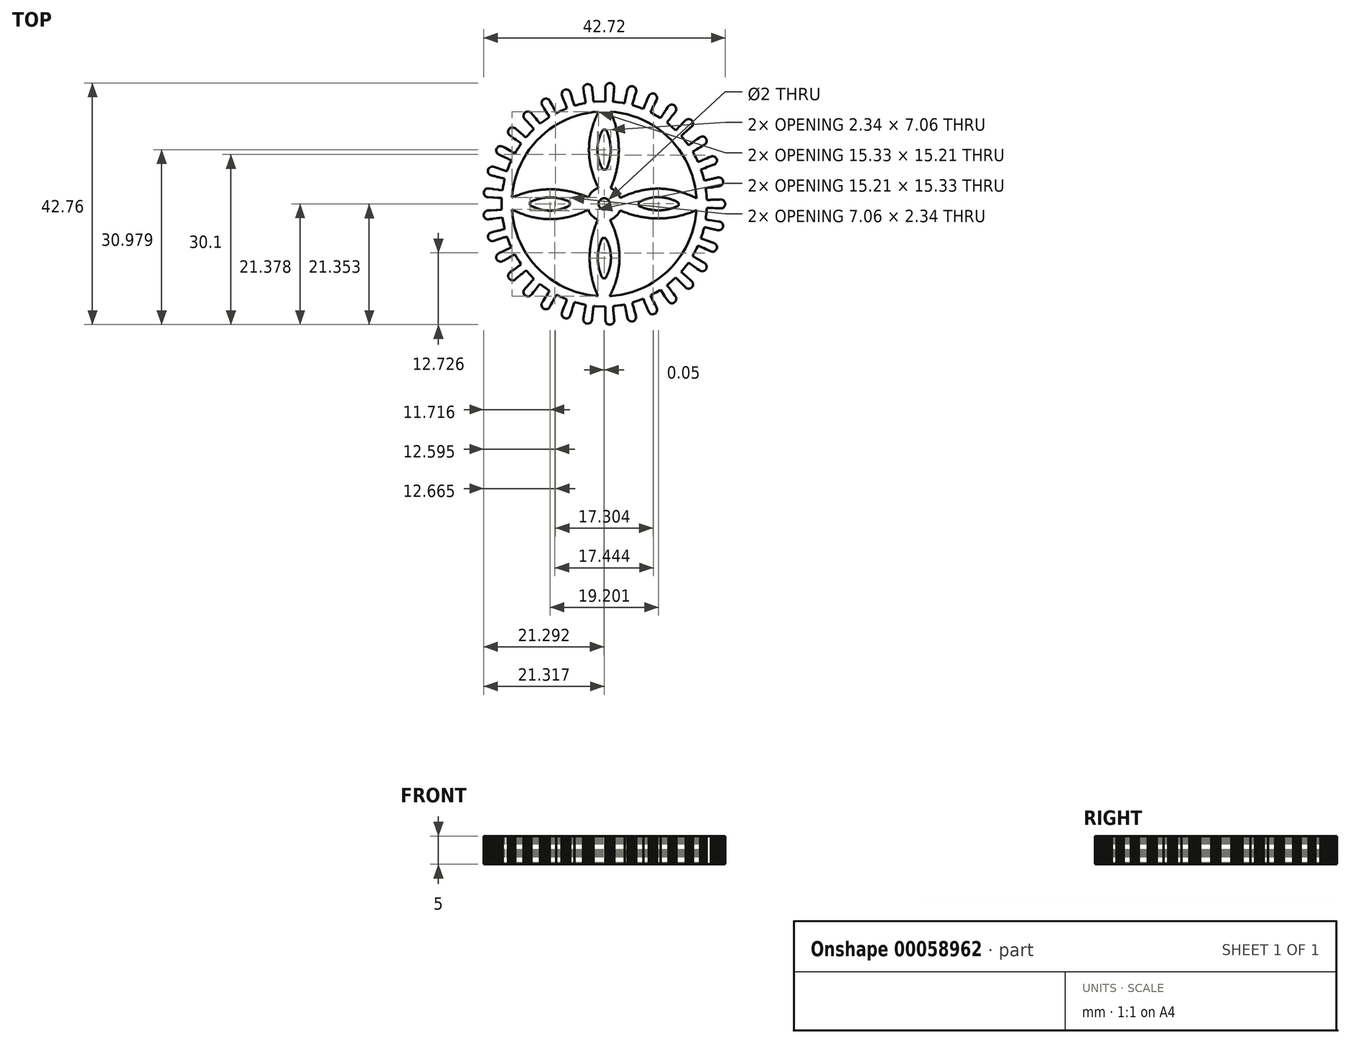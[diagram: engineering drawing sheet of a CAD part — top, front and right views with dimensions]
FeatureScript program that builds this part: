
annotation { "Feature Type Name" : "Feature", "Feature Type Description" : "" }
export const myFeature = defineFeature(function(context is Context, id is Id, definition is map)
    precondition{}
    {
        {
            var Q0;
            Q0=qCreatedBy(makeId("Top.planeOp"),FACE);
            var sketch = newSketch(context, id + "F0", { "sketchPlane" : qUnion([Q0])});
            skLineSegment(sketch, "E0", {"start": v(17.14, -0.7) * mm, "end": v(17.3, -0.7) * mm});
            skLineSegment(sketch, "E1", {"start": v(17.3, -0.7) * mm, "end": v(17.5, -0.7) * mm});
            skLineSegment(sketch, "E2", {"start": v(17.5, -0.7) * mm, "end": v(17.68, -0.71) * mm});
            skLineSegment(sketch, "E3", {"start": v(17.68, -0.71) * mm, "end": v(17.87, -0.72) * mm});
            skLineSegment(sketch, "E4", {"start": v(17.87, -0.72) * mm, "end": v(18.06, -0.73) * mm});
            skLineSegment(sketch, "E5", {"start": v(18.06, -0.73) * mm, "end": v(18.25, -0.73) * mm});
            skLineSegment(sketch, "E6", {"start": v(18.25, -0.73) * mm, "end": v(18.45, -0.74) * mm});
            skLineSegment(sketch, "E7", {"start": v(18.45, -0.74) * mm, "end": v(18.63, -0.75) * mm});
            skLineSegment(sketch, "E8", {"start": v(18.63, -0.75) * mm, "end": v(18.82, -0.75) * mm});
            skLineSegment(sketch, "E9", {"start": v(18.82, -0.75) * mm, "end": v(19.02, -0.76) * mm});
            skLineSegment(sketch, "E10", {"start": v(19.02, -0.76) * mm, "end": v(19.2, -0.77) * mm});
            skLineSegment(sketch, "E11", {"start": v(19.2, -0.77) * mm, "end": v(19.4, -0.78) * mm});
            skLineSegment(sketch, "E12", {"start": v(19.4, -0.78) * mm, "end": v(19.59, -0.78) * mm});
            skLineSegment(sketch, "E13", {"start": v(19.59, -0.78) * mm, "end": v(19.8, -0.76) * mm});
            skLineSegment(sketch, "E14", {"start": v(19.8, -0.76) * mm, "end": v(19.98, -0.68) * mm});
            skLineSegment(sketch, "E15", {"start": v(19.98, -0.68) * mm, "end": v(20.15, -0.56) * mm});
            skLineSegment(sketch, "E16", {"start": v(20.15, -0.56) * mm, "end": v(20.28, -0.4) * mm});
            skLineSegment(sketch, "E17", {"start": v(20.28, -0.4) * mm, "end": v(20.36, -0.2) * mm});
            skLineSegment(sketch, "E18", {"start": v(20.36, -0.2) * mm, "end": v(20.38, 0) * mm});
            skLineSegment(sketch, "E19", {"start": v(20.38, 0) * mm, "end": v(20.36, 0.2) * mm});
            skLineSegment(sketch, "E20", {"start": v(20.36, 0.2) * mm, "end": v(20.28, 0.4) * mm});
            skLineSegment(sketch, "E21", {"start": v(20.28, 0.4) * mm, "end": v(20.15, 0.56) * mm});
            skLineSegment(sketch, "E22", {"start": v(20.15, 0.56) * mm, "end": v(19.98, 0.68) * mm});
            skLineSegment(sketch, "E23", {"start": v(19.98, 0.68) * mm, "end": v(19.8, 0.76) * mm});
            skLineSegment(sketch, "E24", {"start": v(19.8, 0.76) * mm, "end": v(19.59, 0.78) * mm});
            skLineSegment(sketch, "E25", {"start": v(19.59, 0.78) * mm, "end": v(19.4, 0.77) * mm});
            skLineSegment(sketch, "E26", {"start": v(19.4, 0.77) * mm, "end": v(19.2, 0.77) * mm});
            skLineSegment(sketch, "E27", {"start": v(19.2, 0.77) * mm, "end": v(19.02, 0.76) * mm});
            skLineSegment(sketch, "E28", {"start": v(19.02, 0.76) * mm, "end": v(18.83, 0.75) * mm});
            skLineSegment(sketch, "E29", {"start": v(18.83, 0.75) * mm, "end": v(18.64, 0.74) * mm});
            skLineSegment(sketch, "E30", {"start": v(18.64, 0.74) * mm, "end": v(18.45, 0.74) * mm});
            skLineSegment(sketch, "E31", {"start": v(18.45, 0.74) * mm, "end": v(18.26, 0.73) * mm});
            skLineSegment(sketch, "E32", {"start": v(18.26, 0.73) * mm, "end": v(18.07, 0.72) * mm});
            skLineSegment(sketch, "E33", {"start": v(18.07, 0.72) * mm, "end": v(17.87, 0.71) * mm});
            skLineSegment(sketch, "E34", {"start": v(17.87, 0.71) * mm, "end": v(17.69, 0.7) * mm});
            skLineSegment(sketch, "E35", {"start": v(17.69, 0.7) * mm, "end": v(17.5, 0.7) * mm});
            skLineSegment(sketch, "E36", {"start": v(17.5, 0.7) * mm, "end": v(17.3, 0.7) * mm});
            skLineSegment(sketch, "E37", {"start": v(17.3, 0.7) * mm, "end": v(17.14, 0.69) * mm});
            skLineSegment(sketch, "E38", {"start": v(17.14, 0.69) * mm, "end": v(17.12, 0.88) * mm});
            skLineSegment(sketch, "E39", {"start": v(17.12, 0.88) * mm, "end": v(17.1, 1.06) * mm});
            skLineSegment(sketch, "E40", {"start": v(17.1, 1.06) * mm, "end": v(17.09, 1.25) * mm});
            skLineSegment(sketch, "E41", {"start": v(17.09, 1.25) * mm, "end": v(17.07, 1.44) * mm});
            skLineSegment(sketch, "E42", {"start": v(17.07, 1.44) * mm, "end": v(17.05, 1.63) * mm});
            skLineSegment(sketch, "E43", {"start": v(17.05, 1.63) * mm, "end": v(17.03, 1.82) * mm});
            skLineSegment(sketch, "E44", {"start": v(17.03, 1.82) * mm, "end": v(17.01, 2) * mm});
            skLineSegment(sketch, "E45", {"start": v(17.01, 2) * mm, "end": v(17, 2.2) * mm});
            skLineSegment(sketch, "E46", {"start": v(17, 2.2) * mm, "end": v(16.98, 2.38) * mm});
            skLineSegment(sketch, "E47", {"start": v(16.98, 2.38) * mm, "end": v(16.96, 2.57) * mm});
            skLineSegment(sketch, "E48", {"start": v(16.96, 2.57) * mm, "end": v(16.94, 2.76) * mm});
            skLineSegment(sketch, "E49", {"start": v(16.94, 2.76) * mm, "end": v(17.13, 2.79) * mm});
            skLineSegment(sketch, "E50", {"start": v(17.13, 2.79) * mm, "end": v(17.32, 2.82) * mm});
            skLineSegment(sketch, "E51", {"start": v(17.32, 2.82) * mm, "end": v(17.5, 2.85) * mm});
            skLineSegment(sketch, "E52", {"start": v(17.5, 2.85) * mm, "end": v(17.7, 2.87) * mm});
            skLineSegment(sketch, "E53", {"start": v(17.7, 2.87) * mm, "end": v(17.88, 2.9) * mm});
            skLineSegment(sketch, "E54", {"start": v(17.88, 2.9) * mm, "end": v(18.07, 2.93) * mm});
            skLineSegment(sketch, "E55", {"start": v(18.07, 2.93) * mm, "end": v(18.26, 2.96) * mm});
            skLineSegment(sketch, "E56", {"start": v(18.26, 2.96) * mm, "end": v(18.45, 3) * mm});
            skLineSegment(sketch, "E57", {"start": v(18.45, 3) * mm, "end": v(18.64, 3.02) * mm});
            skLineSegment(sketch, "E58", {"start": v(18.64, 3.02) * mm, "end": v(18.82, 3.05) * mm});
            skLineSegment(sketch, "E59", {"start": v(18.82, 3.05) * mm, "end": v(19.01, 3.08) * mm});
            skLineSegment(sketch, "E60", {"start": v(19.01, 3.08) * mm, "end": v(19.2, 3.1) * mm});
            skLineSegment(sketch, "E61", {"start": v(19.2, 3.1) * mm, "end": v(19.4, 3.14) * mm});
            skLineSegment(sketch, "E62", {"start": v(19.4, 3.14) * mm, "end": v(19.6, 3.21) * mm});
            skLineSegment(sketch, "E63", {"start": v(19.6, 3.21) * mm, "end": v(19.76, 3.33) * mm});
            skLineSegment(sketch, "E64", {"start": v(19.76, 3.33) * mm, "end": v(19.9, 3.5) * mm});
            skLineSegment(sketch, "E65", {"start": v(19.9, 3.5) * mm, "end": v(19.98, 3.68) * mm});
            skLineSegment(sketch, "E66", {"start": v(19.98, 3.68) * mm, "end": v(20.01, 3.88) * mm});
            skLineSegment(sketch, "E67", {"start": v(20.01, 3.88) * mm, "end": v(20, 4.05) * mm});
            skLineSegment(sketch, "E68", {"start": v(20, 4.05) * mm, "end": v(19.93, 4.25) * mm});
            skLineSegment(sketch, "E69", {"start": v(19.93, 4.25) * mm, "end": v(19.82, 4.42) * mm});
            skLineSegment(sketch, "E70", {"start": v(19.82, 4.42) * mm, "end": v(19.66, 4.55) * mm});
            skLineSegment(sketch, "E71", {"start": v(19.66, 4.55) * mm, "end": v(19.48, 4.64) * mm});
            skLineSegment(sketch, "E72", {"start": v(19.48, 4.64) * mm, "end": v(19.27, 4.68) * mm});
            skLineSegment(sketch, "E73", {"start": v(19.27, 4.68) * mm, "end": v(19.23, 4.68) * mm});
            skLineSegment(sketch, "E74", {"start": v(19.23, 4.68) * mm, "end": v(19.07, 4.67) * mm});
            skLineSegment(sketch, "E75", {"start": v(19.07, 4.67) * mm, "end": v(18.88, 4.62) * mm});
            skLineSegment(sketch, "E76", {"start": v(18.88, 4.62) * mm, "end": v(18.7, 4.58) * mm});
            skLineSegment(sketch, "E77", {"start": v(18.7, 4.58) * mm, "end": v(18.51, 4.54) * mm});
            skLineSegment(sketch, "E78", {"start": v(18.51, 4.54) * mm, "end": v(18.33, 4.5) * mm});
            skLineSegment(sketch, "E79", {"start": v(18.33, 4.5) * mm, "end": v(18.14, 4.45) * mm});
            skLineSegment(sketch, "E80", {"start": v(18.14, 4.45) * mm, "end": v(17.95, 4.4) * mm});
            skLineSegment(sketch, "E81", {"start": v(17.95, 4.4) * mm, "end": v(17.77, 4.36) * mm});
            skLineSegment(sketch, "E82", {"start": v(17.77, 4.36) * mm, "end": v(17.59, 4.32) * mm});
            skLineSegment(sketch, "E83", {"start": v(17.59, 4.32) * mm, "end": v(17.4, 4.28) * mm});
            skLineSegment(sketch, "E84", {"start": v(17.4, 4.28) * mm, "end": v(17.21, 4.24) * mm});
            skLineSegment(sketch, "E85", {"start": v(17.21, 4.24) * mm, "end": v(17.03, 4.2) * mm});
            skLineSegment(sketch, "E86", {"start": v(17.03, 4.2) * mm, "end": v(16.84, 4.15) * mm});
            skLineSegment(sketch, "E87", {"start": v(16.84, 4.15) * mm, "end": v(16.68, 4.11) * mm});
            skLineSegment(sketch, "E88", {"start": v(16.68, 4.11) * mm, "end": v(16.63, 4.3) * mm});
            skLineSegment(sketch, "E89", {"start": v(16.63, 4.3) * mm, "end": v(16.58, 4.47) * mm});
            skLineSegment(sketch, "E90", {"start": v(16.58, 4.47) * mm, "end": v(16.52, 4.66) * mm});
            skLineSegment(sketch, "E91", {"start": v(16.52, 4.66) * mm, "end": v(16.47, 4.84) * mm});
            skLineSegment(sketch, "E92", {"start": v(16.47, 4.84) * mm, "end": v(16.42, 5.02) * mm});
            skLineSegment(sketch, "E93", {"start": v(16.42, 5.02) * mm, "end": v(16.36, 5.2) * mm});
            skLineSegment(sketch, "E94", {"start": v(16.36, 5.2) * mm, "end": v(16.3, 5.38) * mm});
            skLineSegment(sketch, "E95", {"start": v(16.3, 5.38) * mm, "end": v(16.26, 5.56) * mm});
            skLineSegment(sketch, "E96", {"start": v(16.26, 5.56) * mm, "end": v(16.2, 5.75) * mm});
            skLineSegment(sketch, "E97", {"start": v(16.2, 5.75) * mm, "end": v(16.15, 5.93) * mm});
            skLineSegment(sketch, "E98", {"start": v(16.15, 5.93) * mm, "end": v(16.1, 6.1) * mm});
            skLineSegment(sketch, "E99", {"start": v(16.1, 6.1) * mm, "end": v(16.27, 6.17) * mm});
            skLineSegment(sketch, "E100", {"start": v(16.27, 6.17) * mm, "end": v(16.45, 6.24) * mm});
            skLineSegment(sketch, "E101", {"start": v(16.45, 6.24) * mm, "end": v(16.63, 6.3) * mm});
            skLineSegment(sketch, "E102", {"start": v(16.63, 6.3) * mm, "end": v(16.81, 6.37) * mm});
            skLineSegment(sketch, "E103", {"start": v(16.81, 6.37) * mm, "end": v(16.99, 6.43) * mm});
            skLineSegment(sketch, "E104", {"start": v(16.99, 6.43) * mm, "end": v(17.17, 6.5) * mm});
            skLineSegment(sketch, "E105", {"start": v(17.17, 6.5) * mm, "end": v(17.35, 6.56) * mm});
            skLineSegment(sketch, "E106", {"start": v(17.35, 6.56) * mm, "end": v(17.53, 6.62) * mm});
            skLineSegment(sketch, "E107", {"start": v(17.53, 6.62) * mm, "end": v(17.7, 6.69) * mm});
            skLineSegment(sketch, "E108", {"start": v(17.7, 6.69) * mm, "end": v(17.89, 6.75) * mm});
            skLineSegment(sketch, "E109", {"start": v(17.89, 6.75) * mm, "end": v(18.07, 6.81) * mm});
            skLineSegment(sketch, "E110", {"start": v(18.07, 6.81) * mm, "end": v(18.25, 6.88) * mm});
            skLineSegment(sketch, "E111", {"start": v(18.25, 6.88) * mm, "end": v(18.44, 6.95) * mm});
            skLineSegment(sketch, "E112", {"start": v(18.44, 6.95) * mm, "end": v(18.62, 7.06) * mm});
            skLineSegment(sketch, "E113", {"start": v(18.62, 7.06) * mm, "end": v(18.76, 7.2) * mm});
            skLineSegment(sketch, "E114", {"start": v(18.76, 7.2) * mm, "end": v(18.86, 7.39) * mm});
            skLineSegment(sketch, "E115", {"start": v(18.86, 7.39) * mm, "end": v(18.9, 7.59) * mm});
            skLineSegment(sketch, "E116", {"start": v(18.9, 7.59) * mm, "end": v(18.9, 7.8) * mm});
            skLineSegment(sketch, "E117", {"start": v(18.9, 7.8) * mm, "end": v(18.85, 7.95) * mm});
            skLineSegment(sketch, "E118", {"start": v(18.85, 7.95) * mm, "end": v(18.75, 8.13) * mm});
            skLineSegment(sketch, "E119", {"start": v(18.75, 8.13) * mm, "end": v(18.6, 8.28) * mm});
            skLineSegment(sketch, "E120", {"start": v(18.6, 8.28) * mm, "end": v(18.43, 8.38) * mm});
            skLineSegment(sketch, "E121", {"start": v(18.43, 8.38) * mm, "end": v(18.23, 8.44) * mm});
            skLineSegment(sketch, "E122", {"start": v(18.23, 8.44) * mm, "end": v(18.14, 8.44) * mm});
            skLineSegment(sketch, "E123", {"start": v(18.14, 8.44) * mm, "end": v(17.94, 8.42) * mm});
            skLineSegment(sketch, "E124", {"start": v(17.94, 8.42) * mm, "end": v(17.82, 8.38) * mm});
            skLineSegment(sketch, "E125", {"start": v(17.82, 8.38) * mm, "end": v(17.65, 8.3) * mm});
            skLineSegment(sketch, "E126", {"start": v(17.65, 8.3) * mm, "end": v(17.47, 8.23) * mm});
            skLineSegment(sketch, "E127", {"start": v(17.47, 8.23) * mm, "end": v(17.3, 8.15) * mm});
            skLineSegment(sketch, "E128", {"start": v(17.3, 8.15) * mm, "end": v(17.13, 8.07) * mm});
            skLineSegment(sketch, "E129", {"start": v(17.13, 8.07) * mm, "end": v(16.95, 8) * mm});
            skLineSegment(sketch, "E130", {"start": v(16.95, 8) * mm, "end": v(16.78, 7.92) * mm});
            skLineSegment(sketch, "E131", {"start": v(16.78, 7.92) * mm, "end": v(16.6, 7.84) * mm});
            skLineSegment(sketch, "E132", {"start": v(16.6, 7.84) * mm, "end": v(16.43, 7.77) * mm});
            skLineSegment(sketch, "E133", {"start": v(16.43, 7.77) * mm, "end": v(16.25, 7.69) * mm});
            skLineSegment(sketch, "E134", {"start": v(16.25, 7.69) * mm, "end": v(16.08, 7.6) * mm});
            skLineSegment(sketch, "E135", {"start": v(16.08, 7.6) * mm, "end": v(15.9, 7.53) * mm});
            skLineSegment(sketch, "E136", {"start": v(15.9, 7.53) * mm, "end": v(15.73, 7.45) * mm});
            skLineSegment(sketch, "E137", {"start": v(15.73, 7.45) * mm, "end": v(15.58, 7.39) * mm});
            skLineSegment(sketch, "E138", {"start": v(15.58, 7.39) * mm, "end": v(15.5, 7.56) * mm});
            skLineSegment(sketch, "E139", {"start": v(15.5, 7.56) * mm, "end": v(15.4, 7.72) * mm});
            skLineSegment(sketch, "E140", {"start": v(15.4, 7.72) * mm, "end": v(15.32, 7.9) * mm});
            skLineSegment(sketch, "E141", {"start": v(15.32, 7.9) * mm, "end": v(15.24, 8.06) * mm});
            skLineSegment(sketch, "E142", {"start": v(15.24, 8.06) * mm, "end": v(15.15, 8.23) * mm});
            skLineSegment(sketch, "E143", {"start": v(15.15, 8.23) * mm, "end": v(15.06, 8.4) * mm});
            skLineSegment(sketch, "E144", {"start": v(15.06, 8.4) * mm, "end": v(14.98, 8.57) * mm});
            skLineSegment(sketch, "E145", {"start": v(14.98, 8.57) * mm, "end": v(14.89, 8.73) * mm});
            skLineSegment(sketch, "E146", {"start": v(14.89, 8.73) * mm, "end": v(14.8, 8.9) * mm});
            skLineSegment(sketch, "E147", {"start": v(14.8, 8.9) * mm, "end": v(14.72, 9.07) * mm});
            skLineSegment(sketch, "E148", {"start": v(14.72, 9.07) * mm, "end": v(14.63, 9.24) * mm});
            skLineSegment(sketch, "E149", {"start": v(14.63, 9.24) * mm, "end": v(14.8, 9.33) * mm});
            skLineSegment(sketch, "E150", {"start": v(14.8, 9.33) * mm, "end": v(14.96, 9.43) * mm});
            skLineSegment(sketch, "E151", {"start": v(14.96, 9.43) * mm, "end": v(15.12, 9.53) * mm});
            skLineSegment(sketch, "E152", {"start": v(15.12, 9.53) * mm, "end": v(15.28, 9.63) * mm});
            skLineSegment(sketch, "E153", {"start": v(15.28, 9.63) * mm, "end": v(15.45, 9.72) * mm});
            skLineSegment(sketch, "E154", {"start": v(15.45, 9.72) * mm, "end": v(15.61, 9.82) * mm});
            skLineSegment(sketch, "E155", {"start": v(15.61, 9.82) * mm, "end": v(15.78, 9.92) * mm});
            skLineSegment(sketch, "E156", {"start": v(15.78, 9.92) * mm, "end": v(15.94, 10.01) * mm});
            skLineSegment(sketch, "E157", {"start": v(15.94, 10.01) * mm, "end": v(16.1, 10.1) * mm});
            skLineSegment(sketch, "E158", {"start": v(16.1, 10.1) * mm, "end": v(16.27, 10.2) * mm});
            skLineSegment(sketch, "E159", {"start": v(16.27, 10.2) * mm, "end": v(16.43, 10.3) * mm});
            skLineSegment(sketch, "E160", {"start": v(16.43, 10.3) * mm, "end": v(16.6, 10.4) * mm});
            skLineSegment(sketch, "E161", {"start": v(16.6, 10.4) * mm, "end": v(16.77, 10.5) * mm});
            skLineSegment(sketch, "E162", {"start": v(16.77, 10.5) * mm, "end": v(16.93, 10.64) * mm});
            skLineSegment(sketch, "E163", {"start": v(16.93, 10.64) * mm, "end": v(17.04, 10.82) * mm});
            skLineSegment(sketch, "E164", {"start": v(17.04, 10.82) * mm, "end": v(17.1, 11.02) * mm});
            skLineSegment(sketch, "E165", {"start": v(17.1, 11.02) * mm, "end": v(17.1, 11.22) * mm});
            skLineSegment(sketch, "E166", {"start": v(17.1, 11.22) * mm, "end": v(17.06, 11.42) * mm});
            skLineSegment(sketch, "E167", {"start": v(17.06, 11.42) * mm, "end": v(16.99, 11.57) * mm});
            skLineSegment(sketch, "E168", {"start": v(16.99, 11.57) * mm, "end": v(16.85, 11.73) * mm});
            skLineSegment(sketch, "E169", {"start": v(16.85, 11.73) * mm, "end": v(16.68, 11.85) * mm});
            skLineSegment(sketch, "E170", {"start": v(16.68, 11.85) * mm, "end": v(16.49, 11.91) * mm});
            skLineSegment(sketch, "E171", {"start": v(16.49, 11.91) * mm, "end": v(16.32, 11.93) * mm});
            skLineSegment(sketch, "E172", {"start": v(16.32, 11.93) * mm, "end": v(16.12, 11.9) * mm});
            skLineSegment(sketch, "E173", {"start": v(16.12, 11.9) * mm, "end": v(15.93, 11.82) * mm});
            skLineSegment(sketch, "E174", {"start": v(15.93, 11.82) * mm, "end": v(15.9, 11.8) * mm});
            skLineSegment(sketch, "E175", {"start": v(15.9, 11.8) * mm, "end": v(15.74, 11.69) * mm});
            skLineSegment(sketch, "E176", {"start": v(15.74, 11.69) * mm, "end": v(15.58, 11.58) * mm});
            skLineSegment(sketch, "E177", {"start": v(15.58, 11.58) * mm, "end": v(15.42, 11.47) * mm});
            skLineSegment(sketch, "E178", {"start": v(15.42, 11.47) * mm, "end": v(15.27, 11.36) * mm});
            skLineSegment(sketch, "E179", {"start": v(15.27, 11.36) * mm, "end": v(15.11, 11.25) * mm});
            skLineSegment(sketch, "E180", {"start": v(15.11, 11.25) * mm, "end": v(14.96, 11.14) * mm});
            skLineSegment(sketch, "E181", {"start": v(14.96, 11.14) * mm, "end": v(14.8, 11.04) * mm});
            skLineSegment(sketch, "E182", {"start": v(14.8, 11.04) * mm, "end": v(14.65, 10.93) * mm});
            skLineSegment(sketch, "E183", {"start": v(14.65, 10.93) * mm, "end": v(14.49, 10.82) * mm});
            skLineSegment(sketch, "E184", {"start": v(14.49, 10.82) * mm, "end": v(14.33, 10.7) * mm});
            skLineSegment(sketch, "E185", {"start": v(14.33, 10.7) * mm, "end": v(14.18, 10.6) * mm});
            skLineSegment(sketch, "E186", {"start": v(14.18, 10.6) * mm, "end": v(14.02, 10.5) * mm});
            skLineSegment(sketch, "E187", {"start": v(14.02, 10.5) * mm, "end": v(13.88, 10.4) * mm});
            skLineSegment(sketch, "E188", {"start": v(13.88, 10.4) * mm, "end": v(13.77, 10.55) * mm});
            skLineSegment(sketch, "E189", {"start": v(13.77, 10.55) * mm, "end": v(13.65, 10.7) * mm});
            skLineSegment(sketch, "E190", {"start": v(13.65, 10.7) * mm, "end": v(13.53, 10.84) * mm});
            skLineSegment(sketch, "E191", {"start": v(13.53, 10.84) * mm, "end": v(13.42, 11) * mm});
            skLineSegment(sketch, "E192", {"start": v(13.42, 11) * mm, "end": v(13.3, 11.14) * mm});
            skLineSegment(sketch, "E193", {"start": v(13.3, 11.14) * mm, "end": v(13.18, 11.29) * mm});
            skLineSegment(sketch, "E194", {"start": v(13.18, 11.29) * mm, "end": v(13.07, 11.44) * mm});
            skLineSegment(sketch, "E195", {"start": v(13.07, 11.44) * mm, "end": v(12.95, 11.59) * mm});
            skLineSegment(sketch, "E196", {"start": v(12.95, 11.59) * mm, "end": v(12.83, 11.74) * mm});
            skLineSegment(sketch, "E197", {"start": v(12.83, 11.74) * mm, "end": v(12.71, 11.88) * mm});
            skLineSegment(sketch, "E198", {"start": v(12.71, 11.88) * mm, "end": v(12.6, 12.03) * mm});
            skLineSegment(sketch, "E199", {"start": v(12.6, 12.03) * mm, "end": v(12.74, 12.16) * mm});
            skLineSegment(sketch, "E200", {"start": v(12.74, 12.16) * mm, "end": v(12.88, 12.28) * mm});
            skLineSegment(sketch, "E201", {"start": v(12.88, 12.28) * mm, "end": v(13.03, 12.41) * mm});
            skLineSegment(sketch, "E202", {"start": v(13.03, 12.41) * mm, "end": v(13.17, 12.54) * mm});
            skLineSegment(sketch, "E203", {"start": v(13.17, 12.54) * mm, "end": v(13.3, 12.66) * mm});
            skLineSegment(sketch, "E204", {"start": v(13.3, 12.66) * mm, "end": v(13.45, 12.8) * mm});
            skLineSegment(sketch, "E205", {"start": v(13.45, 12.8) * mm, "end": v(13.6, 12.92) * mm});
            skLineSegment(sketch, "E206", {"start": v(13.6, 12.92) * mm, "end": v(13.74, 13.04) * mm});
            skLineSegment(sketch, "E207", {"start": v(13.74, 13.04) * mm, "end": v(13.88, 13.17) * mm});
            skLineSegment(sketch, "E208", {"start": v(13.88, 13.17) * mm, "end": v(14.02, 13.3) * mm});
            skLineSegment(sketch, "E209", {"start": v(14.02, 13.3) * mm, "end": v(14.17, 13.42) * mm});
            skLineSegment(sketch, "E210", {"start": v(14.17, 13.42) * mm, "end": v(14.31, 13.55) * mm});
            skLineSegment(sketch, "E211", {"start": v(14.31, 13.55) * mm, "end": v(14.46, 13.68) * mm});
            skLineSegment(sketch, "E212", {"start": v(14.46, 13.68) * mm, "end": v(14.59, 13.85) * mm});
            skLineSegment(sketch, "E213", {"start": v(14.59, 13.85) * mm, "end": v(14.66, 14.04) * mm});
            skLineSegment(sketch, "E214", {"start": v(14.66, 14.04) * mm, "end": v(14.69, 14.25) * mm});
            skLineSegment(sketch, "E215", {"start": v(14.69, 14.25) * mm, "end": v(14.65, 14.45) * mm});
            skLineSegment(sketch, "E216", {"start": v(14.65, 14.45) * mm, "end": v(14.57, 14.64) * mm});
            skLineSegment(sketch, "E217", {"start": v(14.57, 14.64) * mm, "end": v(14.47, 14.77) * mm});
            skLineSegment(sketch, "E218", {"start": v(14.47, 14.77) * mm, "end": v(14.3, 14.9) * mm});
            skLineSegment(sketch, "E219", {"start": v(14.3, 14.9) * mm, "end": v(14.12, 14.98) * mm});
            skLineSegment(sketch, "E220", {"start": v(14.12, 14.98) * mm, "end": v(13.92, 15.01) * mm});
            skLineSegment(sketch, "E221", {"start": v(13.92, 15.01) * mm, "end": v(13.71, 14.99) * mm});
            skLineSegment(sketch, "E222", {"start": v(13.71, 14.99) * mm, "end": v(13.52, 14.91) * mm});
            skLineSegment(sketch, "E223", {"start": v(13.52, 14.91) * mm, "end": v(13.35, 14.79) * mm});
            skLineSegment(sketch, "E224", {"start": v(13.35, 14.79) * mm, "end": v(13.22, 14.65) * mm});
            skLineSegment(sketch, "E225", {"start": v(13.22, 14.65) * mm, "end": v(13.1, 14.51) * mm});
            skLineSegment(sketch, "E226", {"start": v(13.1, 14.51) * mm, "end": v(12.96, 14.38) * mm});
            skLineSegment(sketch, "E227", {"start": v(12.96, 14.38) * mm, "end": v(12.82, 14.24) * mm});
            skLineSegment(sketch, "E228", {"start": v(12.82, 14.24) * mm, "end": v(12.7, 14.1) * mm});
            skLineSegment(sketch, "E229", {"start": v(12.7, 14.1) * mm, "end": v(12.56, 13.97) * mm});
            skLineSegment(sketch, "E230", {"start": v(12.56, 13.97) * mm, "end": v(12.43, 13.83) * mm});
            skLineSegment(sketch, "E231", {"start": v(12.43, 13.83) * mm, "end": v(12.3, 13.7) * mm});
            skLineSegment(sketch, "E232", {"start": v(12.3, 13.7) * mm, "end": v(12.16, 13.56) * mm});
            skLineSegment(sketch, "E233", {"start": v(12.16, 13.56) * mm, "end": v(12.03, 13.42) * mm});
            skLineSegment(sketch, "E234", {"start": v(12.03, 13.42) * mm, "end": v(11.9, 13.29) * mm});
            skLineSegment(sketch, "E235", {"start": v(11.9, 13.29) * mm, "end": v(11.76, 13.15) * mm});
            skLineSegment(sketch, "E236", {"start": v(11.76, 13.15) * mm, "end": v(11.65, 13.03) * mm});
            skLineSegment(sketch, "E237", {"start": v(11.65, 13.03) * mm, "end": v(11.5, 13.15) * mm});
            skLineSegment(sketch, "E238", {"start": v(11.5, 13.15) * mm, "end": v(11.36, 13.28) * mm});
            skLineSegment(sketch, "E239", {"start": v(11.36, 13.28) * mm, "end": v(11.22, 13.4) * mm});
            skLineSegment(sketch, "E240", {"start": v(11.22, 13.4) * mm, "end": v(11.08, 13.53) * mm});
            skLineSegment(sketch, "E241", {"start": v(11.08, 13.53) * mm, "end": v(10.93, 13.65) * mm});
            skLineSegment(sketch, "E242", {"start": v(10.93, 13.65) * mm, "end": v(10.79, 13.77) * mm});
            skLineSegment(sketch, "E243", {"start": v(10.79, 13.77) * mm, "end": v(10.65, 13.9) * mm});
            skLineSegment(sketch, "E244", {"start": v(10.65, 13.9) * mm, "end": v(10.5, 14.02) * mm});
            skLineSegment(sketch, "E245", {"start": v(10.5, 14.02) * mm, "end": v(10.36, 14.15) * mm});
            skLineSegment(sketch, "E246", {"start": v(10.36, 14.15) * mm, "end": v(10.22, 14.27) * mm});
            skLineSegment(sketch, "E247", {"start": v(10.22, 14.27) * mm, "end": v(10.07, 14.4) * mm});
            skLineSegment(sketch, "E248", {"start": v(10.07, 14.4) * mm, "end": v(10.19, 14.54) * mm});
            skLineSegment(sketch, "E249", {"start": v(10.19, 14.54) * mm, "end": v(10.3, 14.7) * mm});
            skLineSegment(sketch, "E250", {"start": v(10.3, 14.7) * mm, "end": v(10.42, 14.85) * mm});
            skLineSegment(sketch, "E251", {"start": v(10.42, 14.85) * mm, "end": v(10.54, 15) * mm});
            skLineSegment(sketch, "E252", {"start": v(10.54, 15) * mm, "end": v(10.65, 15.15) * mm});
            skLineSegment(sketch, "E253", {"start": v(10.65, 15.15) * mm, "end": v(10.77, 15.3) * mm});
            skLineSegment(sketch, "E254", {"start": v(10.77, 15.3) * mm, "end": v(10.89, 15.45) * mm});
            skLineSegment(sketch, "E255", {"start": v(10.89, 15.45) * mm, "end": v(11, 15.6) * mm});
            skLineSegment(sketch, "E256", {"start": v(11, 15.6) * mm, "end": v(11.12, 15.75) * mm});
            skLineSegment(sketch, "E257", {"start": v(11.12, 15.75) * mm, "end": v(11.24, 15.9) * mm});
            skLineSegment(sketch, "E258", {"start": v(11.24, 15.9) * mm, "end": v(11.35, 16.05) * mm});
            skLineSegment(sketch, "E259", {"start": v(11.35, 16.05) * mm, "end": v(11.47, 16.2) * mm});
            skLineSegment(sketch, "E260", {"start": v(11.47, 16.2) * mm, "end": v(11.6, 16.37) * mm});
            skLineSegment(sketch, "E261", {"start": v(11.6, 16.37) * mm, "end": v(11.68, 16.55) * mm});
            skLineSegment(sketch, "E262", {"start": v(11.68, 16.55) * mm, "end": v(11.72, 16.76) * mm});
            skLineSegment(sketch, "E263", {"start": v(11.72, 16.76) * mm, "end": v(11.7, 16.96) * mm});
            skLineSegment(sketch, "E264", {"start": v(11.7, 16.96) * mm, "end": v(11.64, 17.16) * mm});
            skLineSegment(sketch, "E265", {"start": v(11.64, 17.16) * mm, "end": v(11.52, 17.33) * mm});
            skLineSegment(sketch, "E266", {"start": v(11.52, 17.33) * mm, "end": v(11.4, 17.44) * mm});
            skLineSegment(sketch, "E267", {"start": v(11.4, 17.44) * mm, "end": v(11.21, 17.53) * mm});
            skLineSegment(sketch, "E268", {"start": v(11.21, 17.53) * mm, "end": v(11.01, 17.58) * mm});
            skLineSegment(sketch, "E269", {"start": v(11.01, 17.58) * mm, "end": v(10.93, 17.58) * mm});
            skLineSegment(sketch, "E270", {"start": v(10.93, 17.58) * mm, "end": v(10.72, 17.55) * mm});
            skLineSegment(sketch, "E271", {"start": v(10.72, 17.55) * mm, "end": v(10.53, 17.47) * mm});
            skLineSegment(sketch, "E272", {"start": v(10.53, 17.47) * mm, "end": v(10.37, 17.34) * mm});
            skLineSegment(sketch, "E273", {"start": v(10.37, 17.34) * mm, "end": v(10.3, 17.24) * mm});
            skLineSegment(sketch, "E274", {"start": v(10.3, 17.24) * mm, "end": v(10.2, 17.08) * mm});
            skLineSegment(sketch, "E275", {"start": v(10.2, 17.08) * mm, "end": v(10.09, 16.92) * mm});
            skLineSegment(sketch, "E276", {"start": v(10.09, 16.92) * mm, "end": v(9.98, 16.76) * mm});
            skLineSegment(sketch, "E277", {"start": v(9.98, 16.76) * mm, "end": v(9.88, 16.6) * mm});
            skLineSegment(sketch, "E278", {"start": v(9.88, 16.6) * mm, "end": v(9.77, 16.45) * mm});
            skLineSegment(sketch, "E279", {"start": v(9.77, 16.45) * mm, "end": v(9.67, 16.28) * mm});
            skLineSegment(sketch, "E280", {"start": v(9.67, 16.28) * mm, "end": v(9.56, 16.13) * mm});
            skLineSegment(sketch, "E281", {"start": v(9.56, 16.13) * mm, "end": v(9.46, 15.97) * mm});
            skLineSegment(sketch, "E282", {"start": v(9.46, 15.97) * mm, "end": v(9.36, 15.8) * mm});
            skLineSegment(sketch, "E283", {"start": v(9.36, 15.8) * mm, "end": v(9.25, 15.65) * mm});
            skLineSegment(sketch, "E284", {"start": v(9.25, 15.65) * mm, "end": v(9.15, 15.5) * mm});
            skLineSegment(sketch, "E285", {"start": v(9.15, 15.5) * mm, "end": v(9.04, 15.33) * mm});
            skLineSegment(sketch, "E286", {"start": v(9.04, 15.33) * mm, "end": v(8.95, 15.2) * mm});
            skLineSegment(sketch, "E287", {"start": v(8.95, 15.2) * mm, "end": v(8.79, 15.29) * mm});
            skLineSegment(sketch, "E288", {"start": v(8.79, 15.29) * mm, "end": v(8.62, 15.38) * mm});
            skLineSegment(sketch, "E289", {"start": v(8.62, 15.38) * mm, "end": v(8.46, 15.48) * mm});
            skLineSegment(sketch, "E290", {"start": v(8.46, 15.48) * mm, "end": v(8.3, 15.57) * mm});
            skLineSegment(sketch, "E291", {"start": v(8.3, 15.57) * mm, "end": v(8.13, 15.67) * mm});
            skLineSegment(sketch, "E292", {"start": v(8.13, 15.67) * mm, "end": v(7.97, 15.76) * mm});
            skLineSegment(sketch, "E293", {"start": v(7.97, 15.76) * mm, "end": v(7.8, 15.86) * mm});
            skLineSegment(sketch, "E294", {"start": v(7.8, 15.86) * mm, "end": v(7.64, 15.95) * mm});
            skLineSegment(sketch, "E295", {"start": v(7.64, 15.95) * mm, "end": v(7.48, 16.04) * mm});
            skLineSegment(sketch, "E296", {"start": v(7.48, 16.04) * mm, "end": v(7.31, 16.14) * mm});
            skLineSegment(sketch, "E297", {"start": v(7.31, 16.14) * mm, "end": v(7.15, 16.23) * mm});
            skLineSegment(sketch, "E298", {"start": v(7.15, 16.23) * mm, "end": v(7.23, 16.4) * mm});
            skLineSegment(sketch, "E299", {"start": v(7.23, 16.4) * mm, "end": v(7.32, 16.57) * mm});
            skLineSegment(sketch, "E300", {"start": v(7.32, 16.57) * mm, "end": v(7.4, 16.74) * mm});
            skLineSegment(sketch, "E301", {"start": v(7.4, 16.74) * mm, "end": v(7.5, 16.91) * mm});
            skLineSegment(sketch, "E302", {"start": v(7.5, 16.91) * mm, "end": v(7.58, 17.08) * mm});
            skLineSegment(sketch, "E303", {"start": v(7.58, 17.08) * mm, "end": v(7.66, 17.25) * mm});
            skLineSegment(sketch, "E304", {"start": v(7.66, 17.25) * mm, "end": v(7.75, 17.42) * mm});
            skLineSegment(sketch, "E305", {"start": v(7.75, 17.42) * mm, "end": v(7.83, 17.6) * mm});
            skLineSegment(sketch, "E306", {"start": v(7.83, 17.6) * mm, "end": v(7.92, 17.76) * mm});
            skLineSegment(sketch, "E307", {"start": v(7.92, 17.76) * mm, "end": v(8, 17.93) * mm});
            skLineSegment(sketch, "E308", {"start": v(8, 17.93) * mm, "end": v(8.09, 18.1) * mm});
            skLineSegment(sketch, "E309", {"start": v(8.09, 18.1) * mm, "end": v(8.18, 18.28) * mm});
            skLineSegment(sketch, "E310", {"start": v(8.18, 18.28) * mm, "end": v(8.27, 18.46) * mm});
            skLineSegment(sketch, "E311", {"start": v(8.27, 18.46) * mm, "end": v(8.32, 18.66) * mm});
            skLineSegment(sketch, "E312", {"start": v(8.32, 18.66) * mm, "end": v(8.32, 18.86) * mm});
            skLineSegment(sketch, "E313", {"start": v(8.32, 18.86) * mm, "end": v(8.26, 19.06) * mm});
            skLineSegment(sketch, "E314", {"start": v(8.26, 19.06) * mm, "end": v(8.16, 19.24) * mm});
            skLineSegment(sketch, "E315", {"start": v(8.16, 19.24) * mm, "end": v(8.01, 19.39) * mm});
            skLineSegment(sketch, "E316", {"start": v(8.01, 19.39) * mm, "end": v(7.87, 19.47) * mm});
            skLineSegment(sketch, "E317", {"start": v(7.87, 19.47) * mm, "end": v(7.67, 19.53) * mm});
            skLineSegment(sketch, "E318", {"start": v(7.67, 19.53) * mm, "end": v(7.55, 19.54) * mm});
            skLineSegment(sketch, "E319", {"start": v(7.55, 19.54) * mm, "end": v(7.34, 19.51) * mm});
            skLineSegment(sketch, "E320", {"start": v(7.34, 19.51) * mm, "end": v(7.15, 19.44) * mm});
            skLineSegment(sketch, "E321", {"start": v(7.15, 19.44) * mm, "end": v(6.99, 19.3) * mm});
            skLineSegment(sketch, "E322", {"start": v(6.99, 19.3) * mm, "end": v(6.87, 19.14) * mm});
            skLineSegment(sketch, "E323", {"start": v(6.87, 19.14) * mm, "end": v(6.83, 19.07) * mm});
            skLineSegment(sketch, "E324", {"start": v(6.83, 19.07) * mm, "end": v(6.76, 18.9) * mm});
            skLineSegment(sketch, "E325", {"start": v(6.76, 18.9) * mm, "end": v(6.68, 18.72) * mm});
            skLineSegment(sketch, "E326", {"start": v(6.68, 18.72) * mm, "end": v(6.61, 18.54) * mm});
            skLineSegment(sketch, "E327", {"start": v(6.61, 18.54) * mm, "end": v(6.54, 18.37) * mm});
            skLineSegment(sketch, "E328", {"start": v(6.54, 18.37) * mm, "end": v(6.47, 18.2) * mm});
            skLineSegment(sketch, "E329", {"start": v(6.47, 18.2) * mm, "end": v(6.4, 18.01) * mm});
            skLineSegment(sketch, "E330", {"start": v(6.4, 18.01) * mm, "end": v(6.32, 17.84) * mm});
            skLineSegment(sketch, "E331", {"start": v(6.32, 17.84) * mm, "end": v(6.25, 17.66) * mm});
            skLineSegment(sketch, "E332", {"start": v(6.25, 17.66) * mm, "end": v(6.18, 17.49) * mm});
            skLineSegment(sketch, "E333", {"start": v(6.18, 17.49) * mm, "end": v(6.1, 17.31) * mm});
            skLineSegment(sketch, "E334", {"start": v(6.1, 17.31) * mm, "end": v(6.03, 17.14) * mm});
            skLineSegment(sketch, "E335", {"start": v(6.03, 17.14) * mm, "end": v(5.96, 16.96) * mm});
            skLineSegment(sketch, "E336", {"start": v(5.96, 16.96) * mm, "end": v(5.9, 16.8) * mm});
            skLineSegment(sketch, "E337", {"start": v(5.9, 16.8) * mm, "end": v(5.72, 16.87) * mm});
            skLineSegment(sketch, "E338", {"start": v(5.72, 16.87) * mm, "end": v(5.54, 16.93) * mm});
            skLineSegment(sketch, "E339", {"start": v(5.54, 16.93) * mm, "end": v(5.36, 17) * mm});
            skLineSegment(sketch, "E340", {"start": v(5.36, 17) * mm, "end": v(5.18, 17.05) * mm});
            skLineSegment(sketch, "E341", {"start": v(5.18, 17.05) * mm, "end": v(5, 17.12) * mm});
            skLineSegment(sketch, "E342", {"start": v(5, 17.12) * mm, "end": v(4.82, 17.18) * mm});
            skLineSegment(sketch, "E343", {"start": v(4.82, 17.18) * mm, "end": v(4.64, 17.24) * mm});
            skLineSegment(sketch, "E344", {"start": v(4.64, 17.24) * mm, "end": v(4.47, 17.3) * mm});
            skLineSegment(sketch, "E345", {"start": v(4.47, 17.3) * mm, "end": v(4.29, 17.36) * mm});
            skLineSegment(sketch, "E346", {"start": v(4.29, 17.36) * mm, "end": v(4.1, 17.43) * mm});
            skLineSegment(sketch, "E347", {"start": v(4.1, 17.43) * mm, "end": v(3.93, 17.49) * mm});
            skLineSegment(sketch, "E348", {"start": v(3.93, 17.49) * mm, "end": v(3.98, 17.67) * mm});
            skLineSegment(sketch, "E349", {"start": v(3.98, 17.67) * mm, "end": v(4.03, 17.85) * mm});
            skLineSegment(sketch, "E350", {"start": v(4.03, 17.85) * mm, "end": v(4.08, 18.04) * mm});
            skLineSegment(sketch, "E351", {"start": v(4.08, 18.04) * mm, "end": v(4.14, 18.22) * mm});
            skLineSegment(sketch, "E352", {"start": v(4.14, 18.22) * mm, "end": v(4.19, 18.4) * mm});
            skLineSegment(sketch, "E353", {"start": v(4.19, 18.4) * mm, "end": v(4.24, 18.59) * mm});
            skLineSegment(sketch, "E354", {"start": v(4.24, 18.59) * mm, "end": v(4.3, 18.77) * mm});
            skLineSegment(sketch, "E355", {"start": v(4.3, 18.77) * mm, "end": v(4.34, 18.95) * mm});
            skLineSegment(sketch, "E356", {"start": v(4.34, 18.95) * mm, "end": v(4.4, 19.14) * mm});
            skLineSegment(sketch, "E357", {"start": v(4.4, 19.14) * mm, "end": v(4.45, 19.32) * mm});
            skLineSegment(sketch, "E358", {"start": v(4.45, 19.32) * mm, "end": v(4.5, 19.5) * mm});
            skLineSegment(sketch, "E359", {"start": v(4.5, 19.5) * mm, "end": v(4.55, 19.69) * mm});
            skLineSegment(sketch, "E360", {"start": v(4.55, 19.69) * mm, "end": v(4.6, 19.88) * mm});
            skLineSegment(sketch, "E361", {"start": v(4.6, 19.88) * mm, "end": v(4.62, 20.09) * mm});
            skLineSegment(sketch, "E362", {"start": v(4.62, 20.09) * mm, "end": v(4.58, 20.3) * mm});
            skLineSegment(sketch, "E363", {"start": v(4.58, 20.3) * mm, "end": v(4.49, 20.48) * mm});
            skLineSegment(sketch, "E364", {"start": v(4.49, 20.48) * mm, "end": v(4.35, 20.63) * mm});
            skLineSegment(sketch, "E365", {"start": v(4.35, 20.63) * mm, "end": v(4.18, 20.75) * mm});
            skLineSegment(sketch, "E366", {"start": v(4.18, 20.75) * mm, "end": v(4.02, 20.8) * mm});
            skLineSegment(sketch, "E367", {"start": v(4.02, 20.8) * mm, "end": v(3.86, 20.82) * mm});
            skLineSegment(sketch, "E368", {"start": v(3.86, 20.82) * mm, "end": v(3.65, 20.8) * mm});
            skLineSegment(sketch, "E369", {"start": v(3.65, 20.8) * mm, "end": v(3.46, 20.73) * mm});
            skLineSegment(sketch, "E370", {"start": v(3.46, 20.73) * mm, "end": v(3.3, 20.6) * mm});
            skLineSegment(sketch, "E371", {"start": v(3.3, 20.6) * mm, "end": v(3.17, 20.44) * mm});
            skLineSegment(sketch, "E372", {"start": v(3.17, 20.44) * mm, "end": v(3.09, 20.25) * mm});
            skLineSegment(sketch, "E373", {"start": v(3.09, 20.25) * mm, "end": v(3.08, 20.21) * mm});
            skLineSegment(sketch, "E374", {"start": v(3.08, 20.21) * mm, "end": v(3.04, 20.03) * mm});
            skLineSegment(sketch, "E375", {"start": v(3.04, 20.03) * mm, "end": v(3, 19.84) * mm});
            skLineSegment(sketch, "E376", {"start": v(3, 19.84) * mm, "end": v(2.96, 19.65) * mm});
            skLineSegment(sketch, "E377", {"start": v(2.96, 19.65) * mm, "end": v(2.93, 19.47) * mm});
            skLineSegment(sketch, "E378", {"start": v(2.93, 19.47) * mm, "end": v(2.89, 19.28) * mm});
            skLineSegment(sketch, "E379", {"start": v(2.89, 19.28) * mm, "end": v(2.85, 19.1) * mm});
            skLineSegment(sketch, "E380", {"start": v(2.85, 19.1) * mm, "end": v(2.81, 18.9) * mm});
            skLineSegment(sketch, "E381", {"start": v(2.81, 18.9) * mm, "end": v(2.77, 18.72) * mm});
            skLineSegment(sketch, "E382", {"start": v(2.77, 18.72) * mm, "end": v(2.74, 18.53) * mm});
            skLineSegment(sketch, "E383", {"start": v(2.74, 18.53) * mm, "end": v(2.7, 18.35) * mm});
            skLineSegment(sketch, "E384", {"start": v(2.7, 18.35) * mm, "end": v(2.66, 18.16) * mm});
            skLineSegment(sketch, "E385", {"start": v(2.66, 18.16) * mm, "end": v(2.62, 17.97) * mm});
            skLineSegment(sketch, "E386", {"start": v(2.62, 17.97) * mm, "end": v(2.6, 17.81) * mm});
            skLineSegment(sketch, "E387", {"start": v(2.6, 17.81) * mm, "end": v(2.4, 17.84) * mm});
            skLineSegment(sketch, "E388", {"start": v(2.4, 17.84) * mm, "end": v(2.22, 17.87) * mm});
            skLineSegment(sketch, "E389", {"start": v(2.22, 17.87) * mm, "end": v(2.03, 17.9) * mm});
            skLineSegment(sketch, "E390", {"start": v(2.03, 17.9) * mm, "end": v(1.84, 17.92) * mm});
            skLineSegment(sketch, "E391", {"start": v(1.84, 17.92) * mm, "end": v(1.65, 17.95) * mm});
            skLineSegment(sketch, "E392", {"start": v(1.65, 17.95) * mm, "end": v(1.47, 17.97) * mm});
            skLineSegment(sketch, "E393", {"start": v(1.47, 17.97) * mm, "end": v(1.28, 18) * mm});
            skLineSegment(sketch, "E394", {"start": v(1.28, 18) * mm, "end": v(1.1, 18.03) * mm});
            skLineSegment(sketch, "E395", {"start": v(1.1, 18.03) * mm, "end": v(0.9, 18.05) * mm});
            skLineSegment(sketch, "E396", {"start": v(0.9, 18.05) * mm, "end": v(0.72, 18.08) * mm});
            skLineSegment(sketch, "E397", {"start": v(0.72, 18.08) * mm, "end": v(0.53, 18.1) * mm});
            skLineSegment(sketch, "E398", {"start": v(0.53, 18.1) * mm, "end": v(0.55, 18.3) * mm});
            skLineSegment(sketch, "E399", {"start": v(0.55, 18.3) * mm, "end": v(0.56, 18.49) * mm});
            skLineSegment(sketch, "E400", {"start": v(0.56, 18.49) * mm, "end": v(0.58, 18.68) * mm});
            skLineSegment(sketch, "E401", {"start": v(0.58, 18.68) * mm, "end": v(0.6, 18.87) * mm});
            skLineSegment(sketch, "E402", {"start": v(0.6, 18.87) * mm, "end": v(0.61, 19.05) * mm});
            skLineSegment(sketch, "E403", {"start": v(0.61, 19.05) * mm, "end": v(0.63, 19.25) * mm});
            skLineSegment(sketch, "E404", {"start": v(0.63, 19.25) * mm, "end": v(0.64, 19.44) * mm});
            skLineSegment(sketch, "E405", {"start": v(0.64, 19.44) * mm, "end": v(0.66, 19.62) * mm});
            skLineSegment(sketch, "E406", {"start": v(0.66, 19.62) * mm, "end": v(0.68, 19.82) * mm});
            skLineSegment(sketch, "E407", {"start": v(0.68, 19.82) * mm, "end": v(0.7, 20) * mm});
            skLineSegment(sketch, "E408", {"start": v(0.7, 20) * mm, "end": v(0.7, 20.2) * mm});
            skLineSegment(sketch, "E409", {"start": v(0.7, 20.2) * mm, "end": v(0.72, 20.39) * mm});
            skLineSegment(sketch, "E410", {"start": v(0.72, 20.39) * mm, "end": v(0.74, 20.59) * mm});
            skLineSegment(sketch, "E411", {"start": v(0.74, 20.59) * mm, "end": v(0.72, 20.8) * mm});
            skLineSegment(sketch, "E412", {"start": v(0.72, 20.8) * mm, "end": v(0.64, 20.99) * mm});
            skLineSegment(sketch, "E413", {"start": v(0.64, 20.99) * mm, "end": v(0.51, 21.15) * mm});
            skLineSegment(sketch, "E414", {"start": v(0.51, 21.15) * mm, "end": v(0.35, 21.28) * mm});
            skLineSegment(sketch, "E415", {"start": v(0.35, 21.28) * mm, "end": v(0.16, 21.35) * mm});
            skLineSegment(sketch, "E416", {"start": v(0.16, 21.35) * mm, "end": v(-0.05, 21.38) * mm});
            skLineSegment(sketch, "E417", {"start": v(-0.05, 21.38) * mm, "end": v(-0.25, 21.35) * mm});
            skLineSegment(sketch, "E418", {"start": v(-0.25, 21.35) * mm, "end": v(-0.44, 21.27) * mm});
            skLineSegment(sketch, "E419", {"start": v(-0.44, 21.27) * mm, "end": v(-0.6, 21.14) * mm});
            skLineSegment(sketch, "E420", {"start": v(-0.6, 21.14) * mm, "end": v(-0.73, 20.98) * mm});
            skLineSegment(sketch, "E421", {"start": v(-0.73, 20.98) * mm, "end": v(-0.8, 20.79) * mm});
            skLineSegment(sketch, "E422", {"start": v(-0.8, 20.79) * mm, "end": v(-0.82, 20.62) * mm});
            skLineSegment(sketch, "E423", {"start": v(-0.82, 20.62) * mm, "end": v(-0.82, 20.43) * mm});
            skLineSegment(sketch, "E424", {"start": v(-0.82, 20.43) * mm, "end": v(-0.83, 20.24) * mm});
            skLineSegment(sketch, "E425", {"start": v(-0.83, 20.24) * mm, "end": v(-0.83, 20.05) * mm});
            skLineSegment(sketch, "E426", {"start": v(-0.83, 20.05) * mm, "end": v(-0.83, 19.86) * mm});
            skLineSegment(sketch, "E427", {"start": v(-0.83, 19.86) * mm, "end": v(-0.83, 19.67) * mm});
            skLineSegment(sketch, "E428", {"start": v(-0.83, 19.67) * mm, "end": v(-0.83, 19.48) * mm});
            skLineSegment(sketch, "E429", {"start": v(-0.83, 19.48) * mm, "end": v(-0.84, 19.3) * mm});
            skLineSegment(sketch, "E430", {"start": v(-0.84, 19.3) * mm, "end": v(-0.84, 19.1) * mm});
            skLineSegment(sketch, "E431", {"start": v(-0.84, 19.1) * mm, "end": v(-0.84, 18.9) * mm});
            skLineSegment(sketch, "E432", {"start": v(-0.84, 18.9) * mm, "end": v(-0.84, 18.72) * mm});
            skLineSegment(sketch, "E433", {"start": v(-0.84, 18.72) * mm, "end": v(-0.84, 18.53) * mm});
            skLineSegment(sketch, "E434", {"start": v(-0.84, 18.53) * mm, "end": v(-0.84, 18.34) * mm});
            skLineSegment(sketch, "E435", {"start": v(-0.84, 18.34) * mm, "end": v(-0.85, 18.17) * mm});
            skLineSegment(sketch, "E436", {"start": v(-0.85, 18.17) * mm, "end": v(-1.04, 18.16) * mm});
            skLineSegment(sketch, "E437", {"start": v(-1.04, 18.16) * mm, "end": v(-1.22, 18.16) * mm});
            skLineSegment(sketch, "E438", {"start": v(-1.22, 18.16) * mm, "end": v(-1.41, 18.15) * mm});
            skLineSegment(sketch, "E439", {"start": v(-1.41, 18.15) * mm, "end": v(-1.6, 18.14) * mm});
            skLineSegment(sketch, "E440", {"start": v(-1.6, 18.14) * mm, "end": v(-1.8, 18.13) * mm});
            skLineSegment(sketch, "E441", {"start": v(-1.8, 18.13) * mm, "end": v(-1.98, 18.12) * mm});
            skLineSegment(sketch, "E442", {"start": v(-1.98, 18.12) * mm, "end": v(-2.17, 18.11) * mm});
            skLineSegment(sketch, "E443", {"start": v(-2.17, 18.11) * mm, "end": v(-2.36, 18.1) * mm});
            skLineSegment(sketch, "E444", {"start": v(-2.36, 18.1) * mm, "end": v(-2.55, 18.1) * mm});
            skLineSegment(sketch, "E445", {"start": v(-2.55, 18.1) * mm, "end": v(-2.74, 18.08) * mm});
            skLineSegment(sketch, "E446", {"start": v(-2.74, 18.08) * mm, "end": v(-2.93, 18.07) * mm});
            skLineSegment(sketch, "E447", {"start": v(-2.93, 18.07) * mm, "end": v(-2.95, 18.26) * mm});
            skLineSegment(sketch, "E448", {"start": v(-2.95, 18.26) * mm, "end": v(-2.97, 18.45) * mm});
            skLineSegment(sketch, "E449", {"start": v(-2.97, 18.45) * mm, "end": v(-2.99, 18.64) * mm});
            skLineSegment(sketch, "E450", {"start": v(-2.99, 18.64) * mm, "end": v(-3, 18.83) * mm});
            skLineSegment(sketch, "E451", {"start": v(-3, 18.83) * mm, "end": v(-3.03, 19.02) * mm});
            skLineSegment(sketch, "E452", {"start": v(-3.03, 19.02) * mm, "end": v(-3.05, 19.21) * mm});
            skLineSegment(sketch, "E453", {"start": v(-3.05, 19.21) * mm, "end": v(-3.07, 19.4) * mm});
            skLineSegment(sketch, "E454", {"start": v(-3.07, 19.4) * mm, "end": v(-3.09, 19.59) * mm});
            skLineSegment(sketch, "E455", {"start": v(-3.09, 19.59) * mm, "end": v(-3.1, 19.78) * mm});
            skLineSegment(sketch, "E456", {"start": v(-3.1, 19.78) * mm, "end": v(-3.13, 19.97) * mm});
            skLineSegment(sketch, "E457", {"start": v(-3.13, 19.97) * mm, "end": v(-3.15, 20.16) * mm});
            skLineSegment(sketch, "E458", {"start": v(-3.15, 20.16) * mm, "end": v(-3.17, 20.35) * mm});
            skLineSegment(sketch, "E459", {"start": v(-3.17, 20.35) * mm, "end": v(-3.19, 20.55) * mm});
            skLineSegment(sketch, "E460", {"start": v(-3.19, 20.55) * mm, "end": v(-3.25, 20.75) * mm});
            skLineSegment(sketch, "E461", {"start": v(-3.25, 20.75) * mm, "end": v(-3.36, 20.92) * mm});
            skLineSegment(sketch, "E462", {"start": v(-3.36, 20.92) * mm, "end": v(-3.52, 21.06) * mm});
            skLineSegment(sketch, "E463", {"start": v(-3.52, 21.06) * mm, "end": v(-3.7, 21.15) * mm});
            skLineSegment(sketch, "E464", {"start": v(-3.7, 21.15) * mm, "end": v(-3.9, 21.2) * mm});
            skLineSegment(sketch, "E465", {"start": v(-3.9, 21.2) * mm, "end": v(-3.95, 21.2) * mm});
            skLineSegment(sketch, "E466", {"start": v(-3.95, 21.2) * mm, "end": v(-4.07, 21.19) * mm});
            skLineSegment(sketch, "E467", {"start": v(-4.07, 21.19) * mm, "end": v(-4.27, 21.13) * mm});
            skLineSegment(sketch, "E468", {"start": v(-4.27, 21.13) * mm, "end": v(-4.44, 21.02) * mm});
            skLineSegment(sketch, "E469", {"start": v(-4.44, 21.02) * mm, "end": v(-4.59, 20.88) * mm});
            skLineSegment(sketch, "E470", {"start": v(-4.59, 20.88) * mm, "end": v(-4.69, 20.7) * mm});
            skLineSegment(sketch, "E471", {"start": v(-4.69, 20.7) * mm, "end": v(-4.74, 20.5) * mm});
            skLineSegment(sketch, "E472", {"start": v(-4.74, 20.5) * mm, "end": v(-4.73, 20.29) * mm});
            skLineSegment(sketch, "E473", {"start": v(-4.73, 20.29) * mm, "end": v(-4.7, 20.1) * mm});
            skLineSegment(sketch, "E474", {"start": v(-4.7, 20.1) * mm, "end": v(-4.66, 19.91) * mm});
            skLineSegment(sketch, "E475", {"start": v(-4.66, 19.91) * mm, "end": v(-4.63, 19.73) * mm});
            skLineSegment(sketch, "E476", {"start": v(-4.63, 19.73) * mm, "end": v(-4.6, 19.54) * mm});
            skLineSegment(sketch, "E477", {"start": v(-4.6, 19.54) * mm, "end": v(-4.56, 19.35) * mm});
            skLineSegment(sketch, "E478", {"start": v(-4.56, 19.35) * mm, "end": v(-4.52, 19.16) * mm});
            skLineSegment(sketch, "E479", {"start": v(-4.52, 19.16) * mm, "end": v(-4.49, 18.98) * mm});
            skLineSegment(sketch, "E480", {"start": v(-4.49, 18.98) * mm, "end": v(-4.46, 18.8) * mm});
            skLineSegment(sketch, "E481", {"start": v(-4.46, 18.8) * mm, "end": v(-4.42, 18.6) * mm});
            skLineSegment(sketch, "E482", {"start": v(-4.42, 18.6) * mm, "end": v(-4.39, 18.41) * mm});
            skLineSegment(sketch, "E483", {"start": v(-4.39, 18.41) * mm, "end": v(-4.35, 18.23) * mm});
            skLineSegment(sketch, "E484", {"start": v(-4.35, 18.23) * mm, "end": v(-4.32, 18.04) * mm});
            skLineSegment(sketch, "E485", {"start": v(-4.32, 18.04) * mm, "end": v(-4.29, 17.88) * mm});
            skLineSegment(sketch, "E486", {"start": v(-4.29, 17.88) * mm, "end": v(-4.47, 17.83) * mm});
            skLineSegment(sketch, "E487", {"start": v(-4.47, 17.83) * mm, "end": v(-4.66, 17.79) * mm});
            skLineSegment(sketch, "E488", {"start": v(-4.66, 17.79) * mm, "end": v(-4.84, 17.74) * mm});
            skLineSegment(sketch, "E489", {"start": v(-4.84, 17.74) * mm, "end": v(-5.03, 17.7) * mm});
            skLineSegment(sketch, "E490", {"start": v(-5.03, 17.7) * mm, "end": v(-5.2, 17.66) * mm});
            skLineSegment(sketch, "E491", {"start": v(-5.2, 17.66) * mm, "end": v(-5.4, 17.61) * mm});
            skLineSegment(sketch, "E492", {"start": v(-5.4, 17.61) * mm, "end": v(-5.58, 17.57) * mm});
            skLineSegment(sketch, "E493", {"start": v(-5.58, 17.57) * mm, "end": v(-5.76, 17.52) * mm});
            skLineSegment(sketch, "E494", {"start": v(-5.76, 17.52) * mm, "end": v(-5.94, 17.48) * mm});
            skLineSegment(sketch, "E495", {"start": v(-5.94, 17.48) * mm, "end": v(-6.13, 17.43) * mm});
            skLineSegment(sketch, "E496", {"start": v(-6.13, 17.43) * mm, "end": v(-6.31, 17.39) * mm});
            skLineSegment(sketch, "E497", {"start": v(-6.31, 17.39) * mm, "end": v(-6.37, 17.57) * mm});
            skLineSegment(sketch, "E498", {"start": v(-6.37, 17.57) * mm, "end": v(-6.42, 17.75) * mm});
            skLineSegment(sketch, "E499", {"start": v(-6.42, 17.75) * mm, "end": v(-6.48, 17.93) * mm});
            skLineSegment(sketch, "E500", {"start": v(-6.48, 17.93) * mm, "end": v(-6.53, 18.12) * mm});
            skLineSegment(sketch, "E501", {"start": v(-6.53, 18.12) * mm, "end": v(-6.59, 18.3) * mm});
            skLineSegment(sketch, "E502", {"start": v(-6.59, 18.3) * mm, "end": v(-6.65, 18.48) * mm});
            skLineSegment(sketch, "E503", {"start": v(-6.65, 18.48) * mm, "end": v(-6.7, 18.66) * mm});
            skLineSegment(sketch, "E504", {"start": v(-6.7, 18.66) * mm, "end": v(-6.76, 18.84) * mm});
            skLineSegment(sketch, "E505", {"start": v(-6.76, 18.84) * mm, "end": v(-6.81, 19.03) * mm});
            skLineSegment(sketch, "E506", {"start": v(-6.81, 19.03) * mm, "end": v(-6.87, 19.2) * mm});
            skLineSegment(sketch, "E507", {"start": v(-6.87, 19.2) * mm, "end": v(-6.92, 19.39) * mm});
            skLineSegment(sketch, "E508", {"start": v(-6.92, 19.39) * mm, "end": v(-6.98, 19.57) * mm});
            skLineSegment(sketch, "E509", {"start": v(-6.98, 19.57) * mm, "end": v(-7.04, 19.77) * mm});
            skLineSegment(sketch, "E510", {"start": v(-7.04, 19.77) * mm, "end": v(-7.14, 19.95) * mm});
            skLineSegment(sketch, "E511", {"start": v(-7.14, 19.95) * mm, "end": v(-7.28, 20.1) * mm});
            skLineSegment(sketch, "E512", {"start": v(-7.28, 20.1) * mm, "end": v(-7.46, 20.2) * mm});
            skLineSegment(sketch, "E513", {"start": v(-7.46, 20.2) * mm, "end": v(-7.66, 20.26) * mm});
            skLineSegment(sketch, "E514", {"start": v(-7.66, 20.26) * mm, "end": v(-7.78, 20.27) * mm});
            skLineSegment(sketch, "E515", {"start": v(-7.78, 20.27) * mm, "end": v(-7.98, 20.24) * mm});
            skLineSegment(sketch, "E516", {"start": v(-7.98, 20.24) * mm, "end": v(-8.02, 20.23) * mm});
            skLineSegment(sketch, "E517", {"start": v(-8.02, 20.23) * mm, "end": v(-8.2, 20.13) * mm});
            skLineSegment(sketch, "E518", {"start": v(-8.2, 20.13) * mm, "end": v(-8.36, 20) * mm});
            skLineSegment(sketch, "E519", {"start": v(-8.36, 20) * mm, "end": v(-8.47, 19.82) * mm});
            skLineSegment(sketch, "E520", {"start": v(-8.47, 19.82) * mm, "end": v(-8.54, 19.63) * mm});
            skLineSegment(sketch, "E521", {"start": v(-8.54, 19.63) * mm, "end": v(-8.55, 19.42) * mm});
            skLineSegment(sketch, "E522", {"start": v(-8.55, 19.42) * mm, "end": v(-8.5, 19.22) * mm});
            skLineSegment(sketch, "E523", {"start": v(-8.5, 19.22) * mm, "end": v(-8.43, 19.04) * mm});
            skLineSegment(sketch, "E524", {"start": v(-8.43, 19.04) * mm, "end": v(-8.36, 18.87) * mm});
            skLineSegment(sketch, "E525", {"start": v(-8.36, 18.87) * mm, "end": v(-8.3, 18.69) * mm});
            skLineSegment(sketch, "E526", {"start": v(-8.3, 18.69) * mm, "end": v(-8.23, 18.51) * mm});
            skLineSegment(sketch, "E527", {"start": v(-8.23, 18.51) * mm, "end": v(-8.16, 18.33) * mm});
            skLineSegment(sketch, "E528", {"start": v(-8.16, 18.33) * mm, "end": v(-8.09, 18.15) * mm});
            skLineSegment(sketch, "E529", {"start": v(-8.09, 18.15) * mm, "end": v(-8.02, 17.98) * mm});
            skLineSegment(sketch, "E530", {"start": v(-8.02, 17.98) * mm, "end": v(-7.95, 17.8) * mm});
            skLineSegment(sketch, "E531", {"start": v(-7.95, 17.8) * mm, "end": v(-7.88, 17.62) * mm});
            skLineSegment(sketch, "E532", {"start": v(-7.88, 17.62) * mm, "end": v(-7.81, 17.45) * mm});
            skLineSegment(sketch, "E533", {"start": v(-7.81, 17.45) * mm, "end": v(-7.74, 17.27) * mm});
            skLineSegment(sketch, "E534", {"start": v(-7.74, 17.27) * mm, "end": v(-7.67, 17.09) * mm});
            skLineSegment(sketch, "E535", {"start": v(-7.67, 17.09) * mm, "end": v(-7.61, 16.94) * mm});
            skLineSegment(sketch, "E536", {"start": v(-7.61, 16.94) * mm, "end": v(-7.79, 16.86) * mm});
            skLineSegment(sketch, "E537", {"start": v(-7.79, 16.86) * mm, "end": v(-7.96, 16.78) * mm});
            skLineSegment(sketch, "E538", {"start": v(-7.96, 16.78) * mm, "end": v(-8.13, 16.7) * mm});
            skLineSegment(sketch, "E539", {"start": v(-8.13, 16.7) * mm, "end": v(-8.3, 16.62) * mm});
            skLineSegment(sketch, "E540", {"start": v(-8.3, 16.62) * mm, "end": v(-8.48, 16.54) * mm});
            skLineSegment(sketch, "E541", {"start": v(-8.48, 16.54) * mm, "end": v(-8.65, 16.47) * mm});
            skLineSegment(sketch, "E542", {"start": v(-8.65, 16.47) * mm, "end": v(-8.82, 16.39) * mm});
            skLineSegment(sketch, "E543", {"start": v(-8.82, 16.39) * mm, "end": v(-9, 16.3) * mm});
            skLineSegment(sketch, "E544", {"start": v(-9, 16.3) * mm, "end": v(-9.16, 16.23) * mm});
            skLineSegment(sketch, "E545", {"start": v(-9.16, 16.23) * mm, "end": v(-9.34, 16.15) * mm});
            skLineSegment(sketch, "E546", {"start": v(-9.34, 16.15) * mm, "end": v(-9.5, 16.07) * mm});
            skLineSegment(sketch, "E547", {"start": v(-9.5, 16.07) * mm, "end": v(-9.6, 16.24) * mm});
            skLineSegment(sketch, "E548", {"start": v(-9.6, 16.24) * mm, "end": v(-9.68, 16.4) * mm});
            skLineSegment(sketch, "E549", {"start": v(-9.68, 16.4) * mm, "end": v(-9.77, 16.58) * mm});
            skLineSegment(sketch, "E550", {"start": v(-9.77, 16.58) * mm, "end": v(-9.86, 16.74) * mm});
            skLineSegment(sketch, "E551", {"start": v(-9.86, 16.74) * mm, "end": v(-9.95, 16.91) * mm});
            skLineSegment(sketch, "E552", {"start": v(-9.95, 16.91) * mm, "end": v(-10.04, 17.08) * mm});
            skLineSegment(sketch, "E553", {"start": v(-10.04, 17.08) * mm, "end": v(-10.13, 17.25) * mm});
            skLineSegment(sketch, "E554", {"start": v(-10.13, 17.25) * mm, "end": v(-10.22, 17.42) * mm});
            skLineSegment(sketch, "E555", {"start": v(-10.22, 17.42) * mm, "end": v(-10.3, 17.59) * mm});
            skLineSegment(sketch, "E556", {"start": v(-10.3, 17.59) * mm, "end": v(-10.4, 17.76) * mm});
            skLineSegment(sketch, "E557", {"start": v(-10.4, 17.76) * mm, "end": v(-10.48, 17.92) * mm});
            skLineSegment(sketch, "E558", {"start": v(-10.48, 17.92) * mm, "end": v(-10.57, 18.1) * mm});
            skLineSegment(sketch, "E559", {"start": v(-10.57, 18.1) * mm, "end": v(-10.67, 18.27) * mm});
            skLineSegment(sketch, "E560", {"start": v(-10.67, 18.27) * mm, "end": v(-10.8, 18.43) * mm});
            skLineSegment(sketch, "E561", {"start": v(-10.8, 18.43) * mm, "end": v(-10.97, 18.55) * mm});
            skLineSegment(sketch, "E562", {"start": v(-10.97, 18.55) * mm, "end": v(-11.17, 18.62) * mm});
            skLineSegment(sketch, "E563", {"start": v(-11.17, 18.62) * mm, "end": v(-11.33, 18.64) * mm});
            skLineSegment(sketch, "E564", {"start": v(-11.33, 18.64) * mm, "end": v(-11.54, 18.62) * mm});
            skLineSegment(sketch, "E565", {"start": v(-11.54, 18.62) * mm, "end": v(-11.73, 18.54) * mm});
            skLineSegment(sketch, "E566", {"start": v(-11.73, 18.54) * mm, "end": v(-11.89, 18.41) * mm});
            skLineSegment(sketch, "E567", {"start": v(-11.89, 18.41) * mm, "end": v(-12.01, 18.25) * mm});
            skLineSegment(sketch, "E568", {"start": v(-12.01, 18.25) * mm, "end": v(-12.1, 18.05) * mm});
            skLineSegment(sketch, "E569", {"start": v(-12.1, 18.05) * mm, "end": v(-12.12, 17.85) * mm});
            skLineSegment(sketch, "E570", {"start": v(-12.12, 17.85) * mm, "end": v(-12.09, 17.65) * mm});
            skLineSegment(sketch, "E571", {"start": v(-12.09, 17.65) * mm, "end": v(-12, 17.46) * mm});
            skLineSegment(sketch, "E572", {"start": v(-12, 17.46) * mm, "end": v(-11.9, 17.3) * mm});
            skLineSegment(sketch, "E573", {"start": v(-11.9, 17.3) * mm, "end": v(-11.8, 17.14) * mm});
            skLineSegment(sketch, "E574", {"start": v(-11.8, 17.14) * mm, "end": v(-11.7, 16.97) * mm});
            skLineSegment(sketch, "E575", {"start": v(-11.7, 16.97) * mm, "end": v(-11.6, 16.81) * mm});
            skLineSegment(sketch, "E576", {"start": v(-11.6, 16.81) * mm, "end": v(-11.5, 16.65) * mm});
            skLineSegment(sketch, "E577", {"start": v(-11.5, 16.65) * mm, "end": v(-11.4, 16.49) * mm});
            skLineSegment(sketch, "E578", {"start": v(-11.4, 16.49) * mm, "end": v(-11.3, 16.33) * mm});
            skLineSegment(sketch, "E579", {"start": v(-11.3, 16.33) * mm, "end": v(-11.2, 16.17) * mm});
            skLineSegment(sketch, "E580", {"start": v(-11.2, 16.17) * mm, "end": v(-11.1, 16) * mm});
            skLineSegment(sketch, "E581", {"start": v(-11.1, 16) * mm, "end": v(-11, 15.85) * mm});
            skLineSegment(sketch, "E582", {"start": v(-11, 15.85) * mm, "end": v(-10.9, 15.68) * mm});
            skLineSegment(sketch, "E583", {"start": v(-10.9, 15.68) * mm, "end": v(-10.79, 15.52) * mm});
            skLineSegment(sketch, "E584", {"start": v(-10.79, 15.52) * mm, "end": v(-10.7, 15.38) * mm});
            skLineSegment(sketch, "E585", {"start": v(-10.7, 15.38) * mm, "end": v(-10.85, 15.27) * mm});
            skLineSegment(sketch, "E586", {"start": v(-10.85, 15.27) * mm, "end": v(-11, 15.16) * mm});
            skLineSegment(sketch, "E587", {"start": v(-11, 15.16) * mm, "end": v(-11.16, 15.05) * mm});
            skLineSegment(sketch, "E588", {"start": v(-11.16, 15.05) * mm, "end": v(-11.32, 14.94) * mm});
            skLineSegment(sketch, "E589", {"start": v(-11.32, 14.94) * mm, "end": v(-11.47, 14.83) * mm});
            skLineSegment(sketch, "E590", {"start": v(-11.47, 14.83) * mm, "end": v(-11.63, 14.72) * mm});
            skLineSegment(sketch, "E591", {"start": v(-11.63, 14.72) * mm, "end": v(-11.78, 14.61) * mm});
            skLineSegment(sketch, "E592", {"start": v(-11.78, 14.61) * mm, "end": v(-11.93, 14.5) * mm});
            skLineSegment(sketch, "E593", {"start": v(-11.93, 14.5) * mm, "end": v(-12.09, 14.4) * mm});
            skLineSegment(sketch, "E594", {"start": v(-12.09, 14.4) * mm, "end": v(-12.24, 14.29) * mm});
            skLineSegment(sketch, "E595", {"start": v(-12.24, 14.29) * mm, "end": v(-12.4, 14.18) * mm});
            skLineSegment(sketch, "E596", {"start": v(-12.4, 14.18) * mm, "end": v(-12.52, 14.32) * mm});
            skLineSegment(sketch, "E597", {"start": v(-12.52, 14.32) * mm, "end": v(-12.63, 14.47) * mm});
            skLineSegment(sketch, "E598", {"start": v(-12.63, 14.47) * mm, "end": v(-12.75, 14.62) * mm});
            skLineSegment(sketch, "E599", {"start": v(-12.75, 14.62) * mm, "end": v(-12.87, 14.77) * mm});
            skLineSegment(sketch, "E600", {"start": v(-12.87, 14.77) * mm, "end": v(-13, 14.92) * mm});
            skLineSegment(sketch, "E601", {"start": v(-13, 14.92) * mm, "end": v(-13.11, 15.07) * mm});
            skLineSegment(sketch, "E602", {"start": v(-13.11, 15.07) * mm, "end": v(-13.23, 15.21) * mm});
            skLineSegment(sketch, "E603", {"start": v(-13.23, 15.21) * mm, "end": v(-13.35, 15.36) * mm});
            skLineSegment(sketch, "E604", {"start": v(-13.35, 15.36) * mm, "end": v(-13.47, 15.51) * mm});
            skLineSegment(sketch, "E605", {"start": v(-13.47, 15.51) * mm, "end": v(-13.59, 15.66) * mm});
            skLineSegment(sketch, "E606", {"start": v(-13.59, 15.66) * mm, "end": v(-13.7, 15.8) * mm});
            skLineSegment(sketch, "E607", {"start": v(-13.7, 15.8) * mm, "end": v(-13.83, 15.96) * mm});
            skLineSegment(sketch, "E608", {"start": v(-13.83, 15.96) * mm, "end": v(-13.96, 16.12) * mm});
            skLineSegment(sketch, "E609", {"start": v(-13.96, 16.12) * mm, "end": v(-14.12, 16.25) * mm});
            skLineSegment(sketch, "E610", {"start": v(-14.12, 16.25) * mm, "end": v(-14.3, 16.33) * mm});
            skLineSegment(sketch, "E611", {"start": v(-14.3, 16.33) * mm, "end": v(-14.5, 16.37) * mm});
            skLineSegment(sketch, "E612", {"start": v(-14.5, 16.37) * mm, "end": v(-14.55, 16.37) * mm});
            skLineSegment(sketch, "E613", {"start": v(-14.55, 16.37) * mm, "end": v(-14.75, 16.33) * mm});
            skLineSegment(sketch, "E614", {"start": v(-14.75, 16.33) * mm, "end": v(-14.94, 16.25) * mm});
            skLineSegment(sketch, "E615", {"start": v(-14.94, 16.25) * mm, "end": v(-15.04, 16.18) * mm});
            skLineSegment(sketch, "E616", {"start": v(-15.04, 16.18) * mm, "end": v(-15.18, 16.02) * mm});
            skLineSegment(sketch, "E617", {"start": v(-15.18, 16.02) * mm, "end": v(-15.27, 15.84) * mm});
            skLineSegment(sketch, "E618", {"start": v(-15.27, 15.84) * mm, "end": v(-15.3, 15.63) * mm});
            skLineSegment(sketch, "E619", {"start": v(-15.3, 15.63) * mm, "end": v(-15.3, 15.43) * mm});
            skLineSegment(sketch, "E620", {"start": v(-15.3, 15.43) * mm, "end": v(-15.23, 15.23) * mm});
            skLineSegment(sketch, "E621", {"start": v(-15.23, 15.23) * mm, "end": v(-15.11, 15.06) * mm});
            skLineSegment(sketch, "E622", {"start": v(-15.11, 15.06) * mm, "end": v(-14.98, 14.92) * mm});
            skLineSegment(sketch, "E623", {"start": v(-14.98, 14.92) * mm, "end": v(-14.85, 14.79) * mm});
            skLineSegment(sketch, "E624", {"start": v(-14.85, 14.79) * mm, "end": v(-14.72, 14.65) * mm});
            skLineSegment(sketch, "E625", {"start": v(-14.72, 14.65) * mm, "end": v(-14.6, 14.5) * mm});
            skLineSegment(sketch, "E626", {"start": v(-14.6, 14.5) * mm, "end": v(-14.46, 14.37) * mm});
            skLineSegment(sketch, "E627", {"start": v(-14.46, 14.37) * mm, "end": v(-14.33, 14.23) * mm});
            skLineSegment(sketch, "E628", {"start": v(-14.33, 14.23) * mm, "end": v(-14.2, 14.09) * mm});
            skLineSegment(sketch, "E629", {"start": v(-14.2, 14.09) * mm, "end": v(-14.07, 13.95) * mm});
            skLineSegment(sketch, "E630", {"start": v(-14.07, 13.95) * mm, "end": v(-13.94, 13.81) * mm});
            skLineSegment(sketch, "E631", {"start": v(-13.94, 13.81) * mm, "end": v(-13.81, 13.67) * mm});
            skLineSegment(sketch, "E632", {"start": v(-13.81, 13.67) * mm, "end": v(-13.68, 13.53) * mm});
            skLineSegment(sketch, "E633", {"start": v(-13.68, 13.53) * mm, "end": v(-13.55, 13.4) * mm});
            skLineSegment(sketch, "E634", {"start": v(-13.55, 13.4) * mm, "end": v(-13.44, 13.27) * mm});
            skLineSegment(sketch, "E635", {"start": v(-13.44, 13.27) * mm, "end": v(-13.57, 13.14) * mm});
            skLineSegment(sketch, "E636", {"start": v(-13.57, 13.14) * mm, "end": v(-13.7, 13) * mm});
            skLineSegment(sketch, "E637", {"start": v(-13.7, 13) * mm, "end": v(-13.83, 12.86) * mm});
            skLineSegment(sketch, "E638", {"start": v(-13.83, 12.86) * mm, "end": v(-13.96, 12.73) * mm});
            skLineSegment(sketch, "E639", {"start": v(-13.96, 12.73) * mm, "end": v(-14.1, 12.59) * mm});
            skLineSegment(sketch, "E640", {"start": v(-14.1, 12.59) * mm, "end": v(-14.22, 12.45) * mm});
            skLineSegment(sketch, "E641", {"start": v(-14.22, 12.45) * mm, "end": v(-14.35, 12.31) * mm});
            skLineSegment(sketch, "E642", {"start": v(-14.35, 12.31) * mm, "end": v(-14.48, 12.18) * mm});
            skLineSegment(sketch, "E643", {"start": v(-14.48, 12.18) * mm, "end": v(-14.61, 12.04) * mm});
            skLineSegment(sketch, "E644", {"start": v(-14.61, 12.04) * mm, "end": v(-14.74, 11.9) * mm});
            skLineSegment(sketch, "E645", {"start": v(-14.74, 11.9) * mm, "end": v(-14.87, 11.77) * mm});
            skLineSegment(sketch, "E646", {"start": v(-14.87, 11.77) * mm, "end": v(-15.02, 11.89) * mm});
            skLineSegment(sketch, "E647", {"start": v(-15.02, 11.89) * mm, "end": v(-15.16, 12.01) * mm});
            skLineSegment(sketch, "E648", {"start": v(-15.16, 12.01) * mm, "end": v(-15.3, 12.14) * mm});
            skLineSegment(sketch, "E649", {"start": v(-15.3, 12.14) * mm, "end": v(-15.45, 12.26) * mm});
            skLineSegment(sketch, "E650", {"start": v(-15.45, 12.26) * mm, "end": v(-15.6, 12.38) * mm});
            skLineSegment(sketch, "E651", {"start": v(-15.6, 12.38) * mm, "end": v(-15.75, 12.5) * mm});
            skLineSegment(sketch, "E652", {"start": v(-15.75, 12.5) * mm, "end": v(-15.89, 12.63) * mm});
            skLineSegment(sketch, "E653", {"start": v(-15.89, 12.63) * mm, "end": v(-16.03, 12.75) * mm});
            skLineSegment(sketch, "E654", {"start": v(-16.03, 12.75) * mm, "end": v(-16.18, 12.88) * mm});
            skLineSegment(sketch, "E655", {"start": v(-16.18, 12.88) * mm, "end": v(-16.32, 13) * mm});
            skLineSegment(sketch, "E656", {"start": v(-16.32, 13) * mm, "end": v(-16.47, 13.12) * mm});
            skLineSegment(sketch, "E657", {"start": v(-16.47, 13.12) * mm, "end": v(-16.62, 13.25) * mm});
            skLineSegment(sketch, "E658", {"start": v(-16.62, 13.25) * mm, "end": v(-16.77, 13.38) * mm});
            skLineSegment(sketch, "E659", {"start": v(-16.77, 13.38) * mm, "end": v(-16.95, 13.48) * mm});
            skLineSegment(sketch, "E660", {"start": v(-16.95, 13.48) * mm, "end": v(-17.16, 13.53) * mm});
            skLineSegment(sketch, "E661", {"start": v(-17.16, 13.53) * mm, "end": v(-17.24, 13.53) * mm});
            skLineSegment(sketch, "E662", {"start": v(-17.24, 13.53) * mm, "end": v(-17.44, 13.5) * mm});
            skLineSegment(sketch, "E663", {"start": v(-17.44, 13.5) * mm, "end": v(-17.63, 13.42) * mm});
            skLineSegment(sketch, "E664", {"start": v(-17.63, 13.42) * mm, "end": v(-17.8, 13.3) * mm});
            skLineSegment(sketch, "E665", {"start": v(-17.8, 13.3) * mm, "end": v(-17.85, 13.23) * mm});
            skLineSegment(sketch, "E666", {"start": v(-17.85, 13.23) * mm, "end": v(-17.95, 13.05) * mm});
            skLineSegment(sketch, "E667", {"start": v(-17.95, 13.05) * mm, "end": v(-18, 12.85) * mm});
            skLineSegment(sketch, "E668", {"start": v(-18, 12.85) * mm, "end": v(-18.01, 12.65) * mm});
            skLineSegment(sketch, "E669", {"start": v(-18.01, 12.65) * mm, "end": v(-17.96, 12.45) * mm});
            skLineSegment(sketch, "E670", {"start": v(-17.96, 12.45) * mm, "end": v(-17.85, 12.27) * mm});
            skLineSegment(sketch, "E671", {"start": v(-17.85, 12.27) * mm, "end": v(-17.7, 12.12) * mm});
            skLineSegment(sketch, "E672", {"start": v(-17.7, 12.12) * mm, "end": v(-17.55, 12.01) * mm});
            skLineSegment(sketch, "E673", {"start": v(-17.55, 12.01) * mm, "end": v(-17.4, 11.9) * mm});
            skLineSegment(sketch, "E674", {"start": v(-17.4, 11.9) * mm, "end": v(-17.24, 11.79) * mm});
            skLineSegment(sketch, "E675", {"start": v(-17.24, 11.79) * mm, "end": v(-17.1, 11.68) * mm});
            skLineSegment(sketch, "E676", {"start": v(-17.1, 11.68) * mm, "end": v(-16.94, 11.57) * mm});
            skLineSegment(sketch, "E677", {"start": v(-16.94, 11.57) * mm, "end": v(-16.78, 11.45) * mm});
            skLineSegment(sketch, "E678", {"start": v(-16.78, 11.45) * mm, "end": v(-16.63, 11.34) * mm});
            skLineSegment(sketch, "E679", {"start": v(-16.63, 11.34) * mm, "end": v(-16.48, 11.23) * mm});
            skLineSegment(sketch, "E680", {"start": v(-16.48, 11.23) * mm, "end": v(-16.32, 11.12) * mm});
            skLineSegment(sketch, "E681", {"start": v(-16.32, 11.12) * mm, "end": v(-16.17, 11) * mm});
            skLineSegment(sketch, "E682", {"start": v(-16.17, 11) * mm, "end": v(-16.01, 10.9) * mm});
            skLineSegment(sketch, "E683", {"start": v(-16.01, 10.9) * mm, "end": v(-15.86, 10.78) * mm});
            skLineSegment(sketch, "E684", {"start": v(-15.86, 10.78) * mm, "end": v(-15.73, 10.68) * mm});
            skLineSegment(sketch, "E685", {"start": v(-15.73, 10.68) * mm, "end": v(-15.83, 10.53) * mm});
            skLineSegment(sketch, "E686", {"start": v(-15.83, 10.53) * mm, "end": v(-15.93, 10.37) * mm});
            skLineSegment(sketch, "E687", {"start": v(-15.93, 10.37) * mm, "end": v(-16.03, 10.2) * mm});
            skLineSegment(sketch, "E688", {"start": v(-16.03, 10.2) * mm, "end": v(-16.14, 10.05) * mm});
            skLineSegment(sketch, "E689", {"start": v(-16.14, 10.05) * mm, "end": v(-16.24, 9.89) * mm});
            skLineSegment(sketch, "E690", {"start": v(-16.24, 9.89) * mm, "end": v(-16.34, 9.73) * mm});
            skLineSegment(sketch, "E691", {"start": v(-16.34, 9.73) * mm, "end": v(-16.44, 9.57) * mm});
            skLineSegment(sketch, "E692", {"start": v(-16.44, 9.57) * mm, "end": v(-16.54, 9.41) * mm});
            skLineSegment(sketch, "E693", {"start": v(-16.54, 9.41) * mm, "end": v(-16.65, 9.25) * mm});
            skLineSegment(sketch, "E694", {"start": v(-16.65, 9.25) * mm, "end": v(-16.75, 9.1) * mm});
            skLineSegment(sketch, "E695", {"start": v(-16.75, 9.1) * mm, "end": v(-16.85, 8.93) * mm});
            skLineSegment(sketch, "E696", {"start": v(-16.85, 8.93) * mm, "end": v(-17.02, 9.03) * mm});
            skLineSegment(sketch, "E697", {"start": v(-17.02, 9.03) * mm, "end": v(-17.18, 9.12) * mm});
            skLineSegment(sketch, "E698", {"start": v(-17.18, 9.12) * mm, "end": v(-17.35, 9.21) * mm});
            skLineSegment(sketch, "E699", {"start": v(-17.35, 9.21) * mm, "end": v(-17.51, 9.3) * mm});
            skLineSegment(sketch, "E700", {"start": v(-17.51, 9.3) * mm, "end": v(-17.68, 9.4) * mm});
            skLineSegment(sketch, "E701", {"start": v(-17.68, 9.4) * mm, "end": v(-17.85, 9.5) * mm});
            skLineSegment(sketch, "E702", {"start": v(-17.85, 9.5) * mm, "end": v(-18.01, 9.59) * mm});
            skLineSegment(sketch, "E703", {"start": v(-18.01, 9.59) * mm, "end": v(-18.18, 9.68) * mm});
            skLineSegment(sketch, "E704", {"start": v(-18.18, 9.68) * mm, "end": v(-18.34, 9.78) * mm});
            skLineSegment(sketch, "E705", {"start": v(-18.34, 9.78) * mm, "end": v(-18.5, 9.87) * mm});
            skLineSegment(sketch, "E706", {"start": v(-18.5, 9.87) * mm, "end": v(-18.67, 9.96) * mm});
            skLineSegment(sketch, "E707", {"start": v(-18.67, 9.96) * mm, "end": v(-18.84, 10.06) * mm});
            skLineSegment(sketch, "E708", {"start": v(-18.84, 10.06) * mm, "end": v(-19.02, 10.16) * mm});
            skLineSegment(sketch, "E709", {"start": v(-19.02, 10.16) * mm, "end": v(-19.22, 10.22) * mm});
            skLineSegment(sketch, "E710", {"start": v(-19.22, 10.22) * mm, "end": v(-19.34, 10.23) * mm});
            skLineSegment(sketch, "E711", {"start": v(-19.34, 10.23) * mm, "end": v(-19.55, 10.2) * mm});
            skLineSegment(sketch, "E712", {"start": v(-19.55, 10.2) * mm, "end": v(-19.74, 10.13) * mm});
            skLineSegment(sketch, "E713", {"start": v(-19.74, 10.13) * mm, "end": v(-19.9, 10) * mm});
            skLineSegment(sketch, "E714", {"start": v(-19.9, 10) * mm, "end": v(-20.03, 9.84) * mm});
            skLineSegment(sketch, "E715", {"start": v(-20.03, 9.84) * mm, "end": v(-20.05, 9.8) * mm});
            skLineSegment(sketch, "E716", {"start": v(-20.05, 9.8) * mm, "end": v(-20.12, 9.61) * mm});
            skLineSegment(sketch, "E717", {"start": v(-20.12, 9.61) * mm, "end": v(-20.14, 9.4) * mm});
            skLineSegment(sketch, "E718", {"start": v(-20.14, 9.4) * mm, "end": v(-20.1, 9.2) * mm});
            skLineSegment(sketch, "E719", {"start": v(-20.1, 9.2) * mm, "end": v(-20, 9.02) * mm});
            skLineSegment(sketch, "E720", {"start": v(-20, 9.02) * mm, "end": v(-19.87, 8.86) * mm});
            skLineSegment(sketch, "E721", {"start": v(-19.87, 8.86) * mm, "end": v(-19.7, 8.75) * mm});
            skLineSegment(sketch, "E722", {"start": v(-19.7, 8.75) * mm, "end": v(-19.53, 8.67) * mm});
            skLineSegment(sketch, "E723", {"start": v(-19.53, 8.67) * mm, "end": v(-19.36, 8.59) * mm});
            skLineSegment(sketch, "E724", {"start": v(-19.36, 8.59) * mm, "end": v(-19.18, 8.5) * mm});
            skLineSegment(sketch, "E725", {"start": v(-19.18, 8.5) * mm, "end": v(-19.01, 8.42) * mm});
            skLineSegment(sketch, "E726", {"start": v(-19.01, 8.42) * mm, "end": v(-18.84, 8.34) * mm});
            skLineSegment(sketch, "E727", {"start": v(-18.84, 8.34) * mm, "end": v(-18.67, 8.26) * mm});
            skLineSegment(sketch, "E728", {"start": v(-18.67, 8.26) * mm, "end": v(-18.5, 8.18) * mm});
            skLineSegment(sketch, "E729", {"start": v(-18.5, 8.18) * mm, "end": v(-18.32, 8.1) * mm});
            skLineSegment(sketch, "E730", {"start": v(-18.32, 8.1) * mm, "end": v(-18.15, 8.02) * mm});
            skLineSegment(sketch, "E731", {"start": v(-18.15, 8.02) * mm, "end": v(-17.98, 7.94) * mm});
            skLineSegment(sketch, "E732", {"start": v(-17.98, 7.94) * mm, "end": v(-17.8, 7.86) * mm});
            skLineSegment(sketch, "E733", {"start": v(-17.8, 7.86) * mm, "end": v(-17.63, 7.78) * mm});
            skLineSegment(sketch, "E734", {"start": v(-17.63, 7.78) * mm, "end": v(-17.48, 7.7) * mm});
            skLineSegment(sketch, "E735", {"start": v(-17.48, 7.7) * mm, "end": v(-17.55, 7.53) * mm});
            skLineSegment(sketch, "E736", {"start": v(-17.55, 7.53) * mm, "end": v(-17.62, 7.36) * mm});
            skLineSegment(sketch, "E737", {"start": v(-17.62, 7.36) * mm, "end": v(-17.7, 7.18) * mm});
            skLineSegment(sketch, "E738", {"start": v(-17.7, 7.18) * mm, "end": v(-17.76, 7) * mm});
            skLineSegment(sketch, "E739", {"start": v(-17.76, 7) * mm, "end": v(-17.83, 6.83) * mm});
            skLineSegment(sketch, "E740", {"start": v(-17.83, 6.83) * mm, "end": v(-17.9, 6.65) * mm});
            skLineSegment(sketch, "E741", {"start": v(-17.9, 6.65) * mm, "end": v(-17.97, 6.48) * mm});
            skLineSegment(sketch, "E742", {"start": v(-17.97, 6.48) * mm, "end": v(-18.05, 6.3) * mm});
            skLineSegment(sketch, "E743", {"start": v(-18.05, 6.3) * mm, "end": v(-18.12, 6.13) * mm});
            skLineSegment(sketch, "E744", {"start": v(-18.12, 6.13) * mm, "end": v(-18.19, 5.95) * mm});
            skLineSegment(sketch, "E745", {"start": v(-18.19, 5.95) * mm, "end": v(-18.26, 5.78) * mm});
            skLineSegment(sketch, "E746", {"start": v(-18.26, 5.78) * mm, "end": v(-18.44, 5.84) * mm});
            skLineSegment(sketch, "E747", {"start": v(-18.44, 5.84) * mm, "end": v(-18.62, 5.9) * mm});
            skLineSegment(sketch, "E748", {"start": v(-18.62, 5.9) * mm, "end": v(-18.8, 5.96) * mm});
            skLineSegment(sketch, "E749", {"start": v(-18.8, 5.96) * mm, "end": v(-18.98, 6.02) * mm});
            skLineSegment(sketch, "E750", {"start": v(-18.98, 6.02) * mm, "end": v(-19.16, 6.08) * mm});
            skLineSegment(sketch, "E751", {"start": v(-19.16, 6.08) * mm, "end": v(-19.34, 6.14) * mm});
            skLineSegment(sketch, "E752", {"start": v(-19.34, 6.14) * mm, "end": v(-19.52, 6.2) * mm});
            skLineSegment(sketch, "E753", {"start": v(-19.52, 6.2) * mm, "end": v(-19.7, 6.26) * mm});
            skLineSegment(sketch, "E754", {"start": v(-19.7, 6.26) * mm, "end": v(-19.88, 6.32) * mm});
            skLineSegment(sketch, "E755", {"start": v(-19.88, 6.32) * mm, "end": v(-20.06, 6.38) * mm});
            skLineSegment(sketch, "E756", {"start": v(-20.06, 6.38) * mm, "end": v(-20.24, 6.44) * mm});
            skLineSegment(sketch, "E757", {"start": v(-20.24, 6.44) * mm, "end": v(-20.42, 6.5) * mm});
            skLineSegment(sketch, "E758", {"start": v(-20.42, 6.5) * mm, "end": v(-20.62, 6.57) * mm});
            skLineSegment(sketch, "E759", {"start": v(-20.62, 6.57) * mm, "end": v(-20.82, 6.6) * mm});
            skLineSegment(sketch, "E760", {"start": v(-20.82, 6.6) * mm, "end": v(-21.03, 6.56) * mm});
            skLineSegment(sketch, "E761", {"start": v(-21.03, 6.56) * mm, "end": v(-21.22, 6.48) * mm});
            skLineSegment(sketch, "E762", {"start": v(-21.22, 6.48) * mm, "end": v(-21.38, 6.35) * mm});
            skLineSegment(sketch, "E763", {"start": v(-21.38, 6.35) * mm, "end": v(-21.5, 6.18) * mm});
            skLineSegment(sketch, "E764", {"start": v(-21.5, 6.18) * mm, "end": v(-21.56, 6.03) * mm});
            skLineSegment(sketch, "E765", {"start": v(-21.56, 6.03) * mm, "end": v(-21.6, 5.82) * mm});
            skLineSegment(sketch, "E766", {"start": v(-21.6, 5.82) * mm, "end": v(-21.57, 5.62) * mm});
            skLineSegment(sketch, "E767", {"start": v(-21.57, 5.62) * mm, "end": v(-21.5, 5.43) * mm});
            skLineSegment(sketch, "E768", {"start": v(-21.5, 5.43) * mm, "end": v(-21.37, 5.26) * mm});
            skLineSegment(sketch, "E769", {"start": v(-21.37, 5.26) * mm, "end": v(-21.2, 5.14) * mm});
            skLineSegment(sketch, "E770", {"start": v(-21.2, 5.14) * mm, "end": v(-21.02, 5.05) * mm});
            skLineSegment(sketch, "E771", {"start": v(-21.02, 5.05) * mm, "end": v(-20.83, 5) * mm});
            skLineSegment(sketch, "E772", {"start": v(-20.83, 5) * mm, "end": v(-20.65, 4.96) * mm});
            skLineSegment(sketch, "E773", {"start": v(-20.65, 4.96) * mm, "end": v(-20.46, 4.91) * mm});
            skLineSegment(sketch, "E774", {"start": v(-20.46, 4.91) * mm, "end": v(-20.28, 4.87) * mm});
            skLineSegment(sketch, "E775", {"start": v(-20.28, 4.87) * mm, "end": v(-20.1, 4.82) * mm});
            skLineSegment(sketch, "E776", {"start": v(-20.1, 4.82) * mm, "end": v(-19.91, 4.77) * mm});
            skLineSegment(sketch, "E777", {"start": v(-19.91, 4.77) * mm, "end": v(-19.73, 4.73) * mm});
            skLineSegment(sketch, "E778", {"start": v(-19.73, 4.73) * mm, "end": v(-19.54, 4.68) * mm});
            skLineSegment(sketch, "E779", {"start": v(-19.54, 4.68) * mm, "end": v(-19.36, 4.63) * mm});
            skLineSegment(sketch, "E780", {"start": v(-19.36, 4.63) * mm, "end": v(-19.17, 4.59) * mm});
            skLineSegment(sketch, "E781", {"start": v(-19.17, 4.59) * mm, "end": v(-18.99, 4.54) * mm});
            skLineSegment(sketch, "E782", {"start": v(-18.99, 4.54) * mm, "end": v(-18.8, 4.5) * mm});
            skLineSegment(sketch, "E783", {"start": v(-18.8, 4.5) * mm, "end": v(-18.64, 4.45) * mm});
            skLineSegment(sketch, "E784", {"start": v(-18.64, 4.45) * mm, "end": v(-18.68, 4.27) * mm});
            skLineSegment(sketch, "E785", {"start": v(-18.68, 4.27) * mm, "end": v(-18.72, 4.08) * mm});
            skLineSegment(sketch, "E786", {"start": v(-18.72, 4.08) * mm, "end": v(-18.75, 3.9) * mm});
            skLineSegment(sketch, "E787", {"start": v(-18.75, 3.9) * mm, "end": v(-18.79, 3.71) * mm});
            skLineSegment(sketch, "E788", {"start": v(-18.79, 3.71) * mm, "end": v(-18.82, 3.53) * mm});
            skLineSegment(sketch, "E789", {"start": v(-18.82, 3.53) * mm, "end": v(-18.86, 3.34) * mm});
            skLineSegment(sketch, "E790", {"start": v(-18.86, 3.34) * mm, "end": v(-18.9, 3.15) * mm});
            skLineSegment(sketch, "E791", {"start": v(-18.9, 3.15) * mm, "end": v(-18.93, 2.97) * mm});
            skLineSegment(sketch, "E792", {"start": v(-18.93, 2.97) * mm, "end": v(-18.97, 2.78) * mm});
            skLineSegment(sketch, "E793", {"start": v(-18.97, 2.78) * mm, "end": v(-19, 2.6) * mm});
            skLineSegment(sketch, "E794", {"start": v(-19, 2.6) * mm, "end": v(-19.04, 2.41) * mm});
            skLineSegment(sketch, "E795", {"start": v(-19.04, 2.41) * mm, "end": v(-19.23, 2.44) * mm});
            skLineSegment(sketch, "E796", {"start": v(-19.23, 2.44) * mm, "end": v(-19.41, 2.46) * mm});
            skLineSegment(sketch, "E797", {"start": v(-19.41, 2.46) * mm, "end": v(-19.6, 2.49) * mm});
            skLineSegment(sketch, "E798", {"start": v(-19.6, 2.49) * mm, "end": v(-19.8, 2.51) * mm});
            skLineSegment(sketch, "E799", {"start": v(-19.8, 2.51) * mm, "end": v(-19.98, 2.54) * mm});
            skLineSegment(sketch, "E800", {"start": v(-19.98, 2.54) * mm, "end": v(-20.17, 2.56) * mm});
            skLineSegment(sketch, "E801", {"start": v(-20.17, 2.56) * mm, "end": v(-20.36, 2.59) * mm});
            skLineSegment(sketch, "E802", {"start": v(-20.36, 2.59) * mm, "end": v(-20.55, 2.61) * mm});
            skLineSegment(sketch, "E803", {"start": v(-20.55, 2.61) * mm, "end": v(-20.74, 2.64) * mm});
            skLineSegment(sketch, "E804", {"start": v(-20.74, 2.64) * mm, "end": v(-20.92, 2.66) * mm});
            skLineSegment(sketch, "E805", {"start": v(-20.92, 2.66) * mm, "end": v(-21.11, 2.69) * mm});
            skLineSegment(sketch, "E806", {"start": v(-21.11, 2.69) * mm, "end": v(-21.3, 2.71) * mm});
            skLineSegment(sketch, "E807", {"start": v(-21.3, 2.71) * mm, "end": v(-21.5, 2.74) * mm});
            skLineSegment(sketch, "E808", {"start": v(-21.5, 2.74) * mm, "end": v(-21.55, 2.74) * mm});
            skLineSegment(sketch, "E809", {"start": v(-21.55, 2.74) * mm, "end": v(-21.75, 2.71) * mm});
            skLineSegment(sketch, "E810", {"start": v(-21.75, 2.71) * mm, "end": v(-21.94, 2.64) * mm});
            skLineSegment(sketch, "E811", {"start": v(-21.94, 2.64) * mm, "end": v(-22.1, 2.51) * mm});
            skLineSegment(sketch, "E812", {"start": v(-22.1, 2.51) * mm, "end": v(-22.23, 2.35) * mm});
            skLineSegment(sketch, "E813", {"start": v(-22.23, 2.35) * mm, "end": v(-22.31, 2.16) * mm});
            skLineSegment(sketch, "E814", {"start": v(-22.31, 2.16) * mm, "end": v(-22.34, 1.95) * mm});
            skLineSegment(sketch, "E815", {"start": v(-22.34, 1.95) * mm, "end": v(-22.3, 1.75) * mm});
            skLineSegment(sketch, "E816", {"start": v(-22.3, 1.75) * mm, "end": v(-22.22, 1.56) * mm});
            skLineSegment(sketch, "E817", {"start": v(-22.22, 1.56) * mm, "end": v(-22.1, 1.4) * mm});
            skLineSegment(sketch, "E818", {"start": v(-22.1, 1.4) * mm, "end": v(-21.93, 1.27) * mm});
            skLineSegment(sketch, "E819", {"start": v(-21.93, 1.27) * mm, "end": v(-21.74, 1.2) * mm});
            skLineSegment(sketch, "E820", {"start": v(-21.74, 1.2) * mm, "end": v(-21.53, 1.17) * mm});
            skLineSegment(sketch, "E821", {"start": v(-21.53, 1.17) * mm, "end": v(-21.34, 1.16) * mm});
            skLineSegment(sketch, "E822", {"start": v(-21.34, 1.16) * mm, "end": v(-21.15, 1.15) * mm});
            skLineSegment(sketch, "E823", {"start": v(-21.15, 1.15) * mm, "end": v(-20.96, 1.14) * mm});
            skLineSegment(sketch, "E824", {"start": v(-20.96, 1.14) * mm, "end": v(-20.77, 1.13) * mm});
            skLineSegment(sketch, "E825", {"start": v(-20.77, 1.13) * mm, "end": v(-20.58, 1.12) * mm});
            skLineSegment(sketch, "E826", {"start": v(-20.58, 1.12) * mm, "end": v(-20.4, 1.1) * mm});
            skLineSegment(sketch, "E827", {"start": v(-20.4, 1.1) * mm, "end": v(-20.2, 1.1) * mm});
            skLineSegment(sketch, "E828", {"start": v(-20.2, 1.1) * mm, "end": v(-20.01, 1.09) * mm});
            skLineSegment(sketch, "E829", {"start": v(-20.01, 1.09) * mm, "end": v(-19.82, 1.08) * mm});
            skLineSegment(sketch, "E830", {"start": v(-19.82, 1.08) * mm, "end": v(-19.63, 1.07) * mm});
            skLineSegment(sketch, "E831", {"start": v(-19.63, 1.07) * mm, "end": v(-19.44, 1.05) * mm});
            skLineSegment(sketch, "E832", {"start": v(-19.44, 1.05) * mm, "end": v(-19.25, 1.04) * mm});
            skLineSegment(sketch, "E833", {"start": v(-19.25, 1.04) * mm, "end": v(-19.17, 1.04) * mm});
            skLineSegment(sketch, "E834", {"start": v(-19.17, 1.04) * mm, "end": v(-19.17, 0.85) * mm});
            skLineSegment(sketch, "E835", {"start": v(-19.17, 0.85) * mm, "end": v(-19.17, 0.66) * mm});
            skLineSegment(sketch, "E836", {"start": v(-19.17, 0.66) * mm, "end": v(-19.17, 0.47) * mm});
            skLineSegment(sketch, "E837", {"start": v(-19.17, 0.47) * mm, "end": v(-19.17, 0.28) * mm});
            skLineSegment(sketch, "E838", {"start": v(-19.17, 0.28) * mm, "end": v(-19.17, 0.1) * mm});
            skLineSegment(sketch, "E839", {"start": v(-19.17, 0.1) * mm, "end": v(-19.17, -0.1) * mm});
            skLineSegment(sketch, "E840", {"start": v(-19.17, -0.1) * mm, "end": v(-19.17, -0.29) * mm});
            skLineSegment(sketch, "E841", {"start": v(-19.17, -0.29) * mm, "end": v(-19.17, -0.48) * mm});
            skLineSegment(sketch, "E842", {"start": v(-19.17, -0.48) * mm, "end": v(-19.17, -0.66) * mm});
            skLineSegment(sketch, "E843", {"start": v(-19.17, -0.66) * mm, "end": v(-19.17, -0.85) * mm});
            skLineSegment(sketch, "E844", {"start": v(-19.17, -0.85) * mm, "end": v(-19.17, -1.04) * mm});
            skLineSegment(sketch, "E845", {"start": v(-19.17, -1.04) * mm, "end": v(-19.36, -1.05) * mm});
            skLineSegment(sketch, "E846", {"start": v(-19.36, -1.05) * mm, "end": v(-19.55, -1.06) * mm});
            skLineSegment(sketch, "E847", {"start": v(-19.55, -1.06) * mm, "end": v(-19.74, -1.08) * mm});
            skLineSegment(sketch, "E848", {"start": v(-19.74, -1.08) * mm, "end": v(-19.93, -1.09) * mm});
            skLineSegment(sketch, "E849", {"start": v(-19.93, -1.09) * mm, "end": v(-20.12, -1.1) * mm});
            skLineSegment(sketch, "E850", {"start": v(-20.12, -1.1) * mm, "end": v(-20.31, -1.1) * mm});
            skLineSegment(sketch, "E851", {"start": v(-20.31, -1.1) * mm, "end": v(-20.5, -1.12) * mm});
            skLineSegment(sketch, "E852", {"start": v(-20.5, -1.12) * mm, "end": v(-20.69, -1.13) * mm});
            skLineSegment(sketch, "E853", {"start": v(-20.69, -1.13) * mm, "end": v(-20.88, -1.14) * mm});
            skLineSegment(sketch, "E854", {"start": v(-20.88, -1.14) * mm, "end": v(-21.07, -1.15) * mm});
            skLineSegment(sketch, "E855", {"start": v(-21.07, -1.15) * mm, "end": v(-21.26, -1.16) * mm});
            skLineSegment(sketch, "E856", {"start": v(-21.26, -1.16) * mm, "end": v(-21.45, -1.17) * mm});
            skLineSegment(sketch, "E857", {"start": v(-21.45, -1.17) * mm, "end": v(-21.66, -1.19) * mm});
            skLineSegment(sketch, "E858", {"start": v(-21.66, -1.19) * mm, "end": v(-21.85, -1.24) * mm});
            skLineSegment(sketch, "E859", {"start": v(-21.85, -1.24) * mm, "end": v(-22.03, -1.34) * mm});
            skLineSegment(sketch, "E860", {"start": v(-22.03, -1.34) * mm, "end": v(-22.18, -1.5) * mm});
            skLineSegment(sketch, "E861", {"start": v(-22.18, -1.5) * mm, "end": v(-22.28, -1.67) * mm});
            skLineSegment(sketch, "E862", {"start": v(-22.28, -1.67) * mm, "end": v(-22.33, -1.87) * mm});
            skLineSegment(sketch, "E863", {"start": v(-22.33, -1.87) * mm, "end": v(-22.33, -2.08) * mm});
            skLineSegment(sketch, "E864", {"start": v(-22.33, -2.08) * mm, "end": v(-22.27, -2.28) * mm});
            skLineSegment(sketch, "E865", {"start": v(-22.27, -2.28) * mm, "end": v(-22.16, -2.45) * mm});
            skLineSegment(sketch, "E866", {"start": v(-22.16, -2.45) * mm, "end": v(-22.01, -2.6) * mm});
            skLineSegment(sketch, "E867", {"start": v(-22.01, -2.6) * mm, "end": v(-21.83, -2.7) * mm});
            skLineSegment(sketch, "E868", {"start": v(-21.83, -2.7) * mm, "end": v(-21.63, -2.74) * mm});
            skLineSegment(sketch, "E869", {"start": v(-21.63, -2.74) * mm, "end": v(-21.44, -2.73) * mm});
            skLineSegment(sketch, "E870", {"start": v(-21.44, -2.73) * mm, "end": v(-21.25, -2.7) * mm});
            skLineSegment(sketch, "E871", {"start": v(-21.25, -2.7) * mm, "end": v(-21.06, -2.68) * mm});
            skLineSegment(sketch, "E872", {"start": v(-21.06, -2.68) * mm, "end": v(-20.87, -2.66) * mm});
            skLineSegment(sketch, "E873", {"start": v(-20.87, -2.66) * mm, "end": v(-20.69, -2.63) * mm});
            skLineSegment(sketch, "E874", {"start": v(-20.69, -2.63) * mm, "end": v(-20.5, -2.6) * mm});
            skLineSegment(sketch, "E875", {"start": v(-20.5, -2.6) * mm, "end": v(-20.3, -2.58) * mm});
            skLineSegment(sketch, "E876", {"start": v(-20.3, -2.58) * mm, "end": v(-20.12, -2.56) * mm});
            skLineSegment(sketch, "E877", {"start": v(-20.12, -2.56) * mm, "end": v(-19.93, -2.53) * mm});
            skLineSegment(sketch, "E878", {"start": v(-19.93, -2.53) * mm, "end": v(-19.74, -2.5) * mm});
            skLineSegment(sketch, "E879", {"start": v(-19.74, -2.5) * mm, "end": v(-19.55, -2.48) * mm});
            skLineSegment(sketch, "E880", {"start": v(-19.55, -2.48) * mm, "end": v(-19.36, -2.46) * mm});
            skLineSegment(sketch, "E881", {"start": v(-19.36, -2.46) * mm, "end": v(-19.17, -2.43) * mm});
            skLineSegment(sketch, "E882", {"start": v(-19.17, -2.43) * mm, "end": v(-19.04, -2.41) * mm});
            skLineSegment(sketch, "E883", {"start": v(-19.04, -2.41) * mm, "end": v(-19, -2.6) * mm});
            skLineSegment(sketch, "E884", {"start": v(-19, -2.6) * mm, "end": v(-18.97, -2.79) * mm});
            skLineSegment(sketch, "E885", {"start": v(-18.97, -2.79) * mm, "end": v(-18.93, -2.97) * mm});
            skLineSegment(sketch, "E886", {"start": v(-18.93, -2.97) * mm, "end": v(-18.9, -3.16) * mm});
            skLineSegment(sketch, "E887", {"start": v(-18.9, -3.16) * mm, "end": v(-18.86, -3.34) * mm});
            skLineSegment(sketch, "E888", {"start": v(-18.86, -3.34) * mm, "end": v(-18.82, -3.53) * mm});
            skLineSegment(sketch, "E889", {"start": v(-18.82, -3.53) * mm, "end": v(-18.79, -3.72) * mm});
            skLineSegment(sketch, "E890", {"start": v(-18.79, -3.72) * mm, "end": v(-18.75, -3.9) * mm});
            skLineSegment(sketch, "E891", {"start": v(-18.75, -3.9) * mm, "end": v(-18.72, -4.09) * mm});
            skLineSegment(sketch, "E892", {"start": v(-18.72, -4.09) * mm, "end": v(-18.68, -4.27) * mm});
            skLineSegment(sketch, "E893", {"start": v(-18.68, -4.27) * mm, "end": v(-18.64, -4.46) * mm});
            skLineSegment(sketch, "E894", {"start": v(-18.64, -4.46) * mm, "end": v(-18.83, -4.5) * mm});
            skLineSegment(sketch, "E895", {"start": v(-18.83, -4.5) * mm, "end": v(-19.01, -4.55) * mm});
            skLineSegment(sketch, "E896", {"start": v(-19.01, -4.55) * mm, "end": v(-19.2, -4.6) * mm});
            skLineSegment(sketch, "E897", {"start": v(-19.2, -4.6) * mm, "end": v(-19.38, -4.64) * mm});
            skLineSegment(sketch, "E898", {"start": v(-19.38, -4.64) * mm, "end": v(-19.57, -4.7) * mm});
            skLineSegment(sketch, "E899", {"start": v(-19.57, -4.7) * mm, "end": v(-19.75, -4.74) * mm});
            skLineSegment(sketch, "E900", {"start": v(-19.75, -4.74) * mm, "end": v(-19.94, -4.78) * mm});
            skLineSegment(sketch, "E901", {"start": v(-19.94, -4.78) * mm, "end": v(-20.12, -4.83) * mm});
            skLineSegment(sketch, "E902", {"start": v(-20.12, -4.83) * mm, "end": v(-20.3, -4.88) * mm});
            skLineSegment(sketch, "E903", {"start": v(-20.3, -4.88) * mm, "end": v(-20.49, -4.93) * mm});
            skLineSegment(sketch, "E904", {"start": v(-20.49, -4.93) * mm, "end": v(-20.67, -4.97) * mm});
            skLineSegment(sketch, "E905", {"start": v(-20.67, -4.97) * mm, "end": v(-20.86, -5.02) * mm});
            skLineSegment(sketch, "E906", {"start": v(-20.86, -5.02) * mm, "end": v(-21.06, -5.07) * mm});
            skLineSegment(sketch, "E907", {"start": v(-21.06, -5.07) * mm, "end": v(-21.24, -5.16) * mm});
            skLineSegment(sketch, "E908", {"start": v(-21.24, -5.16) * mm, "end": v(-21.4, -5.3) * mm});
            skLineSegment(sketch, "E909", {"start": v(-21.4, -5.3) * mm, "end": v(-21.51, -5.47) * mm});
            skLineSegment(sketch, "E910", {"start": v(-21.51, -5.47) * mm, "end": v(-21.58, -5.66) * mm});
            skLineSegment(sketch, "E911", {"start": v(-21.58, -5.66) * mm, "end": v(-21.6, -5.87) * mm});
            skLineSegment(sketch, "E912", {"start": v(-21.6, -5.87) * mm, "end": v(-21.56, -6.03) * mm});
            skLineSegment(sketch, "E913", {"start": v(-21.56, -6.03) * mm, "end": v(-21.48, -6.22) * mm});
            skLineSegment(sketch, "E914", {"start": v(-21.48, -6.22) * mm, "end": v(-21.35, -6.38) * mm});
            skLineSegment(sketch, "E915", {"start": v(-21.35, -6.38) * mm, "end": v(-21.18, -6.5) * mm});
            skLineSegment(sketch, "E916", {"start": v(-21.18, -6.5) * mm, "end": v(-20.99, -6.57) * mm});
            skLineSegment(sketch, "E917", {"start": v(-20.99, -6.57) * mm, "end": v(-20.78, -6.6) * mm});
            skLineSegment(sketch, "E918", {"start": v(-20.78, -6.6) * mm, "end": v(-20.58, -6.56) * mm});
            skLineSegment(sketch, "E919", {"start": v(-20.58, -6.56) * mm, "end": v(-20.4, -6.5) * mm});
            skLineSegment(sketch, "E920", {"start": v(-20.4, -6.5) * mm, "end": v(-20.22, -6.44) * mm});
            skLineSegment(sketch, "E921", {"start": v(-20.22, -6.44) * mm, "end": v(-20.04, -6.38) * mm});
            skLineSegment(sketch, "E922", {"start": v(-20.04, -6.38) * mm, "end": v(-19.86, -6.32) * mm});
            skLineSegment(sketch, "E923", {"start": v(-19.86, -6.32) * mm, "end": v(-19.68, -6.26) * mm});
            skLineSegment(sketch, "E924", {"start": v(-19.68, -6.26) * mm, "end": v(-19.5, -6.2) * mm});
            skLineSegment(sketch, "E925", {"start": v(-19.5, -6.2) * mm, "end": v(-19.31, -6.13) * mm});
            skLineSegment(sketch, "E926", {"start": v(-19.31, -6.13) * mm, "end": v(-19.14, -6.07) * mm});
            skLineSegment(sketch, "E927", {"start": v(-19.14, -6.07) * mm, "end": v(-18.95, -6.01) * mm});
            skLineSegment(sketch, "E928", {"start": v(-18.95, -6.01) * mm, "end": v(-18.77, -5.95) * mm});
            skLineSegment(sketch, "E929", {"start": v(-18.77, -5.95) * mm, "end": v(-18.6, -5.9) * mm});
            skLineSegment(sketch, "E930", {"start": v(-18.6, -5.9) * mm, "end": v(-18.41, -5.83) * mm});
            skLineSegment(sketch, "E931", {"start": v(-18.41, -5.83) * mm, "end": v(-18.26, -5.78) * mm});
            skLineSegment(sketch, "E932", {"start": v(-18.26, -5.78) * mm, "end": v(-18.19, -5.96) * mm});
            skLineSegment(sketch, "E933", {"start": v(-18.19, -5.96) * mm, "end": v(-18.12, -6.13) * mm});
            skLineSegment(sketch, "E934", {"start": v(-18.12, -6.13) * mm, "end": v(-18.05, -6.3) * mm});
            skLineSegment(sketch, "E935", {"start": v(-18.05, -6.3) * mm, "end": v(-17.97, -6.48) * mm});
            skLineSegment(sketch, "E936", {"start": v(-17.97, -6.48) * mm, "end": v(-17.9, -6.66) * mm});
            skLineSegment(sketch, "E937", {"start": v(-17.9, -6.66) * mm, "end": v(-17.83, -6.83) * mm});
            skLineSegment(sketch, "E938", {"start": v(-17.83, -6.83) * mm, "end": v(-17.76, -7) * mm});
            skLineSegment(sketch, "E939", {"start": v(-17.76, -7) * mm, "end": v(-17.7, -7.19) * mm});
            skLineSegment(sketch, "E940", {"start": v(-17.7, -7.19) * mm, "end": v(-17.62, -7.36) * mm});
            skLineSegment(sketch, "E941", {"start": v(-17.62, -7.36) * mm, "end": v(-17.55, -7.54) * mm});
            skLineSegment(sketch, "E942", {"start": v(-17.55, -7.54) * mm, "end": v(-17.48, -7.71) * mm});
            skLineSegment(sketch, "E943", {"start": v(-17.48, -7.71) * mm, "end": v(-17.65, -7.8) * mm});
            skLineSegment(sketch, "E944", {"start": v(-17.65, -7.8) * mm, "end": v(-17.83, -7.87) * mm});
            skLineSegment(sketch, "E945", {"start": v(-17.83, -7.87) * mm, "end": v(-18, -7.96) * mm});
            skLineSegment(sketch, "E946", {"start": v(-18, -7.96) * mm, "end": v(-18.17, -8.04) * mm});
            skLineSegment(sketch, "E947", {"start": v(-18.17, -8.04) * mm, "end": v(-18.34, -8.12) * mm});
            skLineSegment(sketch, "E948", {"start": v(-18.34, -8.12) * mm, "end": v(-18.52, -8.2) * mm});
            skLineSegment(sketch, "E949", {"start": v(-18.52, -8.2) * mm, "end": v(-18.69, -8.28) * mm});
            skLineSegment(sketch, "E950", {"start": v(-18.69, -8.28) * mm, "end": v(-18.86, -8.36) * mm});
            skLineSegment(sketch, "E951", {"start": v(-18.86, -8.36) * mm, "end": v(-19.03, -8.44) * mm});
            skLineSegment(sketch, "E952", {"start": v(-19.03, -8.44) * mm, "end": v(-19.2, -8.52) * mm});
            skLineSegment(sketch, "E953", {"start": v(-19.2, -8.52) * mm, "end": v(-19.38, -8.6) * mm});
            skLineSegment(sketch, "E954", {"start": v(-19.38, -8.6) * mm, "end": v(-19.55, -8.68) * mm});
            skLineSegment(sketch, "E955", {"start": v(-19.55, -8.68) * mm, "end": v(-19.74, -8.77) * mm});
            skLineSegment(sketch, "E956", {"start": v(-19.74, -8.77) * mm, "end": v(-19.9, -8.9) * mm});
            skLineSegment(sketch, "E957", {"start": v(-19.9, -8.9) * mm, "end": v(-20.03, -9.06) * mm});
            skLineSegment(sketch, "E958", {"start": v(-20.03, -9.06) * mm, "end": v(-20.1, -9.25) * mm});
            skLineSegment(sketch, "E959", {"start": v(-20.1, -9.25) * mm, "end": v(-20.14, -9.45) * mm});
            skLineSegment(sketch, "E960", {"start": v(-20.14, -9.45) * mm, "end": v(-20.1, -9.66) * mm});
            skLineSegment(sketch, "E961", {"start": v(-20.1, -9.66) * mm, "end": v(-20.05, -9.81) * mm});
            skLineSegment(sketch, "E962", {"start": v(-20.05, -9.81) * mm, "end": v(-19.93, -9.98) * mm});
            skLineSegment(sketch, "E963", {"start": v(-19.93, -9.98) * mm, "end": v(-19.77, -10.11) * mm});
            skLineSegment(sketch, "E964", {"start": v(-19.77, -10.11) * mm, "end": v(-19.59, -10.2) * mm});
            skLineSegment(sketch, "E965", {"start": v(-19.59, -10.2) * mm, "end": v(-19.38, -10.23) * mm});
            skLineSegment(sketch, "E966", {"start": v(-19.38, -10.23) * mm, "end": v(-19.18, -10.21) * mm});
            skLineSegment(sketch, "E967", {"start": v(-19.18, -10.21) * mm, "end": v(-18.98, -10.14) * mm});
            skLineSegment(sketch, "E968", {"start": v(-18.98, -10.14) * mm, "end": v(-18.82, -10.05) * mm});
            skLineSegment(sketch, "E969", {"start": v(-18.82, -10.05) * mm, "end": v(-18.65, -9.95) * mm});
            skLineSegment(sketch, "E970", {"start": v(-18.65, -9.95) * mm, "end": v(-18.49, -9.86) * mm});
            skLineSegment(sketch, "E971", {"start": v(-18.49, -9.86) * mm, "end": v(-18.32, -9.77) * mm});
            skLineSegment(sketch, "E972", {"start": v(-18.32, -9.77) * mm, "end": v(-18.16, -9.67) * mm});
            skLineSegment(sketch, "E973", {"start": v(-18.16, -9.67) * mm, "end": v(-17.99, -9.58) * mm});
            skLineSegment(sketch, "E974", {"start": v(-17.99, -9.58) * mm, "end": v(-17.82, -9.49) * mm});
            skLineSegment(sketch, "E975", {"start": v(-17.82, -9.49) * mm, "end": v(-17.66, -9.4) * mm});
            skLineSegment(sketch, "E976", {"start": v(-17.66, -9.4) * mm, "end": v(-17.5, -9.3) * mm});
            skLineSegment(sketch, "E977", {"start": v(-17.5, -9.3) * mm, "end": v(-17.33, -9.2) * mm});
            skLineSegment(sketch, "E978", {"start": v(-17.33, -9.2) * mm, "end": v(-17.16, -9.11) * mm});
            skLineSegment(sketch, "E979", {"start": v(-17.16, -9.11) * mm, "end": v(-17, -9.02) * mm});
            skLineSegment(sketch, "E980", {"start": v(-17, -9.02) * mm, "end": v(-16.85, -8.94) * mm});
            skLineSegment(sketch, "E981", {"start": v(-16.85, -8.94) * mm, "end": v(-16.75, -9.1) * mm});
            skLineSegment(sketch, "E982", {"start": v(-16.75, -9.1) * mm, "end": v(-16.65, -9.26) * mm});
            skLineSegment(sketch, "E983", {"start": v(-16.65, -9.26) * mm, "end": v(-16.54, -9.41) * mm});
            skLineSegment(sketch, "E984", {"start": v(-16.54, -9.41) * mm, "end": v(-16.44, -9.57) * mm});
            skLineSegment(sketch, "E985", {"start": v(-16.44, -9.57) * mm, "end": v(-16.34, -9.73) * mm});
            skLineSegment(sketch, "E986", {"start": v(-16.34, -9.73) * mm, "end": v(-16.24, -9.9) * mm});
            skLineSegment(sketch, "E987", {"start": v(-16.24, -9.9) * mm, "end": v(-16.13, -10.05) * mm});
            skLineSegment(sketch, "E988", {"start": v(-16.13, -10.05) * mm, "end": v(-16.03, -10.21) * mm});
            skLineSegment(sketch, "E989", {"start": v(-16.03, -10.21) * mm, "end": v(-15.93, -10.37) * mm});
            skLineSegment(sketch, "E990", {"start": v(-15.93, -10.37) * mm, "end": v(-15.83, -10.53) * mm});
            skLineSegment(sketch, "E991", {"start": v(-15.83, -10.53) * mm, "end": v(-15.73, -10.69) * mm});
            skLineSegment(sketch, "E992", {"start": v(-15.73, -10.69) * mm, "end": v(-15.88, -10.8) * mm});
            skLineSegment(sketch, "E993", {"start": v(-15.88, -10.8) * mm, "end": v(-16.03, -10.91) * mm});
            skLineSegment(sketch, "E994", {"start": v(-16.03, -10.91) * mm, "end": v(-16.19, -11.02) * mm});
            skLineSegment(sketch, "E995", {"start": v(-16.19, -11.02) * mm, "end": v(-16.34, -11.14) * mm});
            skLineSegment(sketch, "E996", {"start": v(-16.34, -11.14) * mm, "end": v(-16.5, -11.25) * mm});
            skLineSegment(sketch, "E997", {"start": v(-16.5, -11.25) * mm, "end": v(-16.65, -11.36) * mm});
            skLineSegment(sketch, "E998", {"start": v(-16.65, -11.36) * mm, "end": v(-16.8, -11.47) * mm});
            skLineSegment(sketch, "E999", {"start": v(-16.8, -11.47) * mm, "end": v(-16.96, -11.58) * mm});
            skLineSegment(sketch, "E1000", {"start": v(-16.96, -11.58) * mm, "end": v(-17.11, -11.7) * mm});
            skLineSegment(sketch, "E1001", {"start": v(-17.11, -11.7) * mm, "end": v(-17.27, -11.8) * mm});
            skLineSegment(sketch, "E1002", {"start": v(-17.27, -11.8) * mm, "end": v(-17.42, -11.92) * mm});
            skLineSegment(sketch, "E1003", {"start": v(-17.42, -11.92) * mm, "end": v(-17.57, -12.03) * mm});
            skLineSegment(sketch, "E1004", {"start": v(-17.57, -12.03) * mm, "end": v(-17.74, -12.15) * mm});
            skLineSegment(sketch, "E1005", {"start": v(-17.74, -12.15) * mm, "end": v(-17.88, -12.3) * mm});
            skLineSegment(sketch, "E1006", {"start": v(-17.88, -12.3) * mm, "end": v(-17.97, -12.5) * mm});
            skLineSegment(sketch, "E1007", {"start": v(-17.97, -12.5) * mm, "end": v(-18.01, -12.7) * mm});
            skLineSegment(sketch, "E1008", {"start": v(-18.01, -12.7) * mm, "end": v(-18, -12.9) * mm});
            skLineSegment(sketch, "E1009", {"start": v(-18, -12.9) * mm, "end": v(-17.94, -13.1) * mm});
            skLineSegment(sketch, "E1010", {"start": v(-17.94, -13.1) * mm, "end": v(-17.85, -13.23) * mm});
            skLineSegment(sketch, "E1011", {"start": v(-17.85, -13.23) * mm, "end": v(-17.7, -13.38) * mm});
            skLineSegment(sketch, "E1012", {"start": v(-17.7, -13.38) * mm, "end": v(-17.52, -13.48) * mm});
            skLineSegment(sketch, "E1013", {"start": v(-17.52, -13.48) * mm, "end": v(-17.32, -13.53) * mm});
            skLineSegment(sketch, "E1014", {"start": v(-17.32, -13.53) * mm, "end": v(-17.11, -13.52) * mm});
            skLineSegment(sketch, "E1015", {"start": v(-17.11, -13.52) * mm, "end": v(-16.92, -13.47) * mm});
            skLineSegment(sketch, "E1016", {"start": v(-16.92, -13.47) * mm, "end": v(-16.74, -13.36) * mm});
            skLineSegment(sketch, "E1017", {"start": v(-16.74, -13.36) * mm, "end": v(-16.6, -13.23) * mm});
            skLineSegment(sketch, "E1018", {"start": v(-16.6, -13.23) * mm, "end": v(-16.45, -13.11) * mm});
            skLineSegment(sketch, "E1019", {"start": v(-16.45, -13.11) * mm, "end": v(-16.3, -12.99) * mm});
            skLineSegment(sketch, "E1020", {"start": v(-16.3, -12.99) * mm, "end": v(-16.16, -12.86) * mm});
            skLineSegment(sketch, "E1021", {"start": v(-16.16, -12.86) * mm, "end": v(-16.02, -12.74) * mm});
            skLineSegment(sketch, "E1022", {"start": v(-16.02, -12.74) * mm, "end": v(-15.87, -12.62) * mm});
            skLineSegment(sketch, "E1023", {"start": v(-15.87, -12.62) * mm, "end": v(-15.73, -12.5) * mm});
            skLineSegment(sketch, "E1024", {"start": v(-15.73, -12.5) * mm, "end": v(-15.58, -12.37) * mm});
            skLineSegment(sketch, "E1025", {"start": v(-15.58, -12.37) * mm, "end": v(-15.43, -12.25) * mm});
            skLineSegment(sketch, "E1026", {"start": v(-15.43, -12.25) * mm, "end": v(-15.29, -12.12) * mm});
            skLineSegment(sketch, "E1027", {"start": v(-15.29, -12.12) * mm, "end": v(-15.15, -12) * mm});
            skLineSegment(sketch, "E1028", {"start": v(-15.15, -12) * mm, "end": v(-15, -11.88) * mm});
            skLineSegment(sketch, "E1029", {"start": v(-15, -11.88) * mm, "end": v(-14.87, -11.77) * mm});
            skLineSegment(sketch, "E1030", {"start": v(-14.87, -11.77) * mm, "end": v(-14.74, -11.9) * mm});
            skLineSegment(sketch, "E1031", {"start": v(-14.74, -11.9) * mm, "end": v(-14.61, -12.05) * mm});
            skLineSegment(sketch, "E1032", {"start": v(-14.61, -12.05) * mm, "end": v(-14.48, -12.18) * mm});
            skLineSegment(sketch, "E1033", {"start": v(-14.48, -12.18) * mm, "end": v(-14.35, -12.32) * mm});
            skLineSegment(sketch, "E1034", {"start": v(-14.35, -12.32) * mm, "end": v(-14.22, -12.46) * mm});
            skLineSegment(sketch, "E1035", {"start": v(-14.22, -12.46) * mm, "end": v(-14.1, -12.6) * mm});
            skLineSegment(sketch, "E1036", {"start": v(-14.1, -12.6) * mm, "end": v(-13.96, -12.73) * mm});
            skLineSegment(sketch, "E1037", {"start": v(-13.96, -12.73) * mm, "end": v(-13.83, -12.87) * mm});
            skLineSegment(sketch, "E1038", {"start": v(-13.83, -12.87) * mm, "end": v(-13.7, -13) * mm});
            skLineSegment(sketch, "E1039", {"start": v(-13.7, -13) * mm, "end": v(-13.57, -13.14) * mm});
            skLineSegment(sketch, "E1040", {"start": v(-13.57, -13.14) * mm, "end": v(-13.44, -13.28) * mm});
            skLineSegment(sketch, "E1041", {"start": v(-13.44, -13.28) * mm, "end": v(-13.57, -13.42) * mm});
            skLineSegment(sketch, "E1042", {"start": v(-13.57, -13.42) * mm, "end": v(-13.7, -13.55) * mm});
            skLineSegment(sketch, "E1043", {"start": v(-13.7, -13.55) * mm, "end": v(-13.83, -13.7) * mm});
            skLineSegment(sketch, "E1044", {"start": v(-13.83, -13.7) * mm, "end": v(-13.96, -13.83) * mm});
            skLineSegment(sketch, "E1045", {"start": v(-13.96, -13.83) * mm, "end": v(-14.09, -13.97) * mm});
            skLineSegment(sketch, "E1046", {"start": v(-14.09, -13.97) * mm, "end": v(-14.22, -14.11) * mm});
            skLineSegment(sketch, "E1047", {"start": v(-14.22, -14.11) * mm, "end": v(-14.35, -14.25) * mm});
            skLineSegment(sketch, "E1048", {"start": v(-14.35, -14.25) * mm, "end": v(-14.48, -14.39) * mm});
            skLineSegment(sketch, "E1049", {"start": v(-14.48, -14.39) * mm, "end": v(-14.6, -14.53) * mm});
            skLineSegment(sketch, "E1050", {"start": v(-14.6, -14.53) * mm, "end": v(-14.74, -14.67) * mm});
            skLineSegment(sketch, "E1051", {"start": v(-14.74, -14.67) * mm, "end": v(-14.87, -14.8) * mm});
            skLineSegment(sketch, "E1052", {"start": v(-14.87, -14.8) * mm, "end": v(-15, -14.95) * mm});
            skLineSegment(sketch, "E1053", {"start": v(-15, -14.95) * mm, "end": v(-15.14, -15.1) * mm});
            skLineSegment(sketch, "E1054", {"start": v(-15.14, -15.1) * mm, "end": v(-15.24, -15.27) * mm});
            skLineSegment(sketch, "E1055", {"start": v(-15.24, -15.27) * mm, "end": v(-15.3, -15.47) * mm});
            skLineSegment(sketch, "E1056", {"start": v(-15.3, -15.47) * mm, "end": v(-15.3, -15.68) * mm});
            skLineSegment(sketch, "E1057", {"start": v(-15.3, -15.68) * mm, "end": v(-15.25, -15.88) * mm});
            skLineSegment(sketch, "E1058", {"start": v(-15.25, -15.88) * mm, "end": v(-15.15, -16.06) * mm});
            skLineSegment(sketch, "E1059", {"start": v(-15.15, -16.06) * mm, "end": v(-15.04, -16.18) * mm});
            skLineSegment(sketch, "E1060", {"start": v(-15.04, -16.18) * mm, "end": v(-14.87, -16.3) * mm});
            skLineSegment(sketch, "E1061", {"start": v(-14.87, -16.3) * mm, "end": v(-14.67, -16.36) * mm});
            skLineSegment(sketch, "E1062", {"start": v(-14.67, -16.36) * mm, "end": v(-14.47, -16.37) * mm});
            skLineSegment(sketch, "E1063", {"start": v(-14.47, -16.37) * mm, "end": v(-14.26, -16.32) * mm});
            skLineSegment(sketch, "E1064", {"start": v(-14.26, -16.32) * mm, "end": v(-14.08, -16.23) * mm});
            skLineSegment(sketch, "E1065", {"start": v(-14.08, -16.23) * mm, "end": v(-13.93, -16.09) * mm});
            skLineSegment(sketch, "E1066", {"start": v(-13.93, -16.09) * mm, "end": v(-13.81, -15.94) * mm});
            skLineSegment(sketch, "E1067", {"start": v(-13.81, -15.94) * mm, "end": v(-13.7, -15.8) * mm});
            skLineSegment(sketch, "E1068", {"start": v(-13.7, -15.8) * mm, "end": v(-13.57, -15.64) * mm});
            skLineSegment(sketch, "E1069", {"start": v(-13.57, -15.64) * mm, "end": v(-13.45, -15.5) * mm});
            skLineSegment(sketch, "E1070", {"start": v(-13.45, -15.5) * mm, "end": v(-13.33, -15.35) * mm});
            skLineSegment(sketch, "E1071", {"start": v(-13.33, -15.35) * mm, "end": v(-13.21, -15.2) * mm});
            skLineSegment(sketch, "E1072", {"start": v(-13.21, -15.2) * mm, "end": v(-13.1, -15.05) * mm});
            skLineSegment(sketch, "E1073", {"start": v(-13.1, -15.05) * mm, "end": v(-12.98, -14.9) * mm});
            skLineSegment(sketch, "E1074", {"start": v(-12.98, -14.9) * mm, "end": v(-12.86, -14.75) * mm});
            skLineSegment(sketch, "E1075", {"start": v(-12.86, -14.75) * mm, "end": v(-12.74, -14.6) * mm});
            skLineSegment(sketch, "E1076", {"start": v(-12.74, -14.6) * mm, "end": v(-12.62, -14.46) * mm});
            skLineSegment(sketch, "E1077", {"start": v(-12.62, -14.46) * mm, "end": v(-12.5, -14.3) * mm});
            skLineSegment(sketch, "E1078", {"start": v(-12.5, -14.3) * mm, "end": v(-12.4, -14.18) * mm});
            skLineSegment(sketch, "E1079", {"start": v(-12.4, -14.18) * mm, "end": v(-12.24, -14.29) * mm});
            skLineSegment(sketch, "E1080", {"start": v(-12.24, -14.29) * mm, "end": v(-12.09, -14.4) * mm});
            skLineSegment(sketch, "E1081", {"start": v(-12.09, -14.4) * mm, "end": v(-11.93, -14.5) * mm});
            skLineSegment(sketch, "E1082", {"start": v(-11.93, -14.5) * mm, "end": v(-11.78, -14.62) * mm});
            skLineSegment(sketch, "E1083", {"start": v(-11.78, -14.62) * mm, "end": v(-11.63, -14.73) * mm});
            skLineSegment(sketch, "E1084", {"start": v(-11.63, -14.73) * mm, "end": v(-11.47, -14.84) * mm});
            skLineSegment(sketch, "E1085", {"start": v(-11.47, -14.84) * mm, "end": v(-11.32, -14.95) * mm});
            skLineSegment(sketch, "E1086", {"start": v(-11.32, -14.95) * mm, "end": v(-11.16, -15.06) * mm});
            skLineSegment(sketch, "E1087", {"start": v(-11.16, -15.06) * mm, "end": v(-11, -15.17) * mm});
            skLineSegment(sketch, "E1088", {"start": v(-11, -15.17) * mm, "end": v(-10.85, -15.28) * mm});
            skLineSegment(sketch, "E1089", {"start": v(-10.85, -15.28) * mm, "end": v(-10.7, -15.39) * mm});
            skLineSegment(sketch, "E1090", {"start": v(-10.7, -15.39) * mm, "end": v(-10.8, -15.55) * mm});
            skLineSegment(sketch, "E1091", {"start": v(-10.8, -15.55) * mm, "end": v(-10.9, -15.7) * mm});
            skLineSegment(sketch, "E1092", {"start": v(-10.9, -15.7) * mm, "end": v(-11, -15.87) * mm});
            skLineSegment(sketch, "E1093", {"start": v(-11, -15.87) * mm, "end": v(-11.1, -16.03) * mm});
            skLineSegment(sketch, "E1094", {"start": v(-11.1, -16.03) * mm, "end": v(-11.2, -16.2) * mm});
            skLineSegment(sketch, "E1095", {"start": v(-11.2, -16.2) * mm, "end": v(-11.3, -16.35) * mm});
            skLineSegment(sketch, "E1096", {"start": v(-11.3, -16.35) * mm, "end": v(-11.41, -16.51) * mm});
            skLineSegment(sketch, "E1097", {"start": v(-11.41, -16.51) * mm, "end": v(-11.51, -16.68) * mm});
            skLineSegment(sketch, "E1098", {"start": v(-11.51, -16.68) * mm, "end": v(-11.61, -16.84) * mm});
            skLineSegment(sketch, "E1099", {"start": v(-11.61, -16.84) * mm, "end": v(-11.71, -17) * mm});
            skLineSegment(sketch, "E1100", {"start": v(-11.71, -17) * mm, "end": v(-11.82, -17.16) * mm});
            skLineSegment(sketch, "E1101", {"start": v(-11.82, -17.16) * mm, "end": v(-11.92, -17.32) * mm});
            skLineSegment(sketch, "E1102", {"start": v(-11.92, -17.32) * mm, "end": v(-12.03, -17.5) * mm});
            skLineSegment(sketch, "E1103", {"start": v(-12.03, -17.5) * mm, "end": v(-12.1, -17.69) * mm});
            skLineSegment(sketch, "E1104", {"start": v(-12.1, -17.69) * mm, "end": v(-12.12, -17.9) * mm});
            skLineSegment(sketch, "E1105", {"start": v(-12.12, -17.9) * mm, "end": v(-12.08, -18.1) * mm});
            skLineSegment(sketch, "E1106", {"start": v(-12.08, -18.1) * mm, "end": v(-12, -18.29) * mm});
            skLineSegment(sketch, "E1107", {"start": v(-12, -18.29) * mm, "end": v(-11.86, -18.44) * mm});
            skLineSegment(sketch, "E1108", {"start": v(-11.86, -18.44) * mm, "end": v(-11.73, -18.54) * mm});
            skLineSegment(sketch, "E1109", {"start": v(-11.73, -18.54) * mm, "end": v(-11.54, -18.62) * mm});
            skLineSegment(sketch, "E1110", {"start": v(-11.54, -18.62) * mm, "end": v(-11.33, -18.65) * mm});
            skLineSegment(sketch, "E1111", {"start": v(-11.33, -18.65) * mm, "end": v(-11.13, -18.62) * mm});
            skLineSegment(sketch, "E1112", {"start": v(-11.13, -18.62) * mm, "end": v(-10.94, -18.54) * mm});
            skLineSegment(sketch, "E1113", {"start": v(-10.94, -18.54) * mm, "end": v(-10.77, -18.4) * mm});
            skLineSegment(sketch, "E1114", {"start": v(-10.77, -18.4) * mm, "end": v(-10.65, -18.24) * mm});
            skLineSegment(sketch, "E1115", {"start": v(-10.65, -18.24) * mm, "end": v(-10.56, -18.07) * mm});
            skLineSegment(sketch, "E1116", {"start": v(-10.56, -18.07) * mm, "end": v(-10.47, -17.9) * mm});
            skLineSegment(sketch, "E1117", {"start": v(-10.47, -17.9) * mm, "end": v(-10.38, -17.74) * mm});
            skLineSegment(sketch, "E1118", {"start": v(-10.38, -17.74) * mm, "end": v(-10.3, -17.57) * mm});
            skLineSegment(sketch, "E1119", {"start": v(-10.3, -17.57) * mm, "end": v(-10.2, -17.4) * mm});
            skLineSegment(sketch, "E1120", {"start": v(-10.2, -17.4) * mm, "end": v(-10.12, -17.23) * mm});
            skLineSegment(sketch, "E1121", {"start": v(-10.12, -17.23) * mm, "end": v(-10.03, -17.06) * mm});
            skLineSegment(sketch, "E1122", {"start": v(-10.03, -17.06) * mm, "end": v(-9.94, -16.9) * mm});
            skLineSegment(sketch, "E1123", {"start": v(-9.94, -16.9) * mm, "end": v(-9.85, -16.73) * mm});
            skLineSegment(sketch, "E1124", {"start": v(-9.85, -16.73) * mm, "end": v(-9.76, -16.56) * mm});
            skLineSegment(sketch, "E1125", {"start": v(-9.76, -16.56) * mm, "end": v(-9.67, -16.4) * mm});
            skLineSegment(sketch, "E1126", {"start": v(-9.67, -16.4) * mm, "end": v(-9.58, -16.22) * mm});
            skLineSegment(sketch, "E1127", {"start": v(-9.58, -16.22) * mm, "end": v(-9.5, -16.08) * mm});
            skLineSegment(sketch, "E1128", {"start": v(-9.5, -16.08) * mm, "end": v(-9.34, -16.15) * mm});
            skLineSegment(sketch, "E1129", {"start": v(-9.34, -16.15) * mm, "end": v(-9.16, -16.23) * mm});
            skLineSegment(sketch, "E1130", {"start": v(-9.16, -16.23) * mm, "end": v(-9, -16.31) * mm});
            skLineSegment(sketch, "E1131", {"start": v(-9, -16.31) * mm, "end": v(-8.82, -16.4) * mm});
            skLineSegment(sketch, "E1132", {"start": v(-8.82, -16.4) * mm, "end": v(-8.65, -16.47) * mm});
            skLineSegment(sketch, "E1133", {"start": v(-8.65, -16.47) * mm, "end": v(-8.47, -16.55) * mm});
            skLineSegment(sketch, "E1134", {"start": v(-8.47, -16.55) * mm, "end": v(-8.3, -16.63) * mm});
            skLineSegment(sketch, "E1135", {"start": v(-8.3, -16.63) * mm, "end": v(-8.13, -16.7) * mm});
            skLineSegment(sketch, "E1136", {"start": v(-8.13, -16.7) * mm, "end": v(-7.96, -16.78) * mm});
            skLineSegment(sketch, "E1137", {"start": v(-7.96, -16.78) * mm, "end": v(-7.79, -16.86) * mm});
            skLineSegment(sketch, "E1138", {"start": v(-7.79, -16.86) * mm, "end": v(-7.61, -16.94) * mm});
            skLineSegment(sketch, "E1139", {"start": v(-7.61, -16.94) * mm, "end": v(-7.68, -17.12) * mm});
            skLineSegment(sketch, "E1140", {"start": v(-7.68, -17.12) * mm, "end": v(-7.75, -17.3) * mm});
            skLineSegment(sketch, "E1141", {"start": v(-7.75, -17.3) * mm, "end": v(-7.82, -17.47) * mm});
            skLineSegment(sketch, "E1142", {"start": v(-7.82, -17.47) * mm, "end": v(-7.89, -17.65) * mm});
            skLineSegment(sketch, "E1143", {"start": v(-7.89, -17.65) * mm, "end": v(-7.96, -17.83) * mm});
            skLineSegment(sketch, "E1144", {"start": v(-7.96, -17.83) * mm, "end": v(-8.03, -18) * mm});
            skLineSegment(sketch, "E1145", {"start": v(-8.03, -18) * mm, "end": v(-8.1, -18.18) * mm});
            skLineSegment(sketch, "E1146", {"start": v(-8.1, -18.18) * mm, "end": v(-8.17, -18.36) * mm});
            skLineSegment(sketch, "E1147", {"start": v(-8.17, -18.36) * mm, "end": v(-8.24, -18.54) * mm});
            skLineSegment(sketch, "E1148", {"start": v(-8.24, -18.54) * mm, "end": v(-8.3, -18.71) * mm});
            skLineSegment(sketch, "E1149", {"start": v(-8.3, -18.71) * mm, "end": v(-8.37, -18.9) * mm});
            skLineSegment(sketch, "E1150", {"start": v(-8.37, -18.9) * mm, "end": v(-8.44, -19.07) * mm});
            skLineSegment(sketch, "E1151", {"start": v(-8.44, -19.07) * mm, "end": v(-8.52, -19.26) * mm});
            skLineSegment(sketch, "E1152", {"start": v(-8.52, -19.26) * mm, "end": v(-8.55, -19.47) * mm});
            skLineSegment(sketch, "E1153", {"start": v(-8.55, -19.47) * mm, "end": v(-8.53, -19.67) * mm});
            skLineSegment(sketch, "E1154", {"start": v(-8.53, -19.67) * mm, "end": v(-8.46, -19.86) * mm});
            skLineSegment(sketch, "E1155", {"start": v(-8.46, -19.86) * mm, "end": v(-8.33, -20.03) * mm});
            skLineSegment(sketch, "E1156", {"start": v(-8.33, -20.03) * mm, "end": v(-8.17, -20.16) * mm});
            skLineSegment(sketch, "E1157", {"start": v(-8.17, -20.16) * mm, "end": v(-8.02, -20.23) * mm});
            skLineSegment(sketch, "E1158", {"start": v(-8.02, -20.23) * mm, "end": v(-7.82, -20.27) * mm});
            skLineSegment(sketch, "E1159", {"start": v(-7.82, -20.27) * mm, "end": v(-7.62, -20.26) * mm});
            skLineSegment(sketch, "E1160", {"start": v(-7.62, -20.26) * mm, "end": v(-7.42, -20.2) * mm});
            skLineSegment(sketch, "E1161", {"start": v(-7.42, -20.2) * mm, "end": v(-7.25, -20.08) * mm});
            skLineSegment(sketch, "E1162", {"start": v(-7.25, -20.08) * mm, "end": v(-7.11, -19.92) * mm});
            skLineSegment(sketch, "E1163", {"start": v(-7.11, -19.92) * mm, "end": v(-7.03, -19.73) * mm});
            skLineSegment(sketch, "E1164", {"start": v(-7.03, -19.73) * mm, "end": v(-6.97, -19.55) * mm});
            skLineSegment(sketch, "E1165", {"start": v(-6.97, -19.55) * mm, "end": v(-6.92, -19.37) * mm});
            skLineSegment(sketch, "E1166", {"start": v(-6.92, -19.37) * mm, "end": v(-6.86, -19.19) * mm});
            skLineSegment(sketch, "E1167", {"start": v(-6.86, -19.19) * mm, "end": v(-6.8, -19) * mm});
            skLineSegment(sketch, "E1168", {"start": v(-6.8, -19) * mm, "end": v(-6.75, -18.83) * mm});
            skLineSegment(sketch, "E1169", {"start": v(-6.75, -18.83) * mm, "end": v(-6.7, -18.64) * mm});
            skLineSegment(sketch, "E1170", {"start": v(-6.7, -18.64) * mm, "end": v(-6.64, -18.46) * mm});
            skLineSegment(sketch, "E1171", {"start": v(-6.64, -18.46) * mm, "end": v(-6.58, -18.28) * mm});
            skLineSegment(sketch, "E1172", {"start": v(-6.58, -18.28) * mm, "end": v(-6.53, -18.1) * mm});
            skLineSegment(sketch, "E1173", {"start": v(-6.53, -18.1) * mm, "end": v(-6.47, -17.91) * mm});
            skLineSegment(sketch, "E1174", {"start": v(-6.47, -17.91) * mm, "end": v(-6.42, -17.73) * mm});
            skLineSegment(sketch, "E1175", {"start": v(-6.42, -17.73) * mm, "end": v(-6.36, -17.55) * mm});
            skLineSegment(sketch, "E1176", {"start": v(-6.36, -17.55) * mm, "end": v(-6.31, -17.4) * mm});
            skLineSegment(sketch, "E1177", {"start": v(-6.31, -17.4) * mm, "end": v(-6.13, -17.44) * mm});
            skLineSegment(sketch, "E1178", {"start": v(-6.13, -17.44) * mm, "end": v(-5.94, -17.48) * mm});
            skLineSegment(sketch, "E1179", {"start": v(-5.94, -17.48) * mm, "end": v(-5.76, -17.53) * mm});
            skLineSegment(sketch, "E1180", {"start": v(-5.76, -17.53) * mm, "end": v(-5.58, -17.57) * mm});
            skLineSegment(sketch, "E1181", {"start": v(-5.58, -17.57) * mm, "end": v(-5.4, -17.61) * mm});
            skLineSegment(sketch, "E1182", {"start": v(-5.4, -17.61) * mm, "end": v(-5.2, -17.66) * mm});
            skLineSegment(sketch, "E1183", {"start": v(-5.2, -17.66) * mm, "end": v(-5.02, -17.7) * mm});
            skLineSegment(sketch, "E1184", {"start": v(-5.02, -17.7) * mm, "end": v(-4.84, -17.75) * mm});
            skLineSegment(sketch, "E1185", {"start": v(-4.84, -17.75) * mm, "end": v(-4.66, -17.8) * mm});
            skLineSegment(sketch, "E1186", {"start": v(-4.66, -17.8) * mm, "end": v(-4.47, -17.84) * mm});
            skLineSegment(sketch, "E1187", {"start": v(-4.47, -17.84) * mm, "end": v(-4.29, -17.88) * mm});
            skLineSegment(sketch, "E1188", {"start": v(-4.29, -17.88) * mm, "end": v(-4.32, -18.07) * mm});
            skLineSegment(sketch, "E1189", {"start": v(-4.32, -18.07) * mm, "end": v(-4.36, -18.25) * mm});
            skLineSegment(sketch, "E1190", {"start": v(-4.36, -18.25) * mm, "end": v(-4.4, -18.44) * mm});
            skLineSegment(sketch, "E1191", {"start": v(-4.4, -18.44) * mm, "end": v(-4.43, -18.63) * mm});
            skLineSegment(sketch, "E1192", {"start": v(-4.43, -18.63) * mm, "end": v(-4.46, -18.82) * mm});
            skLineSegment(sketch, "E1193", {"start": v(-4.46, -18.82) * mm, "end": v(-4.5, -19) * mm});
            skLineSegment(sketch, "E1194", {"start": v(-4.5, -19) * mm, "end": v(-4.53, -19.2) * mm});
            skLineSegment(sketch, "E1195", {"start": v(-4.53, -19.2) * mm, "end": v(-4.56, -19.38) * mm});
            skLineSegment(sketch, "E1196", {"start": v(-4.56, -19.38) * mm, "end": v(-4.6, -19.57) * mm});
            skLineSegment(sketch, "E1197", {"start": v(-4.6, -19.57) * mm, "end": v(-4.63, -19.75) * mm});
            skLineSegment(sketch, "E1198", {"start": v(-4.63, -19.75) * mm, "end": v(-4.67, -19.94) * mm});
            skLineSegment(sketch, "E1199", {"start": v(-4.67, -19.94) * mm, "end": v(-4.7, -20.13) * mm});
            skLineSegment(sketch, "E1200", {"start": v(-4.7, -20.13) * mm, "end": v(-4.73, -20.33) * mm});
            skLineSegment(sketch, "E1201", {"start": v(-4.73, -20.33) * mm, "end": v(-4.73, -20.54) * mm});
            skLineSegment(sketch, "E1202", {"start": v(-4.73, -20.54) * mm, "end": v(-4.67, -20.74) * mm});
            skLineSegment(sketch, "E1203", {"start": v(-4.67, -20.74) * mm, "end": v(-4.56, -20.91) * mm});
            skLineSegment(sketch, "E1204", {"start": v(-4.56, -20.91) * mm, "end": v(-4.41, -21.05) * mm});
            skLineSegment(sketch, "E1205", {"start": v(-4.41, -21.05) * mm, "end": v(-4.23, -21.15) * mm});
            skLineSegment(sketch, "E1206", {"start": v(-4.23, -21.15) * mm, "end": v(-4.03, -21.2) * mm});
            skLineSegment(sketch, "E1207", {"start": v(-4.03, -21.2) * mm, "end": v(-3.82, -21.19) * mm});
            skLineSegment(sketch, "E1208", {"start": v(-3.82, -21.19) * mm, "end": v(-3.62, -21.12) * mm});
            skLineSegment(sketch, "E1209", {"start": v(-3.62, -21.12) * mm, "end": v(-3.45, -21.01) * mm});
            skLineSegment(sketch, "E1210", {"start": v(-3.45, -21.01) * mm, "end": v(-3.31, -20.86) * mm});
            skLineSegment(sketch, "E1211", {"start": v(-3.31, -20.86) * mm, "end": v(-3.22, -20.67) * mm});
            skLineSegment(sketch, "E1212", {"start": v(-3.22, -20.67) * mm, "end": v(-3.18, -20.51) * mm});
            skLineSegment(sketch, "E1213", {"start": v(-3.18, -20.51) * mm, "end": v(-3.16, -20.33) * mm});
            skLineSegment(sketch, "E1214", {"start": v(-3.16, -20.33) * mm, "end": v(-3.14, -20.14) * mm});
            skLineSegment(sketch, "E1215", {"start": v(-3.14, -20.14) * mm, "end": v(-3.12, -19.95) * mm});
            skLineSegment(sketch, "E1216", {"start": v(-3.12, -19.95) * mm, "end": v(-3.1, -19.76) * mm});
            skLineSegment(sketch, "E1217", {"start": v(-3.1, -19.76) * mm, "end": v(-3.08, -19.57) * mm});
            skLineSegment(sketch, "E1218", {"start": v(-3.08, -19.57) * mm, "end": v(-3.06, -19.38) * mm});
            skLineSegment(sketch, "E1219", {"start": v(-3.06, -19.38) * mm, "end": v(-3.04, -19.19) * mm});
            skLineSegment(sketch, "E1220", {"start": v(-3.04, -19.19) * mm, "end": v(-3.02, -19) * mm});
            skLineSegment(sketch, "E1221", {"start": v(-3.02, -19) * mm, "end": v(-3, -18.8) * mm});
            skLineSegment(sketch, "E1222", {"start": v(-3, -18.8) * mm, "end": v(-2.98, -18.62) * mm});
            skLineSegment(sketch, "E1223", {"start": v(-2.98, -18.62) * mm, "end": v(-2.96, -18.43) * mm});
            skLineSegment(sketch, "E1224", {"start": v(-2.96, -18.43) * mm, "end": v(-2.94, -18.24) * mm});
            skLineSegment(sketch, "E1225", {"start": v(-2.94, -18.24) * mm, "end": v(-2.93, -18.08) * mm});
            skLineSegment(sketch, "E1226", {"start": v(-2.93, -18.08) * mm, "end": v(-2.74, -18.09) * mm});
            skLineSegment(sketch, "E1227", {"start": v(-2.74, -18.09) * mm, "end": v(-2.55, -18.1) * mm});
            skLineSegment(sketch, "E1228", {"start": v(-2.55, -18.1) * mm, "end": v(-2.36, -18.1) * mm});
            skLineSegment(sketch, "E1229", {"start": v(-2.36, -18.1) * mm, "end": v(-2.17, -18.11) * mm});
            skLineSegment(sketch, "E1230", {"start": v(-2.17, -18.11) * mm, "end": v(-1.98, -18.12) * mm});
            skLineSegment(sketch, "E1231", {"start": v(-1.98, -18.12) * mm, "end": v(-1.8, -18.13) * mm});
            skLineSegment(sketch, "E1232", {"start": v(-1.8, -18.13) * mm, "end": v(-1.6, -18.14) * mm});
            skLineSegment(sketch, "E1233", {"start": v(-1.6, -18.14) * mm, "end": v(-1.41, -18.15) * mm});
            skLineSegment(sketch, "E1234", {"start": v(-1.41, -18.15) * mm, "end": v(-1.22, -18.16) * mm});
            skLineSegment(sketch, "E1235", {"start": v(-1.22, -18.16) * mm, "end": v(-1.04, -18.17) * mm});
            skLineSegment(sketch, "E1236", {"start": v(-1.04, -18.17) * mm, "end": v(-0.85, -18.18) * mm});
            skLineSegment(sketch, "E1237", {"start": v(-0.85, -18.18) * mm, "end": v(-0.84, -18.37) * mm});
            skLineSegment(sketch, "E1238", {"start": v(-0.84, -18.37) * mm, "end": v(-0.84, -18.56) * mm});
            skLineSegment(sketch, "E1239", {"start": v(-0.84, -18.56) * mm, "end": v(-0.84, -18.75) * mm});
            skLineSegment(sketch, "E1240", {"start": v(-0.84, -18.75) * mm, "end": v(-0.84, -18.94) * mm});
            skLineSegment(sketch, "E1241", {"start": v(-0.84, -18.94) * mm, "end": v(-0.84, -19.13) * mm});
            skLineSegment(sketch, "E1242", {"start": v(-0.84, -19.13) * mm, "end": v(-0.84, -19.32) * mm});
            skLineSegment(sketch, "E1243", {"start": v(-0.84, -19.32) * mm, "end": v(-0.83, -19.5) * mm});
            skLineSegment(sketch, "E1244", {"start": v(-0.83, -19.5) * mm, "end": v(-0.83, -19.7) * mm});
            skLineSegment(sketch, "E1245", {"start": v(-0.83, -19.7) * mm, "end": v(-0.83, -19.9) * mm});
            skLineSegment(sketch, "E1246", {"start": v(-0.83, -19.9) * mm, "end": v(-0.83, -20.08) * mm});
            skLineSegment(sketch, "E1247", {"start": v(-0.83, -20.08) * mm, "end": v(-0.83, -20.27) * mm});
            skLineSegment(sketch, "E1248", {"start": v(-0.83, -20.27) * mm, "end": v(-0.82, -20.46) * mm});
            skLineSegment(sketch, "E1249", {"start": v(-0.82, -20.46) * mm, "end": v(-0.82, -20.67) * mm});
            skLineSegment(sketch, "E1250", {"start": v(-0.82, -20.67) * mm, "end": v(-0.78, -20.87) * mm});
            skLineSegment(sketch, "E1251", {"start": v(-0.78, -20.87) * mm, "end": v(-0.68, -21.05) * mm});
            skLineSegment(sketch, "E1252", {"start": v(-0.68, -21.05) * mm, "end": v(-0.54, -21.2) * mm});
            skLineSegment(sketch, "E1253", {"start": v(-0.54, -21.2) * mm, "end": v(-0.37, -21.31) * mm});
            skLineSegment(sketch, "E1254", {"start": v(-0.37, -21.31) * mm, "end": v(-0.17, -21.37) * mm});
            skLineSegment(sketch, "E1255", {"start": v(-0.17, -21.37) * mm, "end": v(0.04, -21.38) * mm});
            skLineSegment(sketch, "E1256", {"start": v(0.04, -21.38) * mm, "end": v(0.24, -21.33) * mm});
            skLineSegment(sketch, "E1257", {"start": v(0.24, -21.33) * mm, "end": v(0.42, -21.23) * mm});
            skLineSegment(sketch, "E1258", {"start": v(0.42, -21.23) * mm, "end": v(0.57, -21.1) * mm});
            skLineSegment(sketch, "E1259", {"start": v(0.57, -21.1) * mm, "end": v(0.68, -20.92) * mm});
            skLineSegment(sketch, "E1260", {"start": v(0.68, -20.92) * mm, "end": v(0.73, -20.72) * mm});
            skLineSegment(sketch, "E1261", {"start": v(0.73, -20.72) * mm, "end": v(0.74, -20.55) * mm});
            skLineSegment(sketch, "E1262", {"start": v(0.74, -20.55) * mm, "end": v(0.72, -20.36) * mm});
            skLineSegment(sketch, "E1263", {"start": v(0.72, -20.36) * mm, "end": v(0.7, -20.17) * mm});
            skLineSegment(sketch, "E1264", {"start": v(0.7, -20.17) * mm, "end": v(0.69, -19.98) * mm});
            skLineSegment(sketch, "E1265", {"start": v(0.69, -19.98) * mm, "end": v(0.67, -19.8) * mm});
            skLineSegment(sketch, "E1266", {"start": v(0.67, -19.8) * mm, "end": v(0.66, -19.6) * mm});
            skLineSegment(sketch, "E1267", {"start": v(0.66, -19.6) * mm, "end": v(0.64, -19.41) * mm});
            skLineSegment(sketch, "E1268", {"start": v(0.64, -19.41) * mm, "end": v(0.62, -19.22) * mm});
            skLineSegment(sketch, "E1269", {"start": v(0.62, -19.22) * mm, "end": v(0.6, -19.04) * mm});
            skLineSegment(sketch, "E1270", {"start": v(0.6, -19.04) * mm, "end": v(0.6, -18.84) * mm});
            skLineSegment(sketch, "E1271", {"start": v(0.6, -18.84) * mm, "end": v(0.58, -18.66) * mm});
            skLineSegment(sketch, "E1272", {"start": v(0.58, -18.66) * mm, "end": v(0.56, -18.47) * mm});
            skLineSegment(sketch, "E1273", {"start": v(0.56, -18.47) * mm, "end": v(0.54, -18.27) * mm});
            skLineSegment(sketch, "E1274", {"start": v(0.54, -18.27) * mm, "end": v(0.53, -18.11) * mm});
            skLineSegment(sketch, "E1275", {"start": v(0.53, -18.11) * mm, "end": v(0.72, -18.08) * mm});
            skLineSegment(sketch, "E1276", {"start": v(0.72, -18.08) * mm, "end": v(0.9, -18.06) * mm});
            skLineSegment(sketch, "E1277", {"start": v(0.9, -18.06) * mm, "end": v(1.1, -18.03) * mm});
            skLineSegment(sketch, "E1278", {"start": v(1.1, -18.03) * mm, "end": v(1.28, -18) * mm});
            skLineSegment(sketch, "E1279", {"start": v(1.28, -18) * mm, "end": v(1.47, -17.98) * mm});
            skLineSegment(sketch, "E1280", {"start": v(1.47, -17.98) * mm, "end": v(1.65, -17.95) * mm});
            skLineSegment(sketch, "E1281", {"start": v(1.65, -17.95) * mm, "end": v(1.84, -17.92) * mm});
            skLineSegment(sketch, "E1282", {"start": v(1.84, -17.92) * mm, "end": v(2.03, -17.9) * mm});
            skLineSegment(sketch, "E1283", {"start": v(2.03, -17.9) * mm, "end": v(2.22, -17.87) * mm});
            skLineSegment(sketch, "E1284", {"start": v(2.22, -17.87) * mm, "end": v(2.4, -17.84) * mm});
            skLineSegment(sketch, "E1285", {"start": v(2.4, -17.84) * mm, "end": v(2.6, -17.82) * mm});
            skLineSegment(sketch, "E1286", {"start": v(2.6, -17.82) * mm, "end": v(2.63, -18) * mm});
            skLineSegment(sketch, "E1287", {"start": v(2.63, -18) * mm, "end": v(2.67, -18.19) * mm});
            skLineSegment(sketch, "E1288", {"start": v(2.67, -18.19) * mm, "end": v(2.7, -18.38) * mm});
            skLineSegment(sketch, "E1289", {"start": v(2.7, -18.38) * mm, "end": v(2.74, -18.56) * mm});
            skLineSegment(sketch, "E1290", {"start": v(2.74, -18.56) * mm, "end": v(2.78, -18.75) * mm});
            skLineSegment(sketch, "E1291", {"start": v(2.78, -18.75) * mm, "end": v(2.82, -18.94) * mm});
            skLineSegment(sketch, "E1292", {"start": v(2.82, -18.94) * mm, "end": v(2.85, -19.12) * mm});
            skLineSegment(sketch, "E1293", {"start": v(2.85, -19.12) * mm, "end": v(2.9, -19.3) * mm});
            skLineSegment(sketch, "E1294", {"start": v(2.9, -19.3) * mm, "end": v(2.93, -19.5) * mm});
            skLineSegment(sketch, "E1295", {"start": v(2.93, -19.5) * mm, "end": v(2.97, -19.68) * mm});
            skLineSegment(sketch, "E1296", {"start": v(2.97, -19.68) * mm, "end": v(3, -19.87) * mm});
            skLineSegment(sketch, "E1297", {"start": v(3, -19.87) * mm, "end": v(3.04, -20.06) * mm});
            skLineSegment(sketch, "E1298", {"start": v(3.04, -20.06) * mm, "end": v(3.09, -20.26) * mm});
            skLineSegment(sketch, "E1299", {"start": v(3.09, -20.26) * mm, "end": v(3.17, -20.45) * mm});
            skLineSegment(sketch, "E1300", {"start": v(3.17, -20.45) * mm, "end": v(3.3, -20.6) * mm});
            skLineSegment(sketch, "E1301", {"start": v(3.3, -20.6) * mm, "end": v(3.46, -20.73) * mm});
            skLineSegment(sketch, "E1302", {"start": v(3.46, -20.73) * mm, "end": v(3.65, -20.8) * mm});
            skLineSegment(sketch, "E1303", {"start": v(3.65, -20.8) * mm, "end": v(3.86, -20.83) * mm});
            skLineSegment(sketch, "E1304", {"start": v(3.86, -20.83) * mm, "end": v(4.06, -20.8) * mm});
            skLineSegment(sketch, "E1305", {"start": v(4.06, -20.8) * mm, "end": v(4.25, -20.7) * mm});
            skLineSegment(sketch, "E1306", {"start": v(4.25, -20.7) * mm, "end": v(4.41, -20.58) * mm});
            skLineSegment(sketch, "E1307", {"start": v(4.41, -20.58) * mm, "end": v(4.53, -20.4) * mm});
            skLineSegment(sketch, "E1308", {"start": v(4.53, -20.4) * mm, "end": v(4.6, -20.22) * mm});
            skLineSegment(sketch, "E1309", {"start": v(4.6, -20.22) * mm, "end": v(4.62, -20.01) * mm});
            skLineSegment(sketch, "E1310", {"start": v(4.62, -20.01) * mm, "end": v(4.6, -19.85) * mm});
            skLineSegment(sketch, "E1311", {"start": v(4.6, -19.85) * mm, "end": v(4.54, -19.66) * mm});
            skLineSegment(sketch, "E1312", {"start": v(4.54, -19.66) * mm, "end": v(4.5, -19.48) * mm});
            skLineSegment(sketch, "E1313", {"start": v(4.5, -19.48) * mm, "end": v(4.44, -19.3) * mm});
            skLineSegment(sketch, "E1314", {"start": v(4.44, -19.3) * mm, "end": v(4.39, -19.12) * mm});
            skLineSegment(sketch, "E1315", {"start": v(4.39, -19.12) * mm, "end": v(4.34, -18.93) * mm});
            skLineSegment(sketch, "E1316", {"start": v(4.34, -18.93) * mm, "end": v(4.28, -18.75) * mm});
            skLineSegment(sketch, "E1317", {"start": v(4.28, -18.75) * mm, "end": v(4.23, -18.57) * mm});
            skLineSegment(sketch, "E1318", {"start": v(4.23, -18.57) * mm, "end": v(4.18, -18.38) * mm});
            skLineSegment(sketch, "E1319", {"start": v(4.18, -18.38) * mm, "end": v(4.13, -18.2) * mm});
            skLineSegment(sketch, "E1320", {"start": v(4.13, -18.2) * mm, "end": v(4.08, -18.02) * mm});
            skLineSegment(sketch, "E1321", {"start": v(4.08, -18.02) * mm, "end": v(4.03, -17.83) * mm});
            skLineSegment(sketch, "E1322", {"start": v(4.03, -17.83) * mm, "end": v(3.97, -17.65) * mm});
            skLineSegment(sketch, "E1323", {"start": v(3.97, -17.65) * mm, "end": v(3.93, -17.5) * mm});
            skLineSegment(sketch, "E1324", {"start": v(3.93, -17.5) * mm, "end": v(4.1, -17.43) * mm});
            skLineSegment(sketch, "E1325", {"start": v(4.1, -17.43) * mm, "end": v(4.29, -17.37) * mm});
            skLineSegment(sketch, "E1326", {"start": v(4.29, -17.37) * mm, "end": v(4.47, -17.3) * mm});
            skLineSegment(sketch, "E1327", {"start": v(4.47, -17.3) * mm, "end": v(4.64, -17.24) * mm});
            skLineSegment(sketch, "E1328", {"start": v(4.64, -17.24) * mm, "end": v(4.82, -17.18) * mm});
            skLineSegment(sketch, "E1329", {"start": v(4.82, -17.18) * mm, "end": v(5, -17.12) * mm});
            skLineSegment(sketch, "E1330", {"start": v(5, -17.12) * mm, "end": v(5.18, -17.06) * mm});
            skLineSegment(sketch, "E1331", {"start": v(5.18, -17.06) * mm, "end": v(5.36, -17) * mm});
            skLineSegment(sketch, "E1332", {"start": v(5.36, -17) * mm, "end": v(5.54, -16.93) * mm});
            skLineSegment(sketch, "E1333", {"start": v(5.54, -16.93) * mm, "end": v(5.72, -16.87) * mm});
            skLineSegment(sketch, "E1334", {"start": v(5.72, -16.87) * mm, "end": v(5.9, -16.8) * mm});
            skLineSegment(sketch, "E1335", {"start": v(5.9, -16.8) * mm, "end": v(5.97, -16.98) * mm});
            skLineSegment(sketch, "E1336", {"start": v(5.97, -16.98) * mm, "end": v(6.04, -17.16) * mm});
            skLineSegment(sketch, "E1337", {"start": v(6.04, -17.16) * mm, "end": v(6.11, -17.34) * mm});
            skLineSegment(sketch, "E1338", {"start": v(6.11, -17.34) * mm, "end": v(6.19, -17.51) * mm});
            skLineSegment(sketch, "E1339", {"start": v(6.19, -17.51) * mm, "end": v(6.26, -17.69) * mm});
            skLineSegment(sketch, "E1340", {"start": v(6.26, -17.69) * mm, "end": v(6.33, -17.87) * mm});
            skLineSegment(sketch, "E1341", {"start": v(6.33, -17.87) * mm, "end": v(6.4, -18.04) * mm});
            skLineSegment(sketch, "E1342", {"start": v(6.4, -18.04) * mm, "end": v(6.48, -18.22) * mm});
            skLineSegment(sketch, "E1343", {"start": v(6.48, -18.22) * mm, "end": v(6.55, -18.4) * mm});
            skLineSegment(sketch, "E1344", {"start": v(6.55, -18.4) * mm, "end": v(6.62, -18.57) * mm});
            skLineSegment(sketch, "E1345", {"start": v(6.62, -18.57) * mm, "end": v(6.7, -18.75) * mm});
            skLineSegment(sketch, "E1346", {"start": v(6.7, -18.75) * mm, "end": v(6.77, -18.92) * mm});
            skLineSegment(sketch, "E1347", {"start": v(6.77, -18.92) * mm, "end": v(6.85, -19.11) * mm});
            skLineSegment(sketch, "E1348", {"start": v(6.85, -19.11) * mm, "end": v(6.96, -19.28) * mm});
            skLineSegment(sketch, "E1349", {"start": v(6.96, -19.28) * mm, "end": v(7.12, -19.42) * mm});
            skLineSegment(sketch, "E1350", {"start": v(7.12, -19.42) * mm, "end": v(7.3, -19.5) * mm});
            skLineSegment(sketch, "E1351", {"start": v(7.3, -19.5) * mm, "end": v(7.5, -19.54) * mm});
            skLineSegment(sketch, "E1352", {"start": v(7.5, -19.54) * mm, "end": v(7.71, -19.53) * mm});
            skLineSegment(sketch, "E1353", {"start": v(7.71, -19.53) * mm, "end": v(7.87, -19.47) * mm});
            skLineSegment(sketch, "E1354", {"start": v(7.87, -19.47) * mm, "end": v(8.04, -19.36) * mm});
            skLineSegment(sketch, "E1355", {"start": v(8.04, -19.36) * mm, "end": v(8.18, -19.21) * mm});
            skLineSegment(sketch, "E1356", {"start": v(8.18, -19.21) * mm, "end": v(8.28, -19.03) * mm});
            skLineSegment(sketch, "E1357", {"start": v(8.28, -19.03) * mm, "end": v(8.32, -18.83) * mm});
            skLineSegment(sketch, "E1358", {"start": v(8.32, -18.83) * mm, "end": v(8.31, -18.62) * mm});
            skLineSegment(sketch, "E1359", {"start": v(8.31, -18.62) * mm, "end": v(8.25, -18.43) * mm});
            skLineSegment(sketch, "E1360", {"start": v(8.25, -18.43) * mm, "end": v(8.16, -18.26) * mm});
            skLineSegment(sketch, "E1361", {"start": v(8.16, -18.26) * mm, "end": v(8.08, -18.09) * mm});
            skLineSegment(sketch, "E1362", {"start": v(8.08, -18.09) * mm, "end": v(8, -17.91) * mm});
            skLineSegment(sketch, "E1363", {"start": v(8, -17.91) * mm, "end": v(7.9, -17.75) * mm});
            skLineSegment(sketch, "E1364", {"start": v(7.9, -17.75) * mm, "end": v(7.82, -17.58) * mm});
            skLineSegment(sketch, "E1365", {"start": v(7.82, -17.58) * mm, "end": v(7.74, -17.4) * mm});
            skLineSegment(sketch, "E1366", {"start": v(7.74, -17.4) * mm, "end": v(7.65, -17.24) * mm});
            skLineSegment(sketch, "E1367", {"start": v(7.65, -17.24) * mm, "end": v(7.57, -17.07) * mm});
            skLineSegment(sketch, "E1368", {"start": v(7.57, -17.07) * mm, "end": v(7.48, -16.9) * mm});
            skLineSegment(sketch, "E1369", {"start": v(7.48, -16.9) * mm, "end": v(7.4, -16.72) * mm});
            skLineSegment(sketch, "E1370", {"start": v(7.4, -16.72) * mm, "end": v(7.3, -16.56) * mm});
            skLineSegment(sketch, "E1371", {"start": v(7.3, -16.56) * mm, "end": v(7.22, -16.38) * mm});
            skLineSegment(sketch, "E1372", {"start": v(7.22, -16.38) * mm, "end": v(7.15, -16.24) * mm});
            skLineSegment(sketch, "E1373", {"start": v(7.15, -16.24) * mm, "end": v(7.31, -16.14) * mm});
            skLineSegment(sketch, "E1374", {"start": v(7.31, -16.14) * mm, "end": v(7.48, -16.05) * mm});
            skLineSegment(sketch, "E1375", {"start": v(7.48, -16.05) * mm, "end": v(7.64, -15.95) * mm});
            skLineSegment(sketch, "E1376", {"start": v(7.64, -15.95) * mm, "end": v(7.8, -15.86) * mm});
            skLineSegment(sketch, "E1377", {"start": v(7.8, -15.86) * mm, "end": v(7.97, -15.76) * mm});
            skLineSegment(sketch, "E1378", {"start": v(7.97, -15.76) * mm, "end": v(8.13, -15.67) * mm});
            skLineSegment(sketch, "E1379", {"start": v(8.13, -15.67) * mm, "end": v(8.3, -15.58) * mm});
            skLineSegment(sketch, "E1380", {"start": v(8.3, -15.58) * mm, "end": v(8.46, -15.48) * mm});
            skLineSegment(sketch, "E1381", {"start": v(8.46, -15.48) * mm, "end": v(8.62, -15.39) * mm});
            skLineSegment(sketch, "E1382", {"start": v(8.62, -15.39) * mm, "end": v(8.79, -15.3) * mm});
            skLineSegment(sketch, "E1383", {"start": v(8.79, -15.3) * mm, "end": v(8.95, -15.2) * mm});
            skLineSegment(sketch, "E1384", {"start": v(8.95, -15.2) * mm, "end": v(9.06, -15.36) * mm});
            skLineSegment(sketch, "E1385", {"start": v(9.06, -15.36) * mm, "end": v(9.16, -15.51) * mm});
            skLineSegment(sketch, "E1386", {"start": v(9.16, -15.51) * mm, "end": v(9.27, -15.67) * mm});
            skLineSegment(sketch, "E1387", {"start": v(9.27, -15.67) * mm, "end": v(9.37, -15.83) * mm});
            skLineSegment(sketch, "E1388", {"start": v(9.37, -15.83) * mm, "end": v(9.47, -16) * mm});
            skLineSegment(sketch, "E1389", {"start": v(9.47, -16) * mm, "end": v(9.58, -16.15) * mm});
            skLineSegment(sketch, "E1390", {"start": v(9.58, -16.15) * mm, "end": v(9.68, -16.31) * mm});
            skLineSegment(sketch, "E1391", {"start": v(9.68, -16.31) * mm, "end": v(9.79, -16.47) * mm});
            skLineSegment(sketch, "E1392", {"start": v(9.79, -16.47) * mm, "end": v(9.9, -16.63) * mm});
            skLineSegment(sketch, "E1393", {"start": v(9.9, -16.63) * mm, "end": v(10, -16.79) * mm});
            skLineSegment(sketch, "E1394", {"start": v(10, -16.79) * mm, "end": v(10.1, -16.95) * mm});
            skLineSegment(sketch, "E1395", {"start": v(10.1, -16.95) * mm, "end": v(10.2, -17.1) * mm});
            skLineSegment(sketch, "E1396", {"start": v(10.2, -17.1) * mm, "end": v(10.32, -17.28) * mm});
            skLineSegment(sketch, "E1397", {"start": v(10.32, -17.28) * mm, "end": v(10.47, -17.42) * mm});
            skLineSegment(sketch, "E1398", {"start": v(10.47, -17.42) * mm, "end": v(10.65, -17.53) * mm});
            skLineSegment(sketch, "E1399", {"start": v(10.65, -17.53) * mm, "end": v(10.84, -17.58) * mm});
            skLineSegment(sketch, "E1400", {"start": v(10.84, -17.58) * mm, "end": v(11.05, -17.58) * mm});
            skLineSegment(sketch, "E1401", {"start": v(11.05, -17.58) * mm, "end": v(11.25, -17.52) * mm});
            skLineSegment(sketch, "E1402", {"start": v(11.25, -17.52) * mm, "end": v(11.4, -17.44) * mm});
            skLineSegment(sketch, "E1403", {"start": v(11.4, -17.44) * mm, "end": v(11.55, -17.3) * mm});
            skLineSegment(sketch, "E1404", {"start": v(11.55, -17.3) * mm, "end": v(11.65, -17.12) * mm});
            skLineSegment(sketch, "E1405", {"start": v(11.65, -17.12) * mm, "end": v(11.71, -16.92) * mm});
            skLineSegment(sketch, "E1406", {"start": v(11.71, -16.92) * mm, "end": v(11.72, -16.72) * mm});
            skLineSegment(sketch, "E1407", {"start": v(11.72, -16.72) * mm, "end": v(11.67, -16.52) * mm});
            skLineSegment(sketch, "E1408", {"start": v(11.67, -16.52) * mm, "end": v(11.57, -16.34) * mm});
            skLineSegment(sketch, "E1409", {"start": v(11.57, -16.34) * mm, "end": v(11.45, -16.19) * mm});
            skLineSegment(sketch, "E1410", {"start": v(11.45, -16.19) * mm, "end": v(11.34, -16.04) * mm});
            skLineSegment(sketch, "E1411", {"start": v(11.34, -16.04) * mm, "end": v(11.22, -15.88) * mm});
            skLineSegment(sketch, "E1412", {"start": v(11.22, -15.88) * mm, "end": v(11.1, -15.73) * mm});
            skLineSegment(sketch, "E1413", {"start": v(11.1, -15.73) * mm, "end": v(10.99, -15.58) * mm});
            skLineSegment(sketch, "E1414", {"start": v(10.99, -15.58) * mm, "end": v(10.87, -15.43) * mm});
            skLineSegment(sketch, "E1415", {"start": v(10.87, -15.43) * mm, "end": v(10.76, -15.28) * mm});
            skLineSegment(sketch, "E1416", {"start": v(10.76, -15.28) * mm, "end": v(10.64, -15.13) * mm});
            skLineSegment(sketch, "E1417", {"start": v(10.64, -15.13) * mm, "end": v(10.52, -14.98) * mm});
            skLineSegment(sketch, "E1418", {"start": v(10.52, -14.98) * mm, "end": v(10.4, -14.83) * mm});
            skLineSegment(sketch, "E1419", {"start": v(10.4, -14.83) * mm, "end": v(10.3, -14.68) * mm});
            skLineSegment(sketch, "E1420", {"start": v(10.3, -14.68) * mm, "end": v(10.17, -14.53) * mm});
            skLineSegment(sketch, "E1421", {"start": v(10.17, -14.53) * mm, "end": v(10.07, -14.4) * mm});
            skLineSegment(sketch, "E1422", {"start": v(10.07, -14.4) * mm, "end": v(10.22, -14.27) * mm});
            skLineSegment(sketch, "E1423", {"start": v(10.22, -14.27) * mm, "end": v(10.36, -14.15) * mm});
            skLineSegment(sketch, "E1424", {"start": v(10.36, -14.15) * mm, "end": v(10.5, -14.03) * mm});
            skLineSegment(sketch, "E1425", {"start": v(10.5, -14.03) * mm, "end": v(10.65, -13.9) * mm});
            skLineSegment(sketch, "E1426", {"start": v(10.65, -13.9) * mm, "end": v(10.79, -13.78) * mm});
            skLineSegment(sketch, "E1427", {"start": v(10.79, -13.78) * mm, "end": v(10.93, -13.65) * mm});
            skLineSegment(sketch, "E1428", {"start": v(10.93, -13.65) * mm, "end": v(11.08, -13.53) * mm});
            skLineSegment(sketch, "E1429", {"start": v(11.08, -13.53) * mm, "end": v(11.22, -13.4) * mm});
            skLineSegment(sketch, "E1430", {"start": v(11.22, -13.4) * mm, "end": v(11.36, -13.28) * mm});
            skLineSegment(sketch, "E1431", {"start": v(11.36, -13.28) * mm, "end": v(11.5, -13.16) * mm});
            skLineSegment(sketch, "E1432", {"start": v(11.5, -13.16) * mm, "end": v(11.65, -13.03) * mm});
            skLineSegment(sketch, "E1433", {"start": v(11.65, -13.03) * mm, "end": v(11.78, -13.17) * mm});
            skLineSegment(sketch, "E1434", {"start": v(11.78, -13.17) * mm, "end": v(11.91, -13.3) * mm});
            skLineSegment(sketch, "E1435", {"start": v(11.91, -13.3) * mm, "end": v(12.05, -13.44) * mm});
            skLineSegment(sketch, "E1436", {"start": v(12.05, -13.44) * mm, "end": v(12.18, -13.58) * mm});
            skLineSegment(sketch, "E1437", {"start": v(12.18, -13.58) * mm, "end": v(12.3, -13.72) * mm});
            skLineSegment(sketch, "E1438", {"start": v(12.3, -13.72) * mm, "end": v(12.44, -13.85) * mm});
            skLineSegment(sketch, "E1439", {"start": v(12.44, -13.85) * mm, "end": v(12.58, -13.99) * mm});
            skLineSegment(sketch, "E1440", {"start": v(12.58, -13.99) * mm, "end": v(12.7, -14.13) * mm});
            skLineSegment(sketch, "E1441", {"start": v(12.7, -14.13) * mm, "end": v(12.84, -14.26) * mm});
            skLineSegment(sketch, "E1442", {"start": v(12.84, -14.26) * mm, "end": v(12.97, -14.4) * mm});
            skLineSegment(sketch, "E1443", {"start": v(12.97, -14.4) * mm, "end": v(13.1, -14.53) * mm});
            skLineSegment(sketch, "E1444", {"start": v(13.1, -14.53) * mm, "end": v(13.24, -14.67) * mm});
            skLineSegment(sketch, "E1445", {"start": v(13.24, -14.67) * mm, "end": v(13.38, -14.82) * mm});
            skLineSegment(sketch, "E1446", {"start": v(13.38, -14.82) * mm, "end": v(13.56, -14.93) * mm});
            skLineSegment(sketch, "E1447", {"start": v(13.56, -14.93) * mm, "end": v(13.75, -15) * mm});
            skLineSegment(sketch, "E1448", {"start": v(13.75, -15) * mm, "end": v(13.96, -15.01) * mm});
            skLineSegment(sketch, "E1449", {"start": v(13.96, -15.01) * mm, "end": v(14.16, -14.97) * mm});
            skLineSegment(sketch, "E1450", {"start": v(14.16, -14.97) * mm, "end": v(14.34, -14.88) * mm});
            skLineSegment(sketch, "E1451", {"start": v(14.34, -14.88) * mm, "end": v(14.47, -14.77) * mm});
            skLineSegment(sketch, "E1452", {"start": v(14.47, -14.77) * mm, "end": v(14.6, -14.6) * mm});
            skLineSegment(sketch, "E1453", {"start": v(14.6, -14.6) * mm, "end": v(14.66, -14.41) * mm});
            skLineSegment(sketch, "E1454", {"start": v(14.66, -14.41) * mm, "end": v(14.69, -14.2) * mm});
            skLineSegment(sketch, "E1455", {"start": v(14.69, -14.2) * mm, "end": v(14.65, -14) * mm});
            skLineSegment(sketch, "E1456", {"start": v(14.65, -14) * mm, "end": v(14.57, -13.82) * mm});
            skLineSegment(sketch, "E1457", {"start": v(14.57, -13.82) * mm, "end": v(14.43, -13.66) * mm});
            skLineSegment(sketch, "E1458", {"start": v(14.43, -13.66) * mm, "end": v(14.3, -13.53) * mm});
            skLineSegment(sketch, "E1459", {"start": v(14.3, -13.53) * mm, "end": v(14.15, -13.4) * mm});
            skLineSegment(sketch, "E1460", {"start": v(14.15, -13.4) * mm, "end": v(14, -13.28) * mm});
            skLineSegment(sketch, "E1461", {"start": v(14, -13.28) * mm, "end": v(13.86, -13.16) * mm});
            skLineSegment(sketch, "E1462", {"start": v(13.86, -13.16) * mm, "end": v(13.72, -13.03) * mm});
            skLineSegment(sketch, "E1463", {"start": v(13.72, -13.03) * mm, "end": v(13.58, -12.9) * mm});
            skLineSegment(sketch, "E1464", {"start": v(13.58, -12.9) * mm, "end": v(13.43, -12.78) * mm});
            skLineSegment(sketch, "E1465", {"start": v(13.43, -12.78) * mm, "end": v(13.3, -12.65) * mm});
            skLineSegment(sketch, "E1466", {"start": v(13.3, -12.65) * mm, "end": v(13.15, -12.52) * mm});
            skLineSegment(sketch, "E1467", {"start": v(13.15, -12.52) * mm, "end": v(13, -12.4) * mm});
            skLineSegment(sketch, "E1468", {"start": v(13, -12.4) * mm, "end": v(12.86, -12.27) * mm});
            skLineSegment(sketch, "E1469", {"start": v(12.86, -12.27) * mm, "end": v(12.72, -12.15) * mm});
            skLineSegment(sketch, "E1470", {"start": v(12.72, -12.15) * mm, "end": v(12.6, -12.04) * mm});
            skLineSegment(sketch, "E1471", {"start": v(12.6, -12.04) * mm, "end": v(12.71, -11.89) * mm});
            skLineSegment(sketch, "E1472", {"start": v(12.71, -11.89) * mm, "end": v(12.83, -11.74) * mm});
            skLineSegment(sketch, "E1473", {"start": v(12.83, -11.74) * mm, "end": v(12.95, -11.6) * mm});
            skLineSegment(sketch, "E1474", {"start": v(12.95, -11.6) * mm, "end": v(13.07, -11.44) * mm});
            skLineSegment(sketch, "E1475", {"start": v(13.07, -11.44) * mm, "end": v(13.18, -11.3) * mm});
            skLineSegment(sketch, "E1476", {"start": v(13.18, -11.3) * mm, "end": v(13.3, -11.14) * mm});
            skLineSegment(sketch, "E1477", {"start": v(13.3, -11.14) * mm, "end": v(13.42, -11) * mm});
            skLineSegment(sketch, "E1478", {"start": v(13.42, -11) * mm, "end": v(13.53, -10.85) * mm});
            skLineSegment(sketch, "E1479", {"start": v(13.53, -10.85) * mm, "end": v(13.65, -10.7) * mm});
            skLineSegment(sketch, "E1480", {"start": v(13.65, -10.7) * mm, "end": v(13.77, -10.55) * mm});
            skLineSegment(sketch, "E1481", {"start": v(13.77, -10.55) * mm, "end": v(13.88, -10.4) * mm});
            skLineSegment(sketch, "E1482", {"start": v(13.88, -10.4) * mm, "end": v(14.04, -10.5) * mm});
            skLineSegment(sketch, "E1483", {"start": v(14.04, -10.5) * mm, "end": v(14.2, -10.62) * mm});
            skLineSegment(sketch, "E1484", {"start": v(14.2, -10.62) * mm, "end": v(14.35, -10.73) * mm});
            skLineSegment(sketch, "E1485", {"start": v(14.35, -10.73) * mm, "end": v(14.5, -10.84) * mm});
            skLineSegment(sketch, "E1486", {"start": v(14.5, -10.84) * mm, "end": v(14.66, -10.94) * mm});
            skLineSegment(sketch, "E1487", {"start": v(14.66, -10.94) * mm, "end": v(14.82, -11.05) * mm});
            skLineSegment(sketch, "E1488", {"start": v(14.82, -11.05) * mm, "end": v(14.98, -11.16) * mm});
            skLineSegment(sketch, "E1489", {"start": v(14.98, -11.16) * mm, "end": v(15.13, -11.27) * mm});
            skLineSegment(sketch, "E1490", {"start": v(15.13, -11.27) * mm, "end": v(15.3, -11.38) * mm});
            skLineSegment(sketch, "E1491", {"start": v(15.3, -11.38) * mm, "end": v(15.45, -11.5) * mm});
            skLineSegment(sketch, "E1492", {"start": v(15.45, -11.5) * mm, "end": v(15.6, -11.6) * mm});
            skLineSegment(sketch, "E1493", {"start": v(15.6, -11.6) * mm, "end": v(15.76, -11.7) * mm});
            skLineSegment(sketch, "E1494", {"start": v(15.76, -11.7) * mm, "end": v(15.93, -11.82) * mm});
            skLineSegment(sketch, "E1495", {"start": v(15.93, -11.82) * mm, "end": v(16.12, -11.9) * mm});
            skLineSegment(sketch, "E1496", {"start": v(16.12, -11.9) * mm, "end": v(16.32, -11.93) * mm});
            skLineSegment(sketch, "E1497", {"start": v(16.32, -11.93) * mm, "end": v(16.53, -11.9) * mm});
            skLineSegment(sketch, "E1498", {"start": v(16.53, -11.9) * mm, "end": v(16.72, -11.83) * mm});
            skLineSegment(sketch, "E1499", {"start": v(16.72, -11.83) * mm, "end": v(16.88, -11.7) * mm});
            skLineSegment(sketch, "E1500", {"start": v(16.88, -11.7) * mm, "end": v(16.99, -11.58) * mm});
            skLineSegment(sketch, "E1501", {"start": v(16.99, -11.58) * mm, "end": v(17.07, -11.39) * mm});
            skLineSegment(sketch, "E1502", {"start": v(17.07, -11.39) * mm, "end": v(17.1, -11.18) * mm});
            skLineSegment(sketch, "E1503", {"start": v(17.1, -11.18) * mm, "end": v(17.1, -10.98) * mm});
            skLineSegment(sketch, "E1504", {"start": v(17.1, -10.98) * mm, "end": v(17.02, -10.79) * mm});
            skLineSegment(sketch, "E1505", {"start": v(17.02, -10.79) * mm, "end": v(16.9, -10.62) * mm});
            skLineSegment(sketch, "E1506", {"start": v(16.9, -10.62) * mm, "end": v(16.74, -10.49) * mm});
            skLineSegment(sketch, "E1507", {"start": v(16.74, -10.49) * mm, "end": v(16.58, -10.4) * mm});
            skLineSegment(sketch, "E1508", {"start": v(16.58, -10.4) * mm, "end": v(16.41, -10.3) * mm});
            skLineSegment(sketch, "E1509", {"start": v(16.41, -10.3) * mm, "end": v(16.25, -10.2) * mm});
            skLineSegment(sketch, "E1510", {"start": v(16.25, -10.2) * mm, "end": v(16.08, -10.1) * mm});
            skLineSegment(sketch, "E1511", {"start": v(16.08, -10.1) * mm, "end": v(15.92, -10) * mm});
            skLineSegment(sketch, "E1512", {"start": v(15.92, -10) * mm, "end": v(15.75, -9.9) * mm});
            skLineSegment(sketch, "E1513", {"start": v(15.75, -9.9) * mm, "end": v(15.6, -9.81) * mm});
            skLineSegment(sketch, "E1514", {"start": v(15.6, -9.81) * mm, "end": v(15.43, -9.71) * mm});
            skLineSegment(sketch, "E1515", {"start": v(15.43, -9.71) * mm, "end": v(15.26, -9.62) * mm});
            skLineSegment(sketch, "E1516", {"start": v(15.26, -9.62) * mm, "end": v(15.1, -9.52) * mm});
            skLineSegment(sketch, "E1517", {"start": v(15.1, -9.52) * mm, "end": v(14.94, -9.42) * mm});
            skLineSegment(sketch, "E1518", {"start": v(14.94, -9.42) * mm, "end": v(14.77, -9.33) * mm});
            skLineSegment(sketch, "E1519", {"start": v(14.77, -9.33) * mm, "end": v(14.63, -9.24) * mm});
            skLineSegment(sketch, "E1520", {"start": v(14.63, -9.24) * mm, "end": v(14.72, -9.07) * mm});
            skLineSegment(sketch, "E1521", {"start": v(14.72, -9.07) * mm, "end": v(14.8, -8.9) * mm});
            skLineSegment(sketch, "E1522", {"start": v(14.8, -8.9) * mm, "end": v(14.89, -8.74) * mm});
            skLineSegment(sketch, "E1523", {"start": v(14.89, -8.74) * mm, "end": v(14.98, -8.57) * mm});
            skLineSegment(sketch, "E1524", {"start": v(14.98, -8.57) * mm, "end": v(15.06, -8.4) * mm});
            skLineSegment(sketch, "E1525", {"start": v(15.06, -8.4) * mm, "end": v(15.15, -8.23) * mm});
            skLineSegment(sketch, "E1526", {"start": v(15.15, -8.23) * mm, "end": v(15.24, -8.06) * mm});
            skLineSegment(sketch, "E1527", {"start": v(15.24, -8.06) * mm, "end": v(15.32, -7.9) * mm});
            skLineSegment(sketch, "E1528", {"start": v(15.32, -7.9) * mm, "end": v(15.41, -7.73) * mm});
            skLineSegment(sketch, "E1529", {"start": v(15.41, -7.73) * mm, "end": v(15.5, -7.56) * mm});
            skLineSegment(sketch, "E1530", {"start": v(15.5, -7.56) * mm, "end": v(15.58, -7.4) * mm});
            skLineSegment(sketch, "E1531", {"start": v(15.58, -7.4) * mm, "end": v(15.76, -7.47) * mm});
            skLineSegment(sketch, "E1532", {"start": v(15.76, -7.47) * mm, "end": v(15.93, -7.55) * mm});
            skLineSegment(sketch, "E1533", {"start": v(15.93, -7.55) * mm, "end": v(16.1, -7.62) * mm});
            skLineSegment(sketch, "E1534", {"start": v(16.1, -7.62) * mm, "end": v(16.28, -7.7) * mm});
            skLineSegment(sketch, "E1535", {"start": v(16.28, -7.7) * mm, "end": v(16.45, -7.78) * mm});
            skLineSegment(sketch, "E1536", {"start": v(16.45, -7.78) * mm, "end": v(16.63, -7.86) * mm});
            skLineSegment(sketch, "E1537", {"start": v(16.63, -7.86) * mm, "end": v(16.8, -7.93) * mm});
            skLineSegment(sketch, "E1538", {"start": v(16.8, -7.93) * mm, "end": v(16.97, -8.01) * mm});
            skLineSegment(sketch, "E1539", {"start": v(16.97, -8.01) * mm, "end": v(17.15, -8.09) * mm});
            skLineSegment(sketch, "E1540", {"start": v(17.15, -8.09) * mm, "end": v(17.32, -8.17) * mm});
            skLineSegment(sketch, "E1541", {"start": v(17.32, -8.17) * mm, "end": v(17.5, -8.24) * mm});
            skLineSegment(sketch, "E1542", {"start": v(17.5, -8.24) * mm, "end": v(17.67, -8.32) * mm});
            skLineSegment(sketch, "E1543", {"start": v(17.67, -8.32) * mm, "end": v(17.86, -8.4) * mm});
            skLineSegment(sketch, "E1544", {"start": v(17.86, -8.4) * mm, "end": v(18.06, -8.45) * mm});
            skLineSegment(sketch, "E1545", {"start": v(18.06, -8.45) * mm, "end": v(18.27, -8.44) * mm});
            skLineSegment(sketch, "E1546", {"start": v(18.27, -8.44) * mm, "end": v(18.46, -8.37) * mm});
            skLineSegment(sketch, "E1547", {"start": v(18.46, -8.37) * mm, "end": v(18.64, -8.26) * mm});
            skLineSegment(sketch, "E1548", {"start": v(18.64, -8.26) * mm, "end": v(18.77, -8.1) * mm});
            skLineSegment(sketch, "E1549", {"start": v(18.77, -8.1) * mm, "end": v(18.85, -7.96) * mm});
            skLineSegment(sketch, "E1550", {"start": v(18.85, -7.96) * mm, "end": v(18.9, -7.76) * mm});
            skLineSegment(sketch, "E1551", {"start": v(18.9, -7.76) * mm, "end": v(18.9, -7.55) * mm});
            skLineSegment(sketch, "E1552", {"start": v(18.9, -7.55) * mm, "end": v(18.84, -7.35) * mm});
            skLineSegment(sketch, "E1553", {"start": v(18.84, -7.35) * mm, "end": v(18.73, -7.18) * mm});
            skLineSegment(sketch, "E1554", {"start": v(18.73, -7.18) * mm, "end": v(18.58, -7.03) * mm});
            skLineSegment(sketch, "E1555", {"start": v(18.58, -7.03) * mm, "end": v(18.4, -6.94) * mm});
            skLineSegment(sketch, "E1556", {"start": v(18.4, -6.94) * mm, "end": v(18.22, -6.87) * mm});
            skLineSegment(sketch, "E1557", {"start": v(18.22, -6.87) * mm, "end": v(18.05, -6.8) * mm});
            skLineSegment(sketch, "E1558", {"start": v(18.05, -6.8) * mm, "end": v(17.86, -6.74) * mm});
            skLineSegment(sketch, "E1559", {"start": v(17.86, -6.74) * mm, "end": v(17.69, -6.68) * mm});
            skLineSegment(sketch, "E1560", {"start": v(17.69, -6.68) * mm, "end": v(17.5, -6.62) * mm});
            skLineSegment(sketch, "E1561", {"start": v(17.5, -6.62) * mm, "end": v(17.33, -6.55) * mm});
            skLineSegment(sketch, "E1562", {"start": v(17.33, -6.55) * mm, "end": v(17.15, -6.49) * mm});
            skLineSegment(sketch, "E1563", {"start": v(17.15, -6.49) * mm, "end": v(16.97, -6.43) * mm});
            skLineSegment(sketch, "E1564", {"start": v(16.97, -6.43) * mm, "end": v(16.79, -6.36) * mm});
            skLineSegment(sketch, "E1565", {"start": v(16.79, -6.36) * mm, "end": v(16.6, -6.3) * mm});
            skLineSegment(sketch, "E1566", {"start": v(16.6, -6.3) * mm, "end": v(16.43, -6.23) * mm});
            skLineSegment(sketch, "E1567", {"start": v(16.43, -6.23) * mm, "end": v(16.25, -6.17) * mm});
            skLineSegment(sketch, "E1568", {"start": v(16.25, -6.17) * mm, "end": v(16.1, -6.11) * mm});
            skLineSegment(sketch, "E1569", {"start": v(16.1, -6.11) * mm, "end": v(16.15, -5.93) * mm});
            skLineSegment(sketch, "E1570", {"start": v(16.15, -5.93) * mm, "end": v(16.2, -5.75) * mm});
            skLineSegment(sketch, "E1571", {"start": v(16.2, -5.75) * mm, "end": v(16.26, -5.57) * mm});
            skLineSegment(sketch, "E1572", {"start": v(16.26, -5.57) * mm, "end": v(16.3, -5.39) * mm});
            skLineSegment(sketch, "E1573", {"start": v(16.3, -5.39) * mm, "end": v(16.36, -5.2) * mm});
            skLineSegment(sketch, "E1574", {"start": v(16.36, -5.2) * mm, "end": v(16.42, -5.02) * mm});
            skLineSegment(sketch, "E1575", {"start": v(16.42, -5.02) * mm, "end": v(16.47, -4.84) * mm});
            skLineSegment(sketch, "E1576", {"start": v(16.47, -4.84) * mm, "end": v(16.52, -4.66) * mm});
            skLineSegment(sketch, "E1577", {"start": v(16.52, -4.66) * mm, "end": v(16.58, -4.48) * mm});
            skLineSegment(sketch, "E1578", {"start": v(16.58, -4.48) * mm, "end": v(16.63, -4.3) * mm});
            skLineSegment(sketch, "E1579", {"start": v(16.63, -4.3) * mm, "end": v(16.68, -4.12) * mm});
            skLineSegment(sketch, "E1580", {"start": v(16.68, -4.12) * mm, "end": v(16.87, -4.16) * mm});
            skLineSegment(sketch, "E1581", {"start": v(16.87, -4.16) * mm, "end": v(17.05, -4.2) * mm});
            skLineSegment(sketch, "E1582", {"start": v(17.05, -4.2) * mm, "end": v(17.24, -4.24) * mm});
            skLineSegment(sketch, "E1583", {"start": v(17.24, -4.24) * mm, "end": v(17.42, -4.29) * mm});
            skLineSegment(sketch, "E1584", {"start": v(17.42, -4.29) * mm, "end": v(17.6, -4.33) * mm});
            skLineSegment(sketch, "E1585", {"start": v(17.6, -4.33) * mm, "end": v(17.8, -4.37) * mm});
            skLineSegment(sketch, "E1586", {"start": v(17.8, -4.37) * mm, "end": v(17.98, -4.42) * mm});
            skLineSegment(sketch, "E1587", {"start": v(17.98, -4.42) * mm, "end": v(18.16, -4.46) * mm});
            skLineSegment(sketch, "E1588", {"start": v(18.16, -4.46) * mm, "end": v(18.35, -4.5) * mm});
            skLineSegment(sketch, "E1589", {"start": v(18.35, -4.5) * mm, "end": v(18.54, -4.55) * mm});
            skLineSegment(sketch, "E1590", {"start": v(18.54, -4.55) * mm, "end": v(18.72, -4.59) * mm});
            skLineSegment(sketch, "E1591", {"start": v(18.72, -4.59) * mm, "end": v(18.9, -4.63) * mm});
            skLineSegment(sketch, "E1592", {"start": v(18.9, -4.63) * mm, "end": v(19.1, -4.68) * mm});
            skLineSegment(sketch, "E1593", {"start": v(19.1, -4.68) * mm, "end": v(19.31, -4.68) * mm});
            skLineSegment(sketch, "E1594", {"start": v(19.31, -4.68) * mm, "end": v(19.51, -4.63) * mm});
            skLineSegment(sketch, "E1595", {"start": v(19.51, -4.63) * mm, "end": v(19.7, -4.53) * mm});
            skLineSegment(sketch, "E1596", {"start": v(19.7, -4.53) * mm, "end": v(19.84, -4.39) * mm});
            skLineSegment(sketch, "E1597", {"start": v(19.84, -4.39) * mm, "end": v(19.95, -4.21) * mm});
            skLineSegment(sketch, "E1598", {"start": v(19.95, -4.21) * mm, "end": v(20, -4.05) * mm});
            skLineSegment(sketch, "E1599", {"start": v(20, -4.05) * mm, "end": v(20, -3.85) * mm});
            skLineSegment(sketch, "E1600", {"start": v(20, -3.85) * mm, "end": v(19.97, -3.64) * mm});
            skLineSegment(sketch, "E1601", {"start": v(19.97, -3.64) * mm, "end": v(19.87, -3.46) * mm});
            skLineSegment(sketch, "E1602", {"start": v(19.87, -3.46) * mm, "end": v(19.73, -3.3) * mm});
            skLineSegment(sketch, "E1603", {"start": v(19.73, -3.3) * mm, "end": v(19.56, -3.2) * mm});
            skLineSegment(sketch, "E1604", {"start": v(19.56, -3.2) * mm, "end": v(19.36, -3.14) * mm});
            skLineSegment(sketch, "E1605", {"start": v(19.36, -3.14) * mm, "end": v(19.18, -3.1) * mm});
            skLineSegment(sketch, "E1606", {"start": v(19.18, -3.1) * mm, "end": v(18.99, -3.08) * mm});
            skLineSegment(sketch, "E1607", {"start": v(18.99, -3.08) * mm, "end": v(18.8, -3.05) * mm});
            skLineSegment(sketch, "E1608", {"start": v(18.8, -3.05) * mm, "end": v(18.61, -3.02) * mm});
            skLineSegment(sketch, "E1609", {"start": v(18.61, -3.02) * mm, "end": v(18.42, -3) * mm});
            skLineSegment(sketch, "E1610", {"start": v(18.42, -3) * mm, "end": v(18.23, -2.96) * mm});
            skLineSegment(sketch, "E1611", {"start": v(18.23, -2.96) * mm, "end": v(18.05, -2.93) * mm});
            skLineSegment(sketch, "E1612", {"start": v(18.05, -2.93) * mm, "end": v(17.86, -2.9) * mm});
            skLineSegment(sketch, "E1613", {"start": v(17.86, -2.9) * mm, "end": v(17.67, -2.87) * mm});
            skLineSegment(sketch, "E1614", {"start": v(17.67, -2.87) * mm, "end": v(17.48, -2.85) * mm});
            skLineSegment(sketch, "E1615", {"start": v(17.48, -2.85) * mm, "end": v(17.3, -2.82) * mm});
            skLineSegment(sketch, "E1616", {"start": v(17.3, -2.82) * mm, "end": v(17.1, -2.79) * mm});
            skLineSegment(sketch, "E1617", {"start": v(17.1, -2.79) * mm, "end": v(16.94, -2.76) * mm});
            skLineSegment(sketch, "E1618", {"start": v(16.94, -2.76) * mm, "end": v(16.96, -2.57) * mm});
            skLineSegment(sketch, "E1619", {"start": v(16.96, -2.57) * mm, "end": v(16.98, -2.39) * mm});
            skLineSegment(sketch, "E1620", {"start": v(16.98, -2.39) * mm, "end": v(17, -2.2) * mm});
            skLineSegment(sketch, "E1621", {"start": v(17, -2.2) * mm, "end": v(17.01, -2) * mm});
            skLineSegment(sketch, "E1622", {"start": v(17.01, -2) * mm, "end": v(17.03, -1.82) * mm});
            skLineSegment(sketch, "E1623", {"start": v(17.03, -1.82) * mm, "end": v(17.05, -1.63) * mm});
            skLineSegment(sketch, "E1624", {"start": v(17.05, -1.63) * mm, "end": v(17.07, -1.44) * mm});
            skLineSegment(sketch, "E1625", {"start": v(17.07, -1.44) * mm, "end": v(17.09, -1.26) * mm});
            skLineSegment(sketch, "E1626", {"start": v(17.09, -1.26) * mm, "end": v(17.1, -1.07) * mm});
            skLineSegment(sketch, "E1627", {"start": v(17.1, -1.07) * mm, "end": v(17.12, -0.88) * mm});
            skLineSegment(sketch, "E1628", {"start": v(17.12, -0.88) * mm, "end": v(17.14, -0.7) * mm});
            skLineSegment(sketch, "E1629", {"start": v(-17.22, 1.17) * mm, "end": v(-17, 1.26) * mm});
            skLineSegment(sketch, "E1630", {"start": v(-17, 1.26) * mm, "end": v(-16.78, 1.35) * mm});
            skLineSegment(sketch, "E1631", {"start": v(-16.78, 1.35) * mm, "end": v(-16.56, 1.44) * mm});
            skLineSegment(sketch, "E1632", {"start": v(-16.56, 1.44) * mm, "end": v(-16.34, 1.52) * mm});
            skLineSegment(sketch, "E1633", {"start": v(-16.34, 1.52) * mm, "end": v(-16.12, 1.6) * mm});
            skLineSegment(sketch, "E1634", {"start": v(-16.12, 1.6) * mm, "end": v(-15.9, 1.67) * mm});
            skLineSegment(sketch, "E1635", {"start": v(-15.9, 1.67) * mm, "end": v(-15.68, 1.75) * mm});
            skLineSegment(sketch, "E1636", {"start": v(-15.68, 1.75) * mm, "end": v(-15.46, 1.82) * mm});
            skLineSegment(sketch, "E1637", {"start": v(-15.46, 1.82) * mm, "end": v(-15.24, 1.89) * mm});
            skLineSegment(sketch, "E1638", {"start": v(-15.24, 1.89) * mm, "end": v(-15.02, 1.95) * mm});
            skLineSegment(sketch, "E1639", {"start": v(-15.02, 1.95) * mm, "end": v(-14.8, 2.01) * mm});
            skLineSegment(sketch, "E1640", {"start": v(-14.8, 2.01) * mm, "end": v(-14.58, 2.07) * mm});
            skLineSegment(sketch, "E1641", {"start": v(-14.58, 2.07) * mm, "end": v(-14.35, 2.12) * mm});
            skLineSegment(sketch, "E1642", {"start": v(-14.35, 2.12) * mm, "end": v(-14.13, 2.18) * mm});
            skLineSegment(sketch, "E1643", {"start": v(-14.13, 2.18) * mm, "end": v(-13.9, 2.22) * mm});
            skLineSegment(sketch, "E1644", {"start": v(-13.9, 2.22) * mm, "end": v(-13.69, 2.27) * mm});
            skLineSegment(sketch, "E1645", {"start": v(-13.69, 2.27) * mm, "end": v(-13.47, 2.31) * mm});
            skLineSegment(sketch, "E1646", {"start": v(-13.47, 2.31) * mm, "end": v(-13.24, 2.35) * mm});
            skLineSegment(sketch, "E1647", {"start": v(-13.24, 2.35) * mm, "end": v(-13.02, 2.39) * mm});
            skLineSegment(sketch, "E1648", {"start": v(-13.02, 2.39) * mm, "end": v(-12.8, 2.42) * mm});
            skLineSegment(sketch, "E1649", {"start": v(-12.8, 2.42) * mm, "end": v(-12.57, 2.45) * mm});
            skLineSegment(sketch, "E1650", {"start": v(-12.57, 2.45) * mm, "end": v(-12.35, 2.48) * mm});
            skLineSegment(sketch, "E1651", {"start": v(-12.35, 2.48) * mm, "end": v(-12.13, 2.5) * mm});
            skLineSegment(sketch, "E1652", {"start": v(-12.13, 2.5) * mm, "end": v(-11.9, 2.52) * mm});
            skLineSegment(sketch, "E1653", {"start": v(-11.9, 2.52) * mm, "end": v(-11.68, 2.54) * mm});
            skLineSegment(sketch, "E1654", {"start": v(-11.68, 2.54) * mm, "end": v(-11.46, 2.55) * mm});
            skLineSegment(sketch, "E1655", {"start": v(-11.46, 2.55) * mm, "end": v(-11.23, 2.57) * mm});
            skLineSegment(sketch, "E1656", {"start": v(-11.23, 2.57) * mm, "end": v(-11, 2.57) * mm});
            skLineSegment(sketch, "E1657", {"start": v(-11, 2.57) * mm, "end": v(-10.78, 2.58) * mm});
            skLineSegment(sketch, "E1658", {"start": v(-10.78, 2.58) * mm, "end": v(-10.56, 2.58) * mm});
            skLineSegment(sketch, "E1659", {"start": v(-10.56, 2.58) * mm, "end": v(-10.33, 2.58) * mm});
            skLineSegment(sketch, "E1660", {"start": v(-10.33, 2.58) * mm, "end": v(-10.11, 2.57) * mm});
            skLineSegment(sketch, "E1661", {"start": v(-10.11, 2.57) * mm, "end": v(-9.9, 2.57) * mm});
            skLineSegment(sketch, "E1662", {"start": v(-9.9, 2.57) * mm, "end": v(-9.67, 2.56) * mm});
            skLineSegment(sketch, "E1663", {"start": v(-9.67, 2.56) * mm, "end": v(-9.45, 2.54) * mm});
            skLineSegment(sketch, "E1664", {"start": v(-9.45, 2.54) * mm, "end": v(-9.23, 2.52) * mm});
            skLineSegment(sketch, "E1665", {"start": v(-9.23, 2.52) * mm, "end": v(-9, 2.5) * mm});
            skLineSegment(sketch, "E1666", {"start": v(-9, 2.5) * mm, "end": v(-8.79, 2.48) * mm});
            skLineSegment(sketch, "E1667", {"start": v(-8.79, 2.48) * mm, "end": v(-8.57, 2.46) * mm});
            skLineSegment(sketch, "E1668", {"start": v(-8.57, 2.46) * mm, "end": v(-8.35, 2.43) * mm});
            skLineSegment(sketch, "E1669", {"start": v(-8.35, 2.43) * mm, "end": v(-8.13, 2.4) * mm});
            skLineSegment(sketch, "E1670", {"start": v(-8.13, 2.4) * mm, "end": v(-7.9, 2.36) * mm});
            skLineSegment(sketch, "E1671", {"start": v(-7.9, 2.36) * mm, "end": v(-7.69, 2.32) * mm});
            skLineSegment(sketch, "E1672", {"start": v(-7.69, 2.32) * mm, "end": v(-7.47, 2.28) * mm});
            skLineSegment(sketch, "E1673", {"start": v(-7.47, 2.28) * mm, "end": v(-7.25, 2.23) * mm});
            skLineSegment(sketch, "E1674", {"start": v(-7.25, 2.23) * mm, "end": v(-7.03, 2.19) * mm});
            skLineSegment(sketch, "E1675", {"start": v(-7.03, 2.19) * mm, "end": v(-6.81, 2.14) * mm});
            skLineSegment(sketch, "E1676", {"start": v(-6.81, 2.14) * mm, "end": v(-6.6, 2.08) * mm});
            skLineSegment(sketch, "E1677", {"start": v(-6.6, 2.08) * mm, "end": v(-6.38, 2.03) * mm});
            skLineSegment(sketch, "E1678", {"start": v(-6.38, 2.03) * mm, "end": v(-6.16, 1.97) * mm});
            skLineSegment(sketch, "E1679", {"start": v(-6.16, 1.97) * mm, "end": v(-5.94, 1.9) * mm});
            skLineSegment(sketch, "E1680", {"start": v(-5.94, 1.9) * mm, "end": v(-5.72, 1.84) * mm});
            skLineSegment(sketch, "E1681", {"start": v(-5.72, 1.84) * mm, "end": v(-5.5, 1.77) * mm});
            skLineSegment(sketch, "E1682", {"start": v(-5.5, 1.77) * mm, "end": v(-5.29, 1.7) * mm});
            skLineSegment(sketch, "E1683", {"start": v(-5.29, 1.7) * mm, "end": v(-5.07, 1.62) * mm});
            skLineSegment(sketch, "E1684", {"start": v(-5.07, 1.62) * mm, "end": v(-4.85, 1.55) * mm});
            skLineSegment(sketch, "E1685", {"start": v(-4.85, 1.55) * mm, "end": v(-4.64, 1.47) * mm});
            skLineSegment(sketch, "E1686", {"start": v(-4.64, 1.47) * mm, "end": v(-4.42, 1.38) * mm});
            skLineSegment(sketch, "E1687", {"start": v(-4.42, 1.38) * mm, "end": v(-4.2, 1.3) * mm});
            skLineSegment(sketch, "E1688", {"start": v(-4.2, 1.3) * mm, "end": v(-3.99, 1.2) * mm});
            skLineSegment(sketch, "E1689", {"start": v(-3.99, 1.2) * mm, "end": v(-3.82, 1.13) * mm});
            skLineSegment(sketch, "E1690", {"start": v(-3.82, 1.13) * mm, "end": v(-3.75, 1.28) * mm});
            skLineSegment(sketch, "E1691", {"start": v(-3.75, 1.28) * mm, "end": v(-3.67, 1.45) * mm});
            skLineSegment(sketch, "E1692", {"start": v(-3.67, 1.45) * mm, "end": v(-3.57, 1.61) * mm});
            skLineSegment(sketch, "E1693", {"start": v(-3.57, 1.61) * mm, "end": v(-3.46, 1.77) * mm});
            skLineSegment(sketch, "E1694", {"start": v(-3.46, 1.77) * mm, "end": v(-3.35, 1.92) * mm});
            skLineSegment(sketch, "E1695", {"start": v(-3.35, 1.92) * mm, "end": v(-3.22, 2.06) * mm});
            skLineSegment(sketch, "E1696", {"start": v(-3.22, 2.06) * mm, "end": v(-3.09, 2.2) * mm});
            skLineSegment(sketch, "E1697", {"start": v(-3.09, 2.2) * mm, "end": v(-2.95, 2.32) * mm});
            skLineSegment(sketch, "E1698", {"start": v(-2.95, 2.32) * mm, "end": v(-2.8, 2.44) * mm});
            skLineSegment(sketch, "E1699", {"start": v(-2.8, 2.44) * mm, "end": v(-2.64, 2.55) * mm});
            skLineSegment(sketch, "E1700", {"start": v(-2.64, 2.55) * mm, "end": v(-2.48, 2.64) * mm});
            skLineSegment(sketch, "E1701", {"start": v(-2.48, 2.64) * mm, "end": v(-2.3, 2.73) * mm});
            skLineSegment(sketch, "E1702", {"start": v(-2.3, 2.73) * mm, "end": v(-2.13, 2.8) * mm});
            skLineSegment(sketch, "E1703", {"start": v(-2.13, 2.8) * mm, "end": v(-2.06, 2.83) * mm});
            skLineSegment(sketch, "E1704", {"start": v(-2.06, 2.83) * mm, "end": v(-2.12, 2.96) * mm});
            skLineSegment(sketch, "E1705", {"start": v(-2.12, 2.96) * mm, "end": v(-2.23, 3.18) * mm});
            skLineSegment(sketch, "E1706", {"start": v(-2.23, 3.18) * mm, "end": v(-2.33, 3.4) * mm});
            skLineSegment(sketch, "E1707", {"start": v(-2.33, 3.4) * mm, "end": v(-2.42, 3.61) * mm});
            skLineSegment(sketch, "E1708", {"start": v(-2.42, 3.61) * mm, "end": v(-2.52, 3.83) * mm});
            skLineSegment(sketch, "E1709", {"start": v(-2.52, 3.83) * mm, "end": v(-2.6, 4.05) * mm});
            skLineSegment(sketch, "E1710", {"start": v(-2.6, 4.05) * mm, "end": v(-2.7, 4.26) * mm});
            skLineSegment(sketch, "E1711", {"start": v(-2.7, 4.26) * mm, "end": v(-2.78, 4.48) * mm});
            skLineSegment(sketch, "E1712", {"start": v(-2.78, 4.48) * mm, "end": v(-2.86, 4.7) * mm});
            skLineSegment(sketch, "E1713", {"start": v(-2.86, 4.7) * mm, "end": v(-2.93, 4.92) * mm});
            skLineSegment(sketch, "E1714", {"start": v(-2.93, 4.92) * mm, "end": v(-3, 5.13) * mm});
            skLineSegment(sketch, "E1715", {"start": v(-3, 5.13) * mm, "end": v(-3.07, 5.35) * mm});
            skLineSegment(sketch, "E1716", {"start": v(-3.07, 5.35) * mm, "end": v(-3.14, 5.57) * mm});
            skLineSegment(sketch, "E1717", {"start": v(-3.14, 5.57) * mm, "end": v(-3.2, 5.79) * mm});
            skLineSegment(sketch, "E1718", {"start": v(-3.2, 5.79) * mm, "end": v(-3.26, 6) * mm});
            skLineSegment(sketch, "E1719", {"start": v(-3.26, 6) * mm, "end": v(-3.32, 6.23) * mm});
            skLineSegment(sketch, "E1720", {"start": v(-3.32, 6.23) * mm, "end": v(-3.37, 6.44) * mm});
            skLineSegment(sketch, "E1721", {"start": v(-3.37, 6.44) * mm, "end": v(-3.42, 6.66) * mm});
            skLineSegment(sketch, "E1722", {"start": v(-3.42, 6.66) * mm, "end": v(-3.46, 6.88) * mm});
            skLineSegment(sketch, "E1723", {"start": v(-3.46, 6.88) * mm, "end": v(-3.5, 7.1) * mm});
            skLineSegment(sketch, "E1724", {"start": v(-3.5, 7.1) * mm, "end": v(-3.54, 7.32) * mm});
            skLineSegment(sketch, "E1725", {"start": v(-3.54, 7.32) * mm, "end": v(-3.57, 7.54) * mm});
            skLineSegment(sketch, "E1726", {"start": v(-3.57, 7.54) * mm, "end": v(-3.6, 7.76) * mm});
            skLineSegment(sketch, "E1727", {"start": v(-3.6, 7.76) * mm, "end": v(-3.63, 7.98) * mm});
            skLineSegment(sketch, "E1728", {"start": v(-3.63, 7.98) * mm, "end": v(-3.65, 8.2) * mm});
            skLineSegment(sketch, "E1729", {"start": v(-3.65, 8.2) * mm, "end": v(-3.67, 8.42) * mm});
            skLineSegment(sketch, "E1730", {"start": v(-3.67, 8.42) * mm, "end": v(-3.7, 8.65) * mm});
            skLineSegment(sketch, "E1731", {"start": v(-3.7, 8.65) * mm, "end": v(-3.7, 8.87) * mm});
            skLineSegment(sketch, "E1732", {"start": v(-3.7, 8.87) * mm, "end": v(-3.71, 9.09) * mm});
            skLineSegment(sketch, "E1733", {"start": v(-3.71, 9.09) * mm, "end": v(-3.72, 9.3) * mm});
            skLineSegment(sketch, "E1734", {"start": v(-3.72, 9.3) * mm, "end": v(-3.72, 9.53) * mm});
            skLineSegment(sketch, "E1735", {"start": v(-3.72, 9.53) * mm, "end": v(-3.72, 9.76) * mm});
            skLineSegment(sketch, "E1736", {"start": v(-3.72, 9.76) * mm, "end": v(-3.71, 9.98) * mm});
            skLineSegment(sketch, "E1737", {"start": v(-3.71, 9.98) * mm, "end": v(-3.7, 10.2) * mm});
            skLineSegment(sketch, "E1738", {"start": v(-3.7, 10.2) * mm, "end": v(-3.69, 10.43) * mm});
            skLineSegment(sketch, "E1739", {"start": v(-3.69, 10.43) * mm, "end": v(-3.67, 10.65) * mm});
            skLineSegment(sketch, "E1740", {"start": v(-3.67, 10.65) * mm, "end": v(-3.65, 10.88) * mm});
            skLineSegment(sketch, "E1741", {"start": v(-3.65, 10.88) * mm, "end": v(-3.63, 11.1) * mm});
            skLineSegment(sketch, "E1742", {"start": v(-3.63, 11.1) * mm, "end": v(-3.6, 11.33) * mm});
            skLineSegment(sketch, "E1743", {"start": v(-3.6, 11.33) * mm, "end": v(-3.57, 11.55) * mm});
            skLineSegment(sketch, "E1744", {"start": v(-3.57, 11.55) * mm, "end": v(-3.53, 11.77) * mm});
            skLineSegment(sketch, "E1745", {"start": v(-3.53, 11.77) * mm, "end": v(-3.5, 12) * mm});
            skLineSegment(sketch, "E1746", {"start": v(-3.5, 12) * mm, "end": v(-3.45, 12.22) * mm});
            skLineSegment(sketch, "E1747", {"start": v(-3.45, 12.22) * mm, "end": v(-3.4, 12.44) * mm});
            skLineSegment(sketch, "E1748", {"start": v(-3.4, 12.44) * mm, "end": v(-3.36, 12.66) * mm});
            skLineSegment(sketch, "E1749", {"start": v(-3.36, 12.66) * mm, "end": v(-3.3, 12.89) * mm});
            skLineSegment(sketch, "E1750", {"start": v(-3.3, 12.89) * mm, "end": v(-3.25, 13.1) * mm});
            skLineSegment(sketch, "E1751", {"start": v(-3.25, 13.1) * mm, "end": v(-3.19, 13.33) * mm});
            skLineSegment(sketch, "E1752", {"start": v(-3.19, 13.33) * mm, "end": v(-3.12, 13.55) * mm});
            skLineSegment(sketch, "E1753", {"start": v(-3.12, 13.55) * mm, "end": v(-3.06, 13.77) * mm});
            skLineSegment(sketch, "E1754", {"start": v(-3.06, 13.77) * mm, "end": v(-2.99, 14) * mm});
            skLineSegment(sketch, "E1755", {"start": v(-2.99, 14) * mm, "end": v(-2.91, 14.21) * mm});
            skLineSegment(sketch, "E1756", {"start": v(-2.91, 14.21) * mm, "end": v(-2.83, 14.43) * mm});
            skLineSegment(sketch, "E1757", {"start": v(-2.83, 14.43) * mm, "end": v(-2.75, 14.65) * mm});
            skLineSegment(sketch, "E1758", {"start": v(-2.75, 14.65) * mm, "end": v(-2.66, 14.87) * mm});
            skLineSegment(sketch, "E1759", {"start": v(-2.66, 14.87) * mm, "end": v(-2.58, 15.1) * mm});
            skLineSegment(sketch, "E1760", {"start": v(-2.58, 15.1) * mm, "end": v(-2.48, 15.31) * mm});
            skLineSegment(sketch, "E1761", {"start": v(-2.48, 15.31) * mm, "end": v(-2.39, 15.53) * mm});
            skLineSegment(sketch, "E1762", {"start": v(-2.39, 15.53) * mm, "end": v(-2.29, 15.75) * mm});
            skLineSegment(sketch, "E1763", {"start": v(-2.29, 15.75) * mm, "end": v(-2.18, 15.97) * mm});
            skLineSegment(sketch, "E1764", {"start": v(-2.18, 15.97) * mm, "end": v(-2.08, 16.2) * mm});
            skLineSegment(sketch, "E1765", {"start": v(-2.08, 16.2) * mm, "end": v(-2, 16.32) * mm});
            skLineSegment(sketch, "E1766", {"start": v(-2, 16.32) * mm, "end": v(-2.05, 16.32) * mm});
            skLineSegment(sketch, "E1767", {"start": v(-2.05, 16.32) * mm, "end": v(-3.07, 16.23) * mm});
            skLineSegment(sketch, "E1768", {"start": v(-3.07, 16.23) * mm, "end": v(-4.09, 16.07) * mm});
            skLineSegment(sketch, "E1769", {"start": v(-4.09, 16.07) * mm, "end": v(-5.1, 15.84) * mm});
            skLineSegment(sketch, "E1770", {"start": v(-5.1, 15.84) * mm, "end": v(-6.08, 15.56) * mm});
            skLineSegment(sketch, "E1771", {"start": v(-6.08, 15.56) * mm, "end": v(-7.04, 15.2) * mm});
            skLineSegment(sketch, "E1772", {"start": v(-7.04, 15.2) * mm, "end": v(-7.99, 14.8) * mm});
            skLineSegment(sketch, "E1773", {"start": v(-7.99, 14.8) * mm, "end": v(-8.9, 14.33) * mm});
            skLineSegment(sketch, "E1774", {"start": v(-8.9, 14.33) * mm, "end": v(-9.79, 13.8) * mm});
            skLineSegment(sketch, "E1775", {"start": v(-9.79, 13.8) * mm, "end": v(-10.64, 13.23) * mm});
            skLineSegment(sketch, "E1776", {"start": v(-10.64, 13.23) * mm, "end": v(-11.45, 12.6) * mm});
            skLineSegment(sketch, "E1777", {"start": v(-11.45, 12.6) * mm, "end": v(-12.22, 11.92) * mm});
            skLineSegment(sketch, "E1778", {"start": v(-12.22, 11.92) * mm, "end": v(-12.95, 11.2) * mm});
            skLineSegment(sketch, "E1779", {"start": v(-12.95, 11.2) * mm, "end": v(-13.63, 10.42) * mm});
            skLineSegment(sketch, "E1780", {"start": v(-13.63, 10.42) * mm, "end": v(-14.26, 9.61) * mm});
            skLineSegment(sketch, "E1781", {"start": v(-14.26, 9.61) * mm, "end": v(-14.83, 8.76) * mm});
            skLineSegment(sketch, "E1782", {"start": v(-14.83, 8.76) * mm, "end": v(-15.36, 7.88) * mm});
            skLineSegment(sketch, "E1783", {"start": v(-15.36, 7.88) * mm, "end": v(-15.82, 6.96) * mm});
            skLineSegment(sketch, "E1784", {"start": v(-15.82, 6.96) * mm, "end": v(-16.23, 6.02) * mm});
            skLineSegment(sketch, "E1785", {"start": v(-16.23, 6.02) * mm, "end": v(-16.58, 5.05) * mm});
            skLineSegment(sketch, "E1786", {"start": v(-16.58, 5.05) * mm, "end": v(-16.87, 4.07) * mm});
            skLineSegment(sketch, "E1787", {"start": v(-16.87, 4.07) * mm, "end": v(-17.1, 3.06) * mm});
            skLineSegment(sketch, "E1788", {"start": v(-17.1, 3.06) * mm, "end": v(-17.25, 2.05) * mm});
            skLineSegment(sketch, "E1789", {"start": v(-17.25, 2.05) * mm, "end": v(-17.34, 1.12) * mm});
            skLineSegment(sketch, "E1790", {"start": v(-17.34, 1.12) * mm, "end": v(-17.22, 1.17) * mm});
            skLineSegment(sketch, "E1791", {"start": v(15.3, 1.02) * mm, "end": v(15.2, 2.05) * mm});
            skLineSegment(sketch, "E1792", {"start": v(15.2, 2.05) * mm, "end": v(15.05, 3.06) * mm});
            skLineSegment(sketch, "E1793", {"start": v(15.05, 3.06) * mm, "end": v(14.82, 4.07) * mm});
            skLineSegment(sketch, "E1794", {"start": v(14.82, 4.07) * mm, "end": v(14.53, 5.05) * mm});
            skLineSegment(sketch, "E1795", {"start": v(14.53, 5.05) * mm, "end": v(14.19, 6.02) * mm});
            skLineSegment(sketch, "E1796", {"start": v(14.19, 6.02) * mm, "end": v(13.78, 6.96) * mm});
            skLineSegment(sketch, "E1797", {"start": v(13.78, 6.96) * mm, "end": v(13.31, 7.88) * mm});
            skLineSegment(sketch, "E1798", {"start": v(13.31, 7.88) * mm, "end": v(12.79, 8.76) * mm});
            skLineSegment(sketch, "E1799", {"start": v(12.79, 8.76) * mm, "end": v(12.21, 9.61) * mm});
            skLineSegment(sketch, "E1800", {"start": v(12.21, 9.61) * mm, "end": v(11.58, 10.42) * mm});
            skLineSegment(sketch, "E1801", {"start": v(11.58, 10.42) * mm, "end": v(10.9, 11.2) * mm});
            skLineSegment(sketch, "E1802", {"start": v(10.9, 11.2) * mm, "end": v(10.17, 11.92) * mm});
            skLineSegment(sketch, "E1803", {"start": v(10.17, 11.92) * mm, "end": v(9.4, 12.6) * mm});
            skLineSegment(sketch, "E1804", {"start": v(9.4, 12.6) * mm, "end": v(8.6, 13.23) * mm});
            skLineSegment(sketch, "E1805", {"start": v(8.6, 13.23) * mm, "end": v(7.74, 13.8) * mm});
            skLineSegment(sketch, "E1806", {"start": v(7.74, 13.8) * mm, "end": v(6.86, 14.33) * mm});
            skLineSegment(sketch, "E1807", {"start": v(6.86, 14.33) * mm, "end": v(5.94, 14.8) * mm});
            skLineSegment(sketch, "E1808", {"start": v(5.94, 14.8) * mm, "end": v(5, 15.2) * mm});
            skLineSegment(sketch, "E1809", {"start": v(5, 15.2) * mm, "end": v(4.03, 15.56) * mm});
            skLineSegment(sketch, "E1810", {"start": v(4.03, 15.56) * mm, "end": v(3.05, 15.84) * mm});
            skLineSegment(sketch, "E1811", {"start": v(3.05, 15.84) * mm, "end": v(2.04, 16.07) * mm});
            skLineSegment(sketch, "E1812", {"start": v(2.04, 16.07) * mm, "end": v(1.03, 16.23) * mm});
            skLineSegment(sketch, "E1813", {"start": v(1.03, 16.23) * mm, "end": v(0.1, 16.31) * mm});
            skLineSegment(sketch, "E1814", {"start": v(0.1, 16.31) * mm, "end": v(0.15, 16.2) * mm});
            skLineSegment(sketch, "E1815", {"start": v(0.15, 16.2) * mm, "end": v(0.24, 15.97) * mm});
            skLineSegment(sketch, "E1816", {"start": v(0.24, 15.97) * mm, "end": v(0.33, 15.75) * mm});
            skLineSegment(sketch, "E1817", {"start": v(0.33, 15.75) * mm, "end": v(0.41, 15.53) * mm});
            skLineSegment(sketch, "E1818", {"start": v(0.41, 15.53) * mm, "end": v(0.5, 15.31) * mm});
            skLineSegment(sketch, "E1819", {"start": v(0.5, 15.31) * mm, "end": v(0.58, 15.1) * mm});
            skLineSegment(sketch, "E1820", {"start": v(0.58, 15.1) * mm, "end": v(0.65, 14.87) * mm});
            skLineSegment(sketch, "E1821", {"start": v(0.65, 14.87) * mm, "end": v(0.73, 14.65) * mm});
            skLineSegment(sketch, "E1822", {"start": v(0.73, 14.65) * mm, "end": v(0.8, 14.43) * mm});
            skLineSegment(sketch, "E1823", {"start": v(0.8, 14.43) * mm, "end": v(0.86, 14.21) * mm});
            skLineSegment(sketch, "E1824", {"start": v(0.86, 14.21) * mm, "end": v(0.93, 14) * mm});
            skLineSegment(sketch, "E1825", {"start": v(0.93, 14) * mm, "end": v(0.99, 13.77) * mm});
            skLineSegment(sketch, "E1826", {"start": v(0.99, 13.77) * mm, "end": v(1.05, 13.55) * mm});
            skLineSegment(sketch, "E1827", {"start": v(1.05, 13.55) * mm, "end": v(1.1, 13.33) * mm});
            skLineSegment(sketch, "E1828", {"start": v(1.1, 13.33) * mm, "end": v(1.15, 13.1) * mm});
            skLineSegment(sketch, "E1829", {"start": v(1.15, 13.1) * mm, "end": v(1.2, 12.89) * mm});
            skLineSegment(sketch, "E1830", {"start": v(1.2, 12.89) * mm, "end": v(1.25, 12.66) * mm});
            skLineSegment(sketch, "E1831", {"start": v(1.25, 12.66) * mm, "end": v(1.3, 12.44) * mm});
            skLineSegment(sketch, "E1832", {"start": v(1.3, 12.44) * mm, "end": v(1.33, 12.22) * mm});
            skLineSegment(sketch, "E1833", {"start": v(1.33, 12.22) * mm, "end": v(1.37, 12) * mm});
            skLineSegment(sketch, "E1834", {"start": v(1.37, 12) * mm, "end": v(1.4, 11.77) * mm});
            skLineSegment(sketch, "E1835", {"start": v(1.4, 11.77) * mm, "end": v(1.43, 11.55) * mm});
            skLineSegment(sketch, "E1836", {"start": v(1.43, 11.55) * mm, "end": v(1.46, 11.33) * mm});
            skLineSegment(sketch, "E1837", {"start": v(1.46, 11.33) * mm, "end": v(1.48, 11.1) * mm});
            skLineSegment(sketch, "E1838", {"start": v(1.48, 11.1) * mm, "end": v(1.5, 10.88) * mm});
            skLineSegment(sketch, "E1839", {"start": v(1.5, 10.88) * mm, "end": v(1.52, 10.65) * mm});
            skLineSegment(sketch, "E1840", {"start": v(1.52, 10.65) * mm, "end": v(1.53, 10.43) * mm});
            skLineSegment(sketch, "E1841", {"start": v(1.53, 10.43) * mm, "end": v(1.54, 10.2) * mm});
            skLineSegment(sketch, "E1842", {"start": v(1.54, 10.2) * mm, "end": v(1.55, 9.98) * mm});
            skLineSegment(sketch, "E1843", {"start": v(1.55, 9.98) * mm, "end": v(1.56, 9.76) * mm});
            skLineSegment(sketch, "E1844", {"start": v(1.56, 9.76) * mm, "end": v(1.56, 9.53) * mm});
            skLineSegment(sketch, "E1845", {"start": v(1.56, 9.53) * mm, "end": v(1.56, 9.3) * mm});
            skLineSegment(sketch, "E1846", {"start": v(1.56, 9.3) * mm, "end": v(1.55, 9.09) * mm});
            skLineSegment(sketch, "E1847", {"start": v(1.55, 9.09) * mm, "end": v(1.55, 8.87) * mm});
            skLineSegment(sketch, "E1848", {"start": v(1.55, 8.87) * mm, "end": v(1.53, 8.65) * mm});
            skLineSegment(sketch, "E1849", {"start": v(1.53, 8.65) * mm, "end": v(1.52, 8.42) * mm});
            skLineSegment(sketch, "E1850", {"start": v(1.52, 8.42) * mm, "end": v(1.5, 8.2) * mm});
            skLineSegment(sketch, "E1851", {"start": v(1.5, 8.2) * mm, "end": v(1.48, 7.98) * mm});
            skLineSegment(sketch, "E1852", {"start": v(1.48, 7.98) * mm, "end": v(1.46, 7.76) * mm});
            skLineSegment(sketch, "E1853", {"start": v(1.46, 7.76) * mm, "end": v(1.43, 7.54) * mm});
            skLineSegment(sketch, "E1854", {"start": v(1.43, 7.54) * mm, "end": v(1.4, 7.32) * mm});
            skLineSegment(sketch, "E1855", {"start": v(1.4, 7.32) * mm, "end": v(1.37, 7.1) * mm});
            skLineSegment(sketch, "E1856", {"start": v(1.37, 7.1) * mm, "end": v(1.34, 6.88) * mm});
            skLineSegment(sketch, "E1857", {"start": v(1.34, 6.88) * mm, "end": v(1.3, 6.66) * mm});
            skLineSegment(sketch, "E1858", {"start": v(1.3, 6.66) * mm, "end": v(1.26, 6.44) * mm});
            skLineSegment(sketch, "E1859", {"start": v(1.26, 6.44) * mm, "end": v(1.21, 6.23) * mm});
            skLineSegment(sketch, "E1860", {"start": v(1.21, 6.23) * mm, "end": v(1.17, 6) * mm});
            skLineSegment(sketch, "E1861", {"start": v(1.17, 6) * mm, "end": v(1.12, 5.79) * mm});
            skLineSegment(sketch, "E1862", {"start": v(1.12, 5.79) * mm, "end": v(1.06, 5.57) * mm});
            skLineSegment(sketch, "E1863", {"start": v(1.06, 5.57) * mm, "end": v(1, 5.35) * mm});
            skLineSegment(sketch, "E1864", {"start": v(1, 5.35) * mm, "end": v(0.95, 5.13) * mm});
            skLineSegment(sketch, "E1865", {"start": v(0.95, 5.13) * mm, "end": v(0.88, 4.92) * mm});
            skLineSegment(sketch, "E1866", {"start": v(0.88, 4.92) * mm, "end": v(0.82, 4.7) * mm});
            skLineSegment(sketch, "E1867", {"start": v(0.82, 4.7) * mm, "end": v(0.75, 4.48) * mm});
            skLineSegment(sketch, "E1868", {"start": v(0.75, 4.48) * mm, "end": v(0.68, 4.26) * mm});
            skLineSegment(sketch, "E1869", {"start": v(0.68, 4.26) * mm, "end": v(0.6, 4.05) * mm});
            skLineSegment(sketch, "E1870", {"start": v(0.6, 4.05) * mm, "end": v(0.53, 3.83) * mm});
            skLineSegment(sketch, "E1871", {"start": v(0.53, 3.83) * mm, "end": v(0.45, 3.61) * mm});
            skLineSegment(sketch, "E1872", {"start": v(0.45, 3.61) * mm, "end": v(0.36, 3.4) * mm});
            skLineSegment(sketch, "E1873", {"start": v(0.36, 3.4) * mm, "end": v(0.28, 3.18) * mm});
            skLineSegment(sketch, "E1874", {"start": v(0.28, 3.18) * mm, "end": v(0.19, 2.96) * mm});
            skLineSegment(sketch, "E1875", {"start": v(0.19, 2.96) * mm, "end": v(0.11, 2.8) * mm});
            skLineSegment(sketch, "E1876", {"start": v(0.11, 2.8) * mm, "end": v(0.26, 2.73) * mm});
            skLineSegment(sketch, "E1877", {"start": v(0.26, 2.73) * mm, "end": v(0.43, 2.64) * mm});
            skLineSegment(sketch, "E1878", {"start": v(0.43, 2.64) * mm, "end": v(0.6, 2.55) * mm});
            skLineSegment(sketch, "E1879", {"start": v(0.6, 2.55) * mm, "end": v(0.75, 2.44) * mm});
            skLineSegment(sketch, "E1880", {"start": v(0.75, 2.44) * mm, "end": v(0.9, 2.32) * mm});
            skLineSegment(sketch, "E1881", {"start": v(0.9, 2.32) * mm, "end": v(1.04, 2.2) * mm});
            skLineSegment(sketch, "E1882", {"start": v(1.04, 2.2) * mm, "end": v(1.18, 2.06) * mm});
            skLineSegment(sketch, "E1883", {"start": v(1.18, 2.06) * mm, "end": v(1.3, 1.92) * mm});
            skLineSegment(sketch, "E1884", {"start": v(1.3, 1.92) * mm, "end": v(1.42, 1.77) * mm});
            skLineSegment(sketch, "E1885", {"start": v(1.42, 1.77) * mm, "end": v(1.53, 1.61) * mm});
            skLineSegment(sketch, "E1886", {"start": v(1.53, 1.61) * mm, "end": v(1.62, 1.45) * mm});
            skLineSegment(sketch, "E1887", {"start": v(1.62, 1.45) * mm, "end": v(1.7, 1.28) * mm});
            skLineSegment(sketch, "E1888", {"start": v(1.7, 1.28) * mm, "end": v(1.78, 1.1) * mm});
            skLineSegment(sketch, "E1889", {"start": v(1.78, 1.1) * mm, "end": v(1.81, 1.03) * mm});
            skLineSegment(sketch, "E1890", {"start": v(1.81, 1.03) * mm, "end": v(1.94, 1.1) * mm});
            skLineSegment(sketch, "E1891", {"start": v(1.94, 1.1) * mm, "end": v(2.16, 1.2) * mm});
            skLineSegment(sketch, "E1892", {"start": v(2.16, 1.2) * mm, "end": v(2.38, 1.3) * mm});
            skLineSegment(sketch, "E1893", {"start": v(2.38, 1.3) * mm, "end": v(2.6, 1.4) * mm});
            skLineSegment(sketch, "E1894", {"start": v(2.6, 1.4) * mm, "end": v(2.8, 1.5) * mm});
            skLineSegment(sketch, "E1895", {"start": v(2.8, 1.5) * mm, "end": v(3.03, 1.58) * mm});
            skLineSegment(sketch, "E1896", {"start": v(3.03, 1.58) * mm, "end": v(3.24, 1.67) * mm});
            skLineSegment(sketch, "E1897", {"start": v(3.24, 1.67) * mm, "end": v(3.46, 1.75) * mm});
            skLineSegment(sketch, "E1898", {"start": v(3.46, 1.75) * mm, "end": v(3.68, 1.83) * mm});
            skLineSegment(sketch, "E1899", {"start": v(3.68, 1.83) * mm, "end": v(3.9, 1.9) * mm});
            skLineSegment(sketch, "E1900", {"start": v(3.9, 1.9) * mm, "end": v(4.11, 1.98) * mm});
            skLineSegment(sketch, "E1901", {"start": v(4.11, 1.98) * mm, "end": v(4.33, 2.05) * mm});
            skLineSegment(sketch, "E1902", {"start": v(4.33, 2.05) * mm, "end": v(4.55, 2.12) * mm});
            skLineSegment(sketch, "E1903", {"start": v(4.55, 2.12) * mm, "end": v(4.77, 2.18) * mm});
            skLineSegment(sketch, "E1904", {"start": v(4.77, 2.18) * mm, "end": v(4.99, 2.24) * mm});
            skLineSegment(sketch, "E1905", {"start": v(4.99, 2.24) * mm, "end": v(5.2, 2.3) * mm});
            skLineSegment(sketch, "E1906", {"start": v(5.2, 2.3) * mm, "end": v(5.42, 2.34) * mm});
            skLineSegment(sketch, "E1907", {"start": v(5.42, 2.34) * mm, "end": v(5.64, 2.4) * mm});
            skLineSegment(sketch, "E1908", {"start": v(5.64, 2.4) * mm, "end": v(5.86, 2.44) * mm});
            skLineSegment(sketch, "E1909", {"start": v(5.86, 2.44) * mm, "end": v(6.08, 2.48) * mm});
            skLineSegment(sketch, "E1910", {"start": v(6.08, 2.48) * mm, "end": v(6.3, 2.52) * mm});
            skLineSegment(sketch, "E1911", {"start": v(6.3, 2.52) * mm, "end": v(6.52, 2.55) * mm});
            skLineSegment(sketch, "E1912", {"start": v(6.52, 2.55) * mm, "end": v(6.74, 2.58) * mm});
            skLineSegment(sketch, "E1913", {"start": v(6.74, 2.58) * mm, "end": v(6.96, 2.6) * mm});
            skLineSegment(sketch, "E1914", {"start": v(6.96, 2.6) * mm, "end": v(7.18, 2.63) * mm});
            skLineSegment(sketch, "E1915", {"start": v(7.18, 2.63) * mm, "end": v(7.4, 2.65) * mm});
            skLineSegment(sketch, "E1916", {"start": v(7.4, 2.65) * mm, "end": v(7.62, 2.67) * mm});
            skLineSegment(sketch, "E1917", {"start": v(7.62, 2.67) * mm, "end": v(7.85, 2.68) * mm});
            skLineSegment(sketch, "E1918", {"start": v(7.85, 2.68) * mm, "end": v(8.07, 2.69) * mm});
            skLineSegment(sketch, "E1919", {"start": v(8.07, 2.69) * mm, "end": v(8.29, 2.7) * mm});
            skLineSegment(sketch, "E1920", {"start": v(8.29, 2.7) * mm, "end": v(8.51, 2.7) * mm});
            skLineSegment(sketch, "E1921", {"start": v(8.51, 2.7) * mm, "end": v(8.74, 2.7) * mm});
            skLineSegment(sketch, "E1922", {"start": v(8.74, 2.7) * mm, "end": v(8.96, 2.69) * mm});
            skLineSegment(sketch, "E1923", {"start": v(8.96, 2.69) * mm, "end": v(9.19, 2.68) * mm});
            skLineSegment(sketch, "E1924", {"start": v(9.19, 2.68) * mm, "end": v(9.4, 2.66) * mm});
            skLineSegment(sketch, "E1925", {"start": v(9.4, 2.66) * mm, "end": v(9.63, 2.65) * mm});
            skLineSegment(sketch, "E1926", {"start": v(9.63, 2.65) * mm, "end": v(9.86, 2.63) * mm});
            skLineSegment(sketch, "E1927", {"start": v(9.86, 2.63) * mm, "end": v(10.08, 2.6) * mm});
            skLineSegment(sketch, "E1928", {"start": v(10.08, 2.6) * mm, "end": v(10.3, 2.58) * mm});
            skLineSegment(sketch, "E1929", {"start": v(10.3, 2.58) * mm, "end": v(10.53, 2.54) * mm});
            skLineSegment(sketch, "E1930", {"start": v(10.53, 2.54) * mm, "end": v(10.75, 2.5) * mm});
            skLineSegment(sketch, "E1931", {"start": v(10.75, 2.5) * mm, "end": v(10.97, 2.47) * mm});
            skLineSegment(sketch, "E1932", {"start": v(10.97, 2.47) * mm, "end": v(11.2, 2.43) * mm});
            skLineSegment(sketch, "E1933", {"start": v(11.2, 2.43) * mm, "end": v(11.42, 2.38) * mm});
            skLineSegment(sketch, "E1934", {"start": v(11.42, 2.38) * mm, "end": v(11.64, 2.33) * mm});
            skLineSegment(sketch, "E1935", {"start": v(11.64, 2.33) * mm, "end": v(11.86, 2.28) * mm});
            skLineSegment(sketch, "E1936", {"start": v(11.86, 2.28) * mm, "end": v(12.09, 2.22) * mm});
            skLineSegment(sketch, "E1937", {"start": v(12.09, 2.22) * mm, "end": v(12.3, 2.16) * mm});
            skLineSegment(sketch, "E1938", {"start": v(12.3, 2.16) * mm, "end": v(12.53, 2.1) * mm});
            skLineSegment(sketch, "E1939", {"start": v(12.53, 2.1) * mm, "end": v(12.75, 2.03) * mm});
            skLineSegment(sketch, "E1940", {"start": v(12.75, 2.03) * mm, "end": v(12.97, 1.96) * mm});
            skLineSegment(sketch, "E1941", {"start": v(12.97, 1.96) * mm, "end": v(13.2, 1.89) * mm});
            skLineSegment(sketch, "E1942", {"start": v(13.2, 1.89) * mm, "end": v(13.41, 1.8) * mm});
            skLineSegment(sketch, "E1943", {"start": v(13.41, 1.8) * mm, "end": v(13.63, 1.73) * mm});
            skLineSegment(sketch, "E1944", {"start": v(13.63, 1.73) * mm, "end": v(13.85, 1.64) * mm});
            skLineSegment(sketch, "E1945", {"start": v(13.85, 1.64) * mm, "end": v(14.07, 1.55) * mm});
            skLineSegment(sketch, "E1946", {"start": v(14.07, 1.55) * mm, "end": v(14.3, 1.46) * mm});
            skLineSegment(sketch, "E1947", {"start": v(14.3, 1.46) * mm, "end": v(14.51, 1.36) * mm});
            skLineSegment(sketch, "E1948", {"start": v(14.51, 1.36) * mm, "end": v(14.73, 1.26) * mm});
            skLineSegment(sketch, "E1949", {"start": v(14.73, 1.26) * mm, "end": v(14.95, 1.16) * mm});
            skLineSegment(sketch, "E1950", {"start": v(14.95, 1.16) * mm, "end": v(15.17, 1.05) * mm});
            skLineSegment(sketch, "E1951", {"start": v(15.17, 1.05) * mm, "end": v(15.3, 0.98) * mm});
            skLineSegment(sketch, "E1952", {"start": v(15.3, 0.98) * mm, "end": v(15.3, 1.02) * mm});
            skLineSegment(sketch, "E1953", {"start": v(-0.66, 6.08) * mm, "end": v(-0.61, 6.2) * mm});
            skLineSegment(sketch, "E1954", {"start": v(-0.61, 6.2) * mm, "end": v(-0.56, 6.3) * mm});
            skLineSegment(sketch, "E1955", {"start": v(-0.56, 6.3) * mm, "end": v(-0.52, 6.43) * mm});
            skLineSegment(sketch, "E1956", {"start": v(-0.52, 6.43) * mm, "end": v(-0.47, 6.54) * mm});
            skLineSegment(sketch, "E1957", {"start": v(-0.47, 6.54) * mm, "end": v(-0.43, 6.66) * mm});
            skLineSegment(sketch, "E1958", {"start": v(-0.43, 6.66) * mm, "end": v(-0.38, 6.77) * mm});
            skLineSegment(sketch, "E1959", {"start": v(-0.38, 6.77) * mm, "end": v(-0.34, 6.89) * mm});
            skLineSegment(sketch, "E1960", {"start": v(-0.34, 6.89) * mm, "end": v(-0.3, 7) * mm});
            skLineSegment(sketch, "E1961", {"start": v(-0.3, 7) * mm, "end": v(-0.26, 7.12) * mm});
            skLineSegment(sketch, "E1962", {"start": v(-0.26, 7.12) * mm, "end": v(-0.23, 7.24) * mm});
            skLineSegment(sketch, "E1963", {"start": v(-0.23, 7.24) * mm, "end": v(-0.2, 7.35) * mm});
            skLineSegment(sketch, "E1964", {"start": v(-0.2, 7.35) * mm, "end": v(-0.16, 7.47) * mm});
            skLineSegment(sketch, "E1965", {"start": v(-0.16, 7.47) * mm, "end": v(-0.13, 7.58) * mm});
            skLineSegment(sketch, "E1966", {"start": v(-0.13, 7.58) * mm, "end": v(-0.1, 7.7) * mm});
            skLineSegment(sketch, "E1967", {"start": v(-0.1, 7.7) * mm, "end": v(-0.08, 7.82) * mm});
            skLineSegment(sketch, "E1968", {"start": v(-0.08, 7.82) * mm, "end": v(-0.05, 7.93) * mm});
            skLineSegment(sketch, "E1969", {"start": v(-0.05, 7.93) * mm, "end": v(-0.03, 8.05) * mm});
            skLineSegment(sketch, "E1970", {"start": v(-0.03, 8.05) * mm, "end": v(0, 8.17) * mm});
            skLineSegment(sketch, "E1971", {"start": v(0, 8.17) * mm, "end": v(0.02, 8.28) * mm});
            skLineSegment(sketch, "E1972", {"start": v(0.02, 8.28) * mm, "end": v(0.03, 8.4) * mm});
            skLineSegment(sketch, "E1973", {"start": v(0.03, 8.4) * mm, "end": v(0.05, 8.52) * mm});
            skLineSegment(sketch, "E1974", {"start": v(0.05, 8.52) * mm, "end": v(0.07, 8.63) * mm});
            skLineSegment(sketch, "E1975", {"start": v(0.07, 8.63) * mm, "end": v(0.08, 8.75) * mm});
            skLineSegment(sketch, "E1976", {"start": v(0.08, 8.75) * mm, "end": v(0.1, 8.87) * mm});
            skLineSegment(sketch, "E1977", {"start": v(0.1, 8.87) * mm, "end": v(0.1, 8.98) * mm});
            skLineSegment(sketch, "E1978", {"start": v(0.1, 8.98) * mm, "end": v(0.1, 9.1) * mm});
            skLineSegment(sketch, "E1979", {"start": v(0.1, 9.1) * mm, "end": v(0.11, 9.22) * mm});
            skLineSegment(sketch, "E1980", {"start": v(0.11, 9.22) * mm, "end": v(0.12, 9.34) * mm});
            skLineSegment(sketch, "E1981", {"start": v(0.12, 9.34) * mm, "end": v(0.12, 9.45) * mm});
            skLineSegment(sketch, "E1982", {"start": v(0.12, 9.45) * mm, "end": v(0.12, 9.57) * mm});
            skLineSegment(sketch, "E1983", {"start": v(0.12, 9.57) * mm, "end": v(0.12, 9.7) * mm});
            skLineSegment(sketch, "E1984", {"start": v(0.12, 9.7) * mm, "end": v(0.12, 9.81) * mm});
            skLineSegment(sketch, "E1985", {"start": v(0.12, 9.81) * mm, "end": v(0.11, 9.93) * mm});
            skLineSegment(sketch, "E1986", {"start": v(0.11, 9.93) * mm, "end": v(0.1, 10.05) * mm});
            skLineSegment(sketch, "E1987", {"start": v(0.1, 10.05) * mm, "end": v(0.1, 10.17) * mm});
            skLineSegment(sketch, "E1988", {"start": v(0.1, 10.17) * mm, "end": v(0.09, 10.29) * mm});
            skLineSegment(sketch, "E1989", {"start": v(0.09, 10.29) * mm, "end": v(0.08, 10.4) * mm});
            skLineSegment(sketch, "E1990", {"start": v(0.08, 10.4) * mm, "end": v(0.06, 10.52) * mm});
            skLineSegment(sketch, "E1991", {"start": v(0.06, 10.52) * mm, "end": v(0.05, 10.64) * mm});
            skLineSegment(sketch, "E1992", {"start": v(0.05, 10.64) * mm, "end": v(0.03, 10.76) * mm});
            skLineSegment(sketch, "E1993", {"start": v(0.03, 10.76) * mm, "end": v(0.01, 10.88) * mm});
            skLineSegment(sketch, "E1994", {"start": v(0.01, 10.88) * mm, "end": v(0, 11) * mm});
            skLineSegment(sketch, "E1995", {"start": v(0, 11) * mm, "end": v(-0.03, 11.12) * mm});
            skLineSegment(sketch, "E1996", {"start": v(-0.03, 11.12) * mm, "end": v(-0.06, 11.23) * mm});
            skLineSegment(sketch, "E1997", {"start": v(-0.06, 11.23) * mm, "end": v(-0.08, 11.35) * mm});
            skLineSegment(sketch, "E1998", {"start": v(-0.08, 11.35) * mm, "end": v(-0.1, 11.47) * mm});
            skLineSegment(sketch, "E1999", {"start": v(-0.1, 11.47) * mm, "end": v(-0.14, 11.59) * mm});
            skLineSegment(sketch, "E2000", {"start": v(-0.14, 11.59) * mm, "end": v(-0.17, 11.7) * mm});
            skLineSegment(sketch, "E2001", {"start": v(-0.17, 11.7) * mm, "end": v(-0.2, 11.82) * mm});
            skLineSegment(sketch, "E2002", {"start": v(-0.2, 11.82) * mm, "end": v(-0.24, 11.94) * mm});
            skLineSegment(sketch, "E2003", {"start": v(-0.24, 11.94) * mm, "end": v(-0.28, 12.06) * mm});
            skLineSegment(sketch, "E2004", {"start": v(-0.28, 12.06) * mm, "end": v(-0.31, 12.18) * mm});
            skLineSegment(sketch, "E2005", {"start": v(-0.31, 12.18) * mm, "end": v(-0.35, 12.3) * mm});
            skLineSegment(sketch, "E2006", {"start": v(-0.35, 12.3) * mm, "end": v(-0.4, 12.41) * mm});
            skLineSegment(sketch, "E2007", {"start": v(-0.4, 12.41) * mm, "end": v(-0.44, 12.53) * mm});
            skLineSegment(sketch, "E2008", {"start": v(-0.44, 12.53) * mm, "end": v(-0.49, 12.65) * mm});
            skLineSegment(sketch, "E2009", {"start": v(-0.49, 12.65) * mm, "end": v(-0.53, 12.76) * mm});
            skLineSegment(sketch, "E2010", {"start": v(-0.53, 12.76) * mm, "end": v(-0.58, 12.88) * mm});
            skLineSegment(sketch, "E2011", {"start": v(-0.58, 12.88) * mm, "end": v(-0.63, 13) * mm});
            skLineSegment(sketch, "E2012", {"start": v(-0.63, 13) * mm, "end": v(-0.69, 13.11) * mm});
            skLineSegment(sketch, "E2013", {"start": v(-0.69, 13.11) * mm, "end": v(-0.7, 13.13) * mm});
            skLineSegment(sketch, "E2014", {"start": v(-0.7, 13.13) * mm, "end": v(-1.26, 13.13) * mm});
            skLineSegment(sketch, "E2015", {"start": v(-1.26, 13.13) * mm, "end": v(-1.28, 13.1) * mm});
            skLineSegment(sketch, "E2016", {"start": v(-1.28, 13.1) * mm, "end": v(-1.34, 12.98) * mm});
            skLineSegment(sketch, "E2017", {"start": v(-1.34, 12.98) * mm, "end": v(-1.4, 12.86) * mm});
            skLineSegment(sketch, "E2018", {"start": v(-1.4, 12.86) * mm, "end": v(-1.46, 12.74) * mm});
            skLineSegment(sketch, "E2019", {"start": v(-1.46, 12.74) * mm, "end": v(-1.51, 12.63) * mm});
            skLineSegment(sketch, "E2020", {"start": v(-1.51, 12.63) * mm, "end": v(-1.57, 12.5) * mm});
            skLineSegment(sketch, "E2021", {"start": v(-1.57, 12.5) * mm, "end": v(-1.62, 12.4) * mm});
            skLineSegment(sketch, "E2022", {"start": v(-1.62, 12.4) * mm, "end": v(-1.67, 12.28) * mm});
            skLineSegment(sketch, "E2023", {"start": v(-1.67, 12.28) * mm, "end": v(-1.71, 12.16) * mm});
            skLineSegment(sketch, "E2024", {"start": v(-1.71, 12.16) * mm, "end": v(-1.76, 12.04) * mm});
            skLineSegment(sketch, "E2025", {"start": v(-1.76, 12.04) * mm, "end": v(-1.8, 11.93) * mm});
            skLineSegment(sketch, "E2026", {"start": v(-1.8, 11.93) * mm, "end": v(-1.84, 11.8) * mm});
            skLineSegment(sketch, "E2027", {"start": v(-1.84, 11.8) * mm, "end": v(-1.88, 11.7) * mm});
            skLineSegment(sketch, "E2028", {"start": v(-1.88, 11.7) * mm, "end": v(-1.92, 11.57) * mm});
            skLineSegment(sketch, "E2029", {"start": v(-1.92, 11.57) * mm, "end": v(-1.95, 11.46) * mm});
            skLineSegment(sketch, "E2030", {"start": v(-1.95, 11.46) * mm, "end": v(-1.98, 11.34) * mm});
            skLineSegment(sketch, "E2031", {"start": v(-1.98, 11.34) * mm, "end": v(-2.01, 11.22) * mm});
            skLineSegment(sketch, "E2032", {"start": v(-2.01, 11.22) * mm, "end": v(-2.04, 11.1) * mm});
            skLineSegment(sketch, "E2033", {"start": v(-2.04, 11.1) * mm, "end": v(-2.07, 10.99) * mm});
            skLineSegment(sketch, "E2034", {"start": v(-2.07, 10.99) * mm, "end": v(-2.1, 10.87) * mm});
            skLineSegment(sketch, "E2035", {"start": v(-2.1, 10.87) * mm, "end": v(-2.11, 10.75) * mm});
            skLineSegment(sketch, "E2036", {"start": v(-2.11, 10.75) * mm, "end": v(-2.13, 10.63) * mm});
            skLineSegment(sketch, "E2037", {"start": v(-2.13, 10.63) * mm, "end": v(-2.15, 10.52) * mm});
            skLineSegment(sketch, "E2038", {"start": v(-2.15, 10.52) * mm, "end": v(-2.17, 10.4) * mm});
            skLineSegment(sketch, "E2039", {"start": v(-2.17, 10.4) * mm, "end": v(-2.18, 10.28) * mm});
            skLineSegment(sketch, "E2040", {"start": v(-2.18, 10.28) * mm, "end": v(-2.2, 10.16) * mm});
            skLineSegment(sketch, "E2041", {"start": v(-2.2, 10.16) * mm, "end": v(-2.2, 10.04) * mm});
            skLineSegment(sketch, "E2042", {"start": v(-2.2, 10.04) * mm, "end": v(-2.2, 9.93) * mm});
            skLineSegment(sketch, "E2043", {"start": v(-2.2, 9.93) * mm, "end": v(-2.21, 9.8) * mm});
            skLineSegment(sketch, "E2044", {"start": v(-2.21, 9.8) * mm, "end": v(-2.22, 9.69) * mm});
            skLineSegment(sketch, "E2045", {"start": v(-2.22, 9.69) * mm, "end": v(-2.22, 9.57) * mm});
            skLineSegment(sketch, "E2046", {"start": v(-2.22, 9.57) * mm, "end": v(-2.22, 9.45) * mm});
            skLineSegment(sketch, "E2047", {"start": v(-2.22, 9.45) * mm, "end": v(-2.21, 9.34) * mm});
            skLineSegment(sketch, "E2048", {"start": v(-2.21, 9.34) * mm, "end": v(-2.2, 9.22) * mm});
            skLineSegment(sketch, "E2049", {"start": v(-2.2, 9.22) * mm, "end": v(-2.2, 9.1) * mm});
            skLineSegment(sketch, "E2050", {"start": v(-2.2, 9.1) * mm, "end": v(-2.2, 8.99) * mm});
            skLineSegment(sketch, "E2051", {"start": v(-2.2, 8.99) * mm, "end": v(-2.18, 8.87) * mm});
            skLineSegment(sketch, "E2052", {"start": v(-2.18, 8.87) * mm, "end": v(-2.17, 8.76) * mm});
            skLineSegment(sketch, "E2053", {"start": v(-2.17, 8.76) * mm, "end": v(-2.15, 8.64) * mm});
            skLineSegment(sketch, "E2054", {"start": v(-2.15, 8.64) * mm, "end": v(-2.13, 8.52) * mm});
            skLineSegment(sketch, "E2055", {"start": v(-2.13, 8.52) * mm, "end": v(-2.12, 8.4) * mm});
            skLineSegment(sketch, "E2056", {"start": v(-2.12, 8.4) * mm, "end": v(-2.1, 8.3) * mm});
            skLineSegment(sketch, "E2057", {"start": v(-2.1, 8.3) * mm, "end": v(-2.07, 8.18) * mm});
            skLineSegment(sketch, "E2058", {"start": v(-2.07, 8.18) * mm, "end": v(-2.05, 8.06) * mm});
            skLineSegment(sketch, "E2059", {"start": v(-2.05, 8.06) * mm, "end": v(-2.02, 7.94) * mm});
            skLineSegment(sketch, "E2060", {"start": v(-2.02, 7.94) * mm, "end": v(-1.99, 7.83) * mm});
            skLineSegment(sketch, "E2061", {"start": v(-1.99, 7.83) * mm, "end": v(-1.96, 7.71) * mm});
            skLineSegment(sketch, "E2062", {"start": v(-1.96, 7.71) * mm, "end": v(-1.92, 7.6) * mm});
            skLineSegment(sketch, "E2063", {"start": v(-1.92, 7.6) * mm, "end": v(-1.89, 7.48) * mm});
            skLineSegment(sketch, "E2064", {"start": v(-1.89, 7.48) * mm, "end": v(-1.85, 7.37) * mm});
            skLineSegment(sketch, "E2065", {"start": v(-1.85, 7.37) * mm, "end": v(-1.81, 7.25) * mm});
            skLineSegment(sketch, "E2066", {"start": v(-1.81, 7.25) * mm, "end": v(-1.77, 7.14) * mm});
            skLineSegment(sketch, "E2067", {"start": v(-1.77, 7.14) * mm, "end": v(-1.73, 7.02) * mm});
            skLineSegment(sketch, "E2068", {"start": v(-1.73, 7.02) * mm, "end": v(-1.68, 6.9) * mm});
            skLineSegment(sketch, "E2069", {"start": v(-1.68, 6.9) * mm, "end": v(-1.63, 6.79) * mm});
            skLineSegment(sketch, "E2070", {"start": v(-1.63, 6.79) * mm, "end": v(-1.58, 6.67) * mm});
            skLineSegment(sketch, "E2071", {"start": v(-1.58, 6.67) * mm, "end": v(-1.53, 6.56) * mm});
            skLineSegment(sketch, "E2072", {"start": v(-1.53, 6.56) * mm, "end": v(-1.48, 6.44) * mm});
            skLineSegment(sketch, "E2073", {"start": v(-1.48, 6.44) * mm, "end": v(-1.42, 6.33) * mm});
            skLineSegment(sketch, "E2074", {"start": v(-1.42, 6.33) * mm, "end": v(-1.37, 6.21) * mm});
            skLineSegment(sketch, "E2075", {"start": v(-1.37, 6.21) * mm, "end": v(-1.3, 6.1) * mm});
            skLineSegment(sketch, "E2076", {"start": v(-1.3, 6.1) * mm, "end": v(-1.3, 6.07) * mm});
            skLineSegment(sketch, "E2077", {"start": v(-1.3, 6.07) * mm, "end": v(-0.67, 6.07) * mm});
            skLineSegment(sketch, "E2078", {"start": v(-0.67, 6.07) * mm, "end": v(-0.66, 6.08) * mm});
            skLineSegment(sketch, "E2079", {"start": v(8.67, -1.15) * mm, "end": v(8.79, -1.14) * mm});
            skLineSegment(sketch, "E2080", {"start": v(8.79, -1.14) * mm, "end": v(8.9, -1.14) * mm});
            skLineSegment(sketch, "E2081", {"start": v(8.9, -1.14) * mm, "end": v(9.03, -1.13) * mm});
            skLineSegment(sketch, "E2082", {"start": v(9.03, -1.13) * mm, "end": v(9.15, -1.12) * mm});
            skLineSegment(sketch, "E2083", {"start": v(9.15, -1.12) * mm, "end": v(9.27, -1.11) * mm});
            skLineSegment(sketch, "E2084", {"start": v(9.27, -1.11) * mm, "end": v(9.38, -1.1) * mm});
            skLineSegment(sketch, "E2085", {"start": v(9.38, -1.1) * mm, "end": v(9.5, -1.09) * mm});
            skLineSegment(sketch, "E2086", {"start": v(9.5, -1.09) * mm, "end": v(9.62, -1.07) * mm});
            skLineSegment(sketch, "E2087", {"start": v(9.62, -1.07) * mm, "end": v(9.74, -1.06) * mm});
            skLineSegment(sketch, "E2088", {"start": v(9.74, -1.06) * mm, "end": v(9.86, -1.04) * mm});
            skLineSegment(sketch, "E2089", {"start": v(9.86, -1.04) * mm, "end": v(9.98, -1.02) * mm});
            skLineSegment(sketch, "E2090", {"start": v(9.98, -1.02) * mm, "end": v(10.1, -1) * mm});
            skLineSegment(sketch, "E2091", {"start": v(10.1, -1) * mm, "end": v(10.21, -0.97) * mm});
            skLineSegment(sketch, "E2092", {"start": v(10.21, -0.97) * mm, "end": v(10.33, -0.94) * mm});
            skLineSegment(sketch, "E2093", {"start": v(10.33, -0.94) * mm, "end": v(10.45, -0.92) * mm});
            skLineSegment(sketch, "E2094", {"start": v(10.45, -0.92) * mm, "end": v(10.57, -0.89) * mm});
            skLineSegment(sketch, "E2095", {"start": v(10.57, -0.89) * mm, "end": v(10.68, -0.85) * mm});
            skLineSegment(sketch, "E2096", {"start": v(10.68, -0.85) * mm, "end": v(10.8, -0.82) * mm});
            skLineSegment(sketch, "E2097", {"start": v(10.8, -0.82) * mm, "end": v(10.92, -0.79) * mm});
            skLineSegment(sketch, "E2098", {"start": v(10.92, -0.79) * mm, "end": v(11.04, -0.75) * mm});
            skLineSegment(sketch, "E2099", {"start": v(11.04, -0.75) * mm, "end": v(11.15, -0.71) * mm});
            skLineSegment(sketch, "E2100", {"start": v(11.15, -0.71) * mm, "end": v(11.27, -0.67) * mm});
            skLineSegment(sketch, "E2101", {"start": v(11.27, -0.67) * mm, "end": v(11.39, -0.63) * mm});
            skLineSegment(sketch, "E2102", {"start": v(11.39, -0.63) * mm, "end": v(11.5, -0.58) * mm});
            skLineSegment(sketch, "E2103", {"start": v(11.5, -0.58) * mm, "end": v(11.62, -0.54) * mm});
            skLineSegment(sketch, "E2104", {"start": v(11.62, -0.54) * mm, "end": v(11.74, -0.5) * mm});
            skLineSegment(sketch, "E2105", {"start": v(11.74, -0.5) * mm, "end": v(11.86, -0.44) * mm});
            skLineSegment(sketch, "E2106", {"start": v(11.86, -0.44) * mm, "end": v(11.98, -0.4) * mm});
            skLineSegment(sketch, "E2107", {"start": v(11.98, -0.4) * mm, "end": v(12.1, -0.34) * mm});
            skLineSegment(sketch, "E2108", {"start": v(12.1, -0.34) * mm, "end": v(12.1, -0.33) * mm});
            skLineSegment(sketch, "E2109", {"start": v(12.1, -0.33) * mm, "end": v(12.1, 0.24) * mm});
            skLineSegment(sketch, "E2110", {"start": v(12.1, 0.24) * mm, "end": v(12.07, 0.26) * mm});
            skLineSegment(sketch, "E2111", {"start": v(12.07, 0.26) * mm, "end": v(11.96, 0.32) * mm});
            skLineSegment(sketch, "E2112", {"start": v(11.96, 0.32) * mm, "end": v(11.84, 0.38) * mm});
            skLineSegment(sketch, "E2113", {"start": v(11.84, 0.38) * mm, "end": v(11.72, 0.43) * mm});
            skLineSegment(sketch, "E2114", {"start": v(11.72, 0.43) * mm, "end": v(11.6, 0.49) * mm});
            skLineSegment(sketch, "E2115", {"start": v(11.6, 0.49) * mm, "end": v(11.49, 0.54) * mm});
            skLineSegment(sketch, "E2116", {"start": v(11.49, 0.54) * mm, "end": v(11.37, 0.6) * mm});
            skLineSegment(sketch, "E2117", {"start": v(11.37, 0.6) * mm, "end": v(11.26, 0.64) * mm});
            skLineSegment(sketch, "E2118", {"start": v(11.26, 0.64) * mm, "end": v(11.14, 0.69) * mm});
            skLineSegment(sketch, "E2119", {"start": v(11.14, 0.69) * mm, "end": v(11.02, 0.73) * mm});
            skLineSegment(sketch, "E2120", {"start": v(11.02, 0.73) * mm, "end": v(10.9, 0.78) * mm});
            skLineSegment(sketch, "E2121", {"start": v(10.9, 0.78) * mm, "end": v(10.79, 0.82) * mm});
            skLineSegment(sketch, "E2122", {"start": v(10.79, 0.82) * mm, "end": v(10.67, 0.85) * mm});
            skLineSegment(sketch, "E2123", {"start": v(10.67, 0.85) * mm, "end": v(10.55, 0.9) * mm});
            skLineSegment(sketch, "E2124", {"start": v(10.55, 0.9) * mm, "end": v(10.44, 0.93) * mm});
            skLineSegment(sketch, "E2125", {"start": v(10.44, 0.93) * mm, "end": v(10.32, 0.96) * mm});
            skLineSegment(sketch, "E2126", {"start": v(10.32, 0.96) * mm, "end": v(10.2, 0.99) * mm});
            skLineSegment(sketch, "E2127", {"start": v(10.2, 0.99) * mm, "end": v(10.08, 1.02) * mm});
            skLineSegment(sketch, "E2128", {"start": v(10.08, 1.02) * mm, "end": v(9.97, 1.04) * mm});
            skLineSegment(sketch, "E2129", {"start": v(9.97, 1.04) * mm, "end": v(9.85, 1.07) * mm});
            skLineSegment(sketch, "E2130", {"start": v(9.85, 1.07) * mm, "end": v(9.73, 1.09) * mm});
            skLineSegment(sketch, "E2131", {"start": v(9.73, 1.09) * mm, "end": v(9.61, 1.1) * mm});
            skLineSegment(sketch, "E2132", {"start": v(9.61, 1.1) * mm, "end": v(9.5, 1.13) * mm});
            skLineSegment(sketch, "E2133", {"start": v(9.5, 1.13) * mm, "end": v(9.38, 1.14) * mm});
            skLineSegment(sketch, "E2134", {"start": v(9.38, 1.14) * mm, "end": v(9.26, 1.16) * mm});
            skLineSegment(sketch, "E2135", {"start": v(9.26, 1.16) * mm, "end": v(9.14, 1.17) * mm});
            skLineSegment(sketch, "E2136", {"start": v(9.14, 1.17) * mm, "end": v(9.02, 1.18) * mm});
            skLineSegment(sketch, "E2137", {"start": v(9.02, 1.18) * mm, "end": v(8.9, 1.18) * mm});
            skLineSegment(sketch, "E2138", {"start": v(8.9, 1.18) * mm, "end": v(8.79, 1.19) * mm});
            skLineSegment(sketch, "E2139", {"start": v(8.79, 1.19) * mm, "end": v(8.67, 1.2) * mm});
            skLineSegment(sketch, "E2140", {"start": v(8.67, 1.2) * mm, "end": v(8.55, 1.2) * mm});
            skLineSegment(sketch, "E2141", {"start": v(8.55, 1.2) * mm, "end": v(8.43, 1.2) * mm});
            skLineSegment(sketch, "E2142", {"start": v(8.43, 1.2) * mm, "end": v(8.32, 1.19) * mm});
            skLineSegment(sketch, "E2143", {"start": v(8.32, 1.19) * mm, "end": v(8.2, 1.18) * mm});
            skLineSegment(sketch, "E2144", {"start": v(8.2, 1.18) * mm, "end": v(8.08, 1.18) * mm});
            skLineSegment(sketch, "E2145", {"start": v(8.08, 1.18) * mm, "end": v(7.97, 1.17) * mm});
            skLineSegment(sketch, "E2146", {"start": v(7.97, 1.17) * mm, "end": v(7.85, 1.16) * mm});
            skLineSegment(sketch, "E2147", {"start": v(7.85, 1.16) * mm, "end": v(7.74, 1.14) * mm});
            skLineSegment(sketch, "E2148", {"start": v(7.74, 1.14) * mm, "end": v(7.62, 1.13) * mm});
            skLineSegment(sketch, "E2149", {"start": v(7.62, 1.13) * mm, "end": v(7.5, 1.11) * mm});
            skLineSegment(sketch, "E2150", {"start": v(7.5, 1.11) * mm, "end": v(7.39, 1.1) * mm});
            skLineSegment(sketch, "E2151", {"start": v(7.39, 1.1) * mm, "end": v(7.27, 1.07) * mm});
            skLineSegment(sketch, "E2152", {"start": v(7.27, 1.07) * mm, "end": v(7.16, 1.05) * mm});
            skLineSegment(sketch, "E2153", {"start": v(7.16, 1.05) * mm, "end": v(7.04, 1.02) * mm});
            skLineSegment(sketch, "E2154", {"start": v(7.04, 1.02) * mm, "end": v(6.92, 1) * mm});
            skLineSegment(sketch, "E2155", {"start": v(6.92, 1) * mm, "end": v(6.8, 0.96) * mm});
            skLineSegment(sketch, "E2156", {"start": v(6.8, 0.96) * mm, "end": v(6.7, 0.93) * mm});
            skLineSegment(sketch, "E2157", {"start": v(6.7, 0.93) * mm, "end": v(6.58, 0.9) * mm});
            skLineSegment(sketch, "E2158", {"start": v(6.58, 0.9) * mm, "end": v(6.46, 0.86) * mm});
            skLineSegment(sketch, "E2159", {"start": v(6.46, 0.86) * mm, "end": v(6.35, 0.83) * mm});
            skLineSegment(sketch, "E2160", {"start": v(6.35, 0.83) * mm, "end": v(6.23, 0.79) * mm});
            skLineSegment(sketch, "E2161", {"start": v(6.23, 0.79) * mm, "end": v(6.11, 0.75) * mm});
            skLineSegment(sketch, "E2162", {"start": v(6.11, 0.75) * mm, "end": v(6, 0.7) * mm});
            skLineSegment(sketch, "E2163", {"start": v(6, 0.7) * mm, "end": v(5.88, 0.66) * mm});
            skLineSegment(sketch, "E2164", {"start": v(5.88, 0.66) * mm, "end": v(5.77, 0.6) * mm});
            skLineSegment(sketch, "E2165", {"start": v(5.77, 0.6) * mm, "end": v(5.65, 0.56) * mm});
            skLineSegment(sketch, "E2166", {"start": v(5.65, 0.56) * mm, "end": v(5.54, 0.5) * mm});
            skLineSegment(sketch, "E2167", {"start": v(5.54, 0.5) * mm, "end": v(5.42, 0.45) * mm});
            skLineSegment(sketch, "E2168", {"start": v(5.42, 0.45) * mm, "end": v(5.3, 0.4) * mm});
            skLineSegment(sketch, "E2169", {"start": v(5.3, 0.4) * mm, "end": v(5.2, 0.34) * mm});
            skLineSegment(sketch, "E2170", {"start": v(5.2, 0.34) * mm, "end": v(5.08, 0.28) * mm});
            skLineSegment(sketch, "E2171", {"start": v(5.08, 0.28) * mm, "end": v(5.05, 0.27) * mm});
            skLineSegment(sketch, "E2172", {"start": v(5.05, 0.27) * mm, "end": v(5.05, -0.36) * mm});
            skLineSegment(sketch, "E2173", {"start": v(5.05, -0.36) * mm, "end": v(5.06, -0.36) * mm});
            skLineSegment(sketch, "E2174", {"start": v(5.06, -0.36) * mm, "end": v(5.17, -0.41) * mm});
            skLineSegment(sketch, "E2175", {"start": v(5.17, -0.41) * mm, "end": v(5.29, -0.46) * mm});
            skLineSegment(sketch, "E2176", {"start": v(5.29, -0.46) * mm, "end": v(5.4, -0.5) * mm});
            skLineSegment(sketch, "E2177", {"start": v(5.4, -0.5) * mm, "end": v(5.52, -0.56) * mm});
            skLineSegment(sketch, "E2178", {"start": v(5.52, -0.56) * mm, "end": v(5.64, -0.6) * mm});
            skLineSegment(sketch, "E2179", {"start": v(5.64, -0.6) * mm, "end": v(5.75, -0.64) * mm});
            skLineSegment(sketch, "E2180", {"start": v(5.75, -0.64) * mm, "end": v(5.87, -0.68) * mm});
            skLineSegment(sketch, "E2181", {"start": v(5.87, -0.68) * mm, "end": v(5.98, -0.72) * mm});
            skLineSegment(sketch, "E2182", {"start": v(5.98, -0.72) * mm, "end": v(6.1, -0.76) * mm});
            skLineSegment(sketch, "E2183", {"start": v(6.1, -0.76) * mm, "end": v(6.22, -0.8) * mm});
            skLineSegment(sketch, "E2184", {"start": v(6.22, -0.8) * mm, "end": v(6.33, -0.83) * mm});
            skLineSegment(sketch, "E2185", {"start": v(6.33, -0.83) * mm, "end": v(6.45, -0.86) * mm});
            skLineSegment(sketch, "E2186", {"start": v(6.45, -0.86) * mm, "end": v(6.56, -0.9) * mm});
            skLineSegment(sketch, "E2187", {"start": v(6.56, -0.9) * mm, "end": v(6.68, -0.92) * mm});
            skLineSegment(sketch, "E2188", {"start": v(6.68, -0.92) * mm, "end": v(6.8, -0.95) * mm});
            skLineSegment(sketch, "E2189", {"start": v(6.8, -0.95) * mm, "end": v(6.91, -0.97) * mm});
            skLineSegment(sketch, "E2190", {"start": v(6.91, -0.97) * mm, "end": v(7.03, -1) * mm});
            skLineSegment(sketch, "E2191", {"start": v(7.03, -1) * mm, "end": v(7.15, -1.02) * mm});
            skLineSegment(sketch, "E2192", {"start": v(7.15, -1.02) * mm, "end": v(7.26, -1.04) * mm});
            skLineSegment(sketch, "E2193", {"start": v(7.26, -1.04) * mm, "end": v(7.38, -1.06) * mm});
            skLineSegment(sketch, "E2194", {"start": v(7.38, -1.06) * mm, "end": v(7.5, -1.08) * mm});
            skLineSegment(sketch, "E2195", {"start": v(7.5, -1.08) * mm, "end": v(7.61, -1.1) * mm});
            skLineSegment(sketch, "E2196", {"start": v(7.61, -1.1) * mm, "end": v(7.73, -1.1) * mm});
            skLineSegment(sketch, "E2197", {"start": v(7.73, -1.1) * mm, "end": v(7.85, -1.11) * mm});
            skLineSegment(sketch, "E2198", {"start": v(7.85, -1.11) * mm, "end": v(7.96, -1.12) * mm});
            skLineSegment(sketch, "E2199", {"start": v(7.96, -1.12) * mm, "end": v(8.08, -1.13) * mm});
            skLineSegment(sketch, "E2200", {"start": v(8.08, -1.13) * mm, "end": v(8.2, -1.14) * mm});
            skLineSegment(sketch, "E2201", {"start": v(8.2, -1.14) * mm, "end": v(8.32, -1.14) * mm});
            skLineSegment(sketch, "E2202", {"start": v(8.32, -1.14) * mm, "end": v(8.43, -1.15) * mm});
            skLineSegment(sketch, "E2203", {"start": v(8.43, -1.15) * mm, "end": v(8.55, -1.15) * mm});
            skLineSegment(sketch, "E2204", {"start": v(8.55, -1.15) * mm, "end": v(8.67, -1.15) * mm});
            skLineSegment(sketch, "E2205", {"start": v(-10.48, -1.2) * mm, "end": v(-10.36, -1.2) * mm});
            skLineSegment(sketch, "E2206", {"start": v(-10.36, -1.2) * mm, "end": v(-10.25, -1.19) * mm});
            skLineSegment(sketch, "E2207", {"start": v(-10.25, -1.19) * mm, "end": v(-10.13, -1.18) * mm});
            skLineSegment(sketch, "E2208", {"start": v(-10.13, -1.18) * mm, "end": v(-10.01, -1.17) * mm});
            skLineSegment(sketch, "E2209", {"start": v(-10.01, -1.17) * mm, "end": v(-9.9, -1.16) * mm});
            skLineSegment(sketch, "E2210", {"start": v(-9.9, -1.16) * mm, "end": v(-9.78, -1.15) * mm});
            skLineSegment(sketch, "E2211", {"start": v(-9.78, -1.15) * mm, "end": v(-9.66, -1.13) * mm});
            skLineSegment(sketch, "E2212", {"start": v(-9.66, -1.13) * mm, "end": v(-9.55, -1.11) * mm});
            skLineSegment(sketch, "E2213", {"start": v(-9.55, -1.11) * mm, "end": v(-9.43, -1.1) * mm});
            skLineSegment(sketch, "E2214", {"start": v(-9.43, -1.1) * mm, "end": v(-9.32, -1.07) * mm});
            skLineSegment(sketch, "E2215", {"start": v(-9.32, -1.07) * mm, "end": v(-9.2, -1.05) * mm});
            skLineSegment(sketch, "E2216", {"start": v(-9.2, -1.05) * mm, "end": v(-9.08, -1.02) * mm});
            skLineSegment(sketch, "E2217", {"start": v(-9.08, -1.02) * mm, "end": v(-8.97, -1) * mm});
            skLineSegment(sketch, "E2218", {"start": v(-8.97, -1) * mm, "end": v(-8.85, -0.97) * mm});
            skLineSegment(sketch, "E2219", {"start": v(-8.85, -0.97) * mm, "end": v(-8.74, -0.94) * mm});
            skLineSegment(sketch, "E2220", {"start": v(-8.74, -0.94) * mm, "end": v(-8.62, -0.9) * mm});
            skLineSegment(sketch, "E2221", {"start": v(-8.62, -0.9) * mm, "end": v(-8.5, -0.87) * mm});
            skLineSegment(sketch, "E2222", {"start": v(-8.5, -0.87) * mm, "end": v(-8.4, -0.83) * mm});
            skLineSegment(sketch, "E2223", {"start": v(-8.4, -0.83) * mm, "end": v(-8.28, -0.8) * mm});
            skLineSegment(sketch, "E2224", {"start": v(-8.28, -0.8) * mm, "end": v(-8.16, -0.75) * mm});
            skLineSegment(sketch, "E2225", {"start": v(-8.16, -0.75) * mm, "end": v(-8.04, -0.7) * mm});
            skLineSegment(sketch, "E2226", {"start": v(-8.04, -0.7) * mm, "end": v(-7.93, -0.66) * mm});
            skLineSegment(sketch, "E2227", {"start": v(-7.93, -0.66) * mm, "end": v(-7.81, -0.61) * mm});
            skLineSegment(sketch, "E2228", {"start": v(-7.81, -0.61) * mm, "end": v(-7.7, -0.56) * mm});
            skLineSegment(sketch, "E2229", {"start": v(-7.7, -0.56) * mm, "end": v(-7.58, -0.51) * mm});
            skLineSegment(sketch, "E2230", {"start": v(-7.58, -0.51) * mm, "end": v(-7.47, -0.46) * mm});
            skLineSegment(sketch, "E2231", {"start": v(-7.47, -0.46) * mm, "end": v(-7.35, -0.4) * mm});
            skLineSegment(sketch, "E2232", {"start": v(-7.35, -0.4) * mm, "end": v(-7.24, -0.35) * mm});
            skLineSegment(sketch, "E2233", {"start": v(-7.24, -0.35) * mm, "end": v(-7.12, -0.29) * mm});
            skLineSegment(sketch, "E2234", {"start": v(-7.12, -0.29) * mm, "end": v(-7.1, -0.27) * mm});
            skLineSegment(sketch, "E2235", {"start": v(-7.1, -0.27) * mm, "end": v(-7.1, 0.35) * mm});
            skLineSegment(sketch, "E2236", {"start": v(-7.1, 0.35) * mm, "end": v(-7.1, 0.36) * mm});
            skLineSegment(sketch, "E2237", {"start": v(-7.1, 0.36) * mm, "end": v(-7.22, 0.4) * mm});
            skLineSegment(sketch, "E2238", {"start": v(-7.22, 0.4) * mm, "end": v(-7.33, 0.46) * mm});
            skLineSegment(sketch, "E2239", {"start": v(-7.33, 0.46) * mm, "end": v(-7.45, 0.5) * mm});
            skLineSegment(sketch, "E2240", {"start": v(-7.45, 0.5) * mm, "end": v(-7.57, 0.55) * mm});
            skLineSegment(sketch, "E2241", {"start": v(-7.57, 0.55) * mm, "end": v(-7.68, 0.6) * mm});
            skLineSegment(sketch, "E2242", {"start": v(-7.68, 0.6) * mm, "end": v(-7.8, 0.64) * mm});
            skLineSegment(sketch, "E2243", {"start": v(-7.8, 0.64) * mm, "end": v(-7.91, 0.68) * mm});
            skLineSegment(sketch, "E2244", {"start": v(-7.91, 0.68) * mm, "end": v(-8.03, 0.72) * mm});
            skLineSegment(sketch, "E2245", {"start": v(-8.03, 0.72) * mm, "end": v(-8.14, 0.76) * mm});
            skLineSegment(sketch, "E2246", {"start": v(-8.14, 0.76) * mm, "end": v(-8.26, 0.8) * mm});
            skLineSegment(sketch, "E2247", {"start": v(-8.26, 0.8) * mm, "end": v(-8.38, 0.83) * mm});
            skLineSegment(sketch, "E2248", {"start": v(-8.38, 0.83) * mm, "end": v(-8.5, 0.86) * mm});
            skLineSegment(sketch, "E2249", {"start": v(-8.5, 0.86) * mm, "end": v(-8.6, 0.89) * mm});
            skLineSegment(sketch, "E2250", {"start": v(-8.6, 0.89) * mm, "end": v(-8.73, 0.92) * mm});
            skLineSegment(sketch, "E2251", {"start": v(-8.73, 0.92) * mm, "end": v(-8.84, 0.94) * mm});
            skLineSegment(sketch, "E2252", {"start": v(-8.84, 0.94) * mm, "end": v(-8.96, 0.97) * mm});
            skLineSegment(sketch, "E2253", {"start": v(-8.96, 0.97) * mm, "end": v(-9.07, 1) * mm});
            skLineSegment(sketch, "E2254", {"start": v(-9.07, 1) * mm, "end": v(-9.2, 1.02) * mm});
            skLineSegment(sketch, "E2255", {"start": v(-9.2, 1.02) * mm, "end": v(-9.3, 1.04) * mm});
            skLineSegment(sketch, "E2256", {"start": v(-9.3, 1.04) * mm, "end": v(-9.42, 1.05) * mm});
            skLineSegment(sketch, "E2257", {"start": v(-9.42, 1.05) * mm, "end": v(-9.54, 1.07) * mm});
            skLineSegment(sketch, "E2258", {"start": v(-9.54, 1.07) * mm, "end": v(-9.66, 1.09) * mm});
            skLineSegment(sketch, "E2259", {"start": v(-9.66, 1.09) * mm, "end": v(-9.77, 1.1) * mm});
            skLineSegment(sketch, "E2260", {"start": v(-9.77, 1.1) * mm, "end": v(-9.9, 1.11) * mm});
            skLineSegment(sketch, "E2261", {"start": v(-9.9, 1.11) * mm, "end": v(-10, 1.12) * mm});
            skLineSegment(sketch, "E2262", {"start": v(-10, 1.12) * mm, "end": v(-10.13, 1.13) * mm});
            skLineSegment(sketch, "E2263", {"start": v(-10.13, 1.13) * mm, "end": v(-10.24, 1.13) * mm});
            skLineSegment(sketch, "E2264", {"start": v(-10.24, 1.13) * mm, "end": v(-10.36, 1.14) * mm});
            skLineSegment(sketch, "E2265", {"start": v(-10.36, 1.14) * mm, "end": v(-10.48, 1.14) * mm});
            skLineSegment(sketch, "E2266", {"start": v(-10.48, 1.14) * mm, "end": v(-10.6, 1.14) * mm});
            skLineSegment(sketch, "E2267", {"start": v(-10.6, 1.14) * mm, "end": v(-10.72, 1.14) * mm});
            skLineSegment(sketch, "E2268", {"start": v(-10.72, 1.14) * mm, "end": v(-10.83, 1.14) * mm});
            skLineSegment(sketch, "E2269", {"start": v(-10.83, 1.14) * mm, "end": v(-10.95, 1.13) * mm});
            skLineSegment(sketch, "E2270", {"start": v(-10.95, 1.13) * mm, "end": v(-11.07, 1.13) * mm});
            skLineSegment(sketch, "E2271", {"start": v(-11.07, 1.13) * mm, "end": v(-11.2, 1.12) * mm});
            skLineSegment(sketch, "E2272", {"start": v(-11.2, 1.12) * mm, "end": v(-11.31, 1.1) * mm});
            skLineSegment(sketch, "E2273", {"start": v(-11.31, 1.1) * mm, "end": v(-11.43, 1.1) * mm});
            skLineSegment(sketch, "E2274", {"start": v(-11.43, 1.1) * mm, "end": v(-11.55, 1.08) * mm});
            skLineSegment(sketch, "E2275", {"start": v(-11.55, 1.08) * mm, "end": v(-11.67, 1.07) * mm});
            skLineSegment(sketch, "E2276", {"start": v(-11.67, 1.07) * mm, "end": v(-11.78, 1.05) * mm});
            skLineSegment(sketch, "E2277", {"start": v(-11.78, 1.05) * mm, "end": v(-11.9, 1.03) * mm});
            skLineSegment(sketch, "E2278", {"start": v(-11.9, 1.03) * mm, "end": v(-12.02, 1.01) * mm});
            skLineSegment(sketch, "E2279", {"start": v(-12.02, 1.01) * mm, "end": v(-12.14, 0.99) * mm});
            skLineSegment(sketch, "E2280", {"start": v(-12.14, 0.99) * mm, "end": v(-12.26, 0.97) * mm});
            skLineSegment(sketch, "E2281", {"start": v(-12.26, 0.97) * mm, "end": v(-12.38, 0.94) * mm});
            skLineSegment(sketch, "E2282", {"start": v(-12.38, 0.94) * mm, "end": v(-12.5, 0.91) * mm});
            skLineSegment(sketch, "E2283", {"start": v(-12.5, 0.91) * mm, "end": v(-12.61, 0.88) * mm});
            skLineSegment(sketch, "E2284", {"start": v(-12.61, 0.88) * mm, "end": v(-12.73, 0.85) * mm});
            skLineSegment(sketch, "E2285", {"start": v(-12.73, 0.85) * mm, "end": v(-12.85, 0.82) * mm});
            skLineSegment(sketch, "E2286", {"start": v(-12.85, 0.82) * mm, "end": v(-12.97, 0.78) * mm});
            skLineSegment(sketch, "E2287", {"start": v(-12.97, 0.78) * mm, "end": v(-13.08, 0.75) * mm});
            skLineSegment(sketch, "E2288", {"start": v(-13.08, 0.75) * mm, "end": v(-13.2, 0.7) * mm});
            skLineSegment(sketch, "E2289", {"start": v(-13.2, 0.7) * mm, "end": v(-13.32, 0.67) * mm});
            skLineSegment(sketch, "E2290", {"start": v(-13.32, 0.67) * mm, "end": v(-13.44, 0.62) * mm});
            skLineSegment(sketch, "E2291", {"start": v(-13.44, 0.62) * mm, "end": v(-13.55, 0.58) * mm});
            skLineSegment(sketch, "E2292", {"start": v(-13.55, 0.58) * mm, "end": v(-13.67, 0.53) * mm});
            skLineSegment(sketch, "E2293", {"start": v(-13.67, 0.53) * mm, "end": v(-13.79, 0.49) * mm});
            skLineSegment(sketch, "E2294", {"start": v(-13.79, 0.49) * mm, "end": v(-13.9, 0.44) * mm});
            skLineSegment(sketch, "E2295", {"start": v(-13.9, 0.44) * mm, "end": v(-14.02, 0.39) * mm});
            skLineSegment(sketch, "E2296", {"start": v(-14.02, 0.39) * mm, "end": v(-14.14, 0.33) * mm});
            skLineSegment(sketch, "E2297", {"start": v(-14.14, 0.33) * mm, "end": v(-14.15, 0.33) * mm});
            skLineSegment(sketch, "E2298", {"start": v(-14.15, 0.33) * mm, "end": v(-14.15, -0.24) * mm});
            skLineSegment(sketch, "E2299", {"start": v(-14.15, -0.24) * mm, "end": v(-14.12, -0.26) * mm});
            skLineSegment(sketch, "E2300", {"start": v(-14.12, -0.26) * mm, "end": v(-14, -0.32) * mm});
            skLineSegment(sketch, "E2301", {"start": v(-14, -0.32) * mm, "end": v(-13.89, -0.38) * mm});
            skLineSegment(sketch, "E2302", {"start": v(-13.89, -0.38) * mm, "end": v(-13.77, -0.44) * mm});
            skLineSegment(sketch, "E2303", {"start": v(-13.77, -0.44) * mm, "end": v(-13.65, -0.5) * mm});
            skLineSegment(sketch, "E2304", {"start": v(-13.65, -0.5) * mm, "end": v(-13.53, -0.55) * mm});
            skLineSegment(sketch, "E2305", {"start": v(-13.53, -0.55) * mm, "end": v(-13.42, -0.6) * mm});
            skLineSegment(sketch, "E2306", {"start": v(-13.42, -0.6) * mm, "end": v(-13.3, -0.65) * mm});
            skLineSegment(sketch, "E2307", {"start": v(-13.3, -0.65) * mm, "end": v(-13.18, -0.7) * mm});
            skLineSegment(sketch, "E2308", {"start": v(-13.18, -0.7) * mm, "end": v(-13.07, -0.74) * mm});
            skLineSegment(sketch, "E2309", {"start": v(-13.07, -0.74) * mm, "end": v(-12.95, -0.78) * mm});
            skLineSegment(sketch, "E2310", {"start": v(-12.95, -0.78) * mm, "end": v(-12.83, -0.82) * mm});
            skLineSegment(sketch, "E2311", {"start": v(-12.83, -0.82) * mm, "end": v(-12.72, -0.86) * mm});
            skLineSegment(sketch, "E2312", {"start": v(-12.72, -0.86) * mm, "end": v(-12.6, -0.9) * mm});
            skLineSegment(sketch, "E2313", {"start": v(-12.6, -0.9) * mm, "end": v(-12.48, -0.93) * mm});
            skLineSegment(sketch, "E2314", {"start": v(-12.48, -0.93) * mm, "end": v(-12.36, -0.96) * mm});
            skLineSegment(sketch, "E2315", {"start": v(-12.36, -0.96) * mm, "end": v(-12.25, -1) * mm});
            skLineSegment(sketch, "E2316", {"start": v(-12.25, -1) * mm, "end": v(-12.13, -1.02) * mm});
            skLineSegment(sketch, "E2317", {"start": v(-12.13, -1.02) * mm, "end": v(-12.01, -1.05) * mm});
            skLineSegment(sketch, "E2318", {"start": v(-12.01, -1.05) * mm, "end": v(-11.9, -1.07) * mm});
            skLineSegment(sketch, "E2319", {"start": v(-11.9, -1.07) * mm, "end": v(-11.78, -1.1) * mm});
            skLineSegment(sketch, "E2320", {"start": v(-11.78, -1.1) * mm, "end": v(-11.66, -1.11) * mm});
            skLineSegment(sketch, "E2321", {"start": v(-11.66, -1.11) * mm, "end": v(-11.54, -1.13) * mm});
            skLineSegment(sketch, "E2322", {"start": v(-11.54, -1.13) * mm, "end": v(-11.42, -1.15) * mm});
            skLineSegment(sketch, "E2323", {"start": v(-11.42, -1.15) * mm, "end": v(-11.3, -1.16) * mm});
            skLineSegment(sketch, "E2324", {"start": v(-11.3, -1.16) * mm, "end": v(-11.19, -1.17) * mm});
            skLineSegment(sketch, "E2325", {"start": v(-11.19, -1.17) * mm, "end": v(-11.07, -1.18) * mm});
            skLineSegment(sketch, "E2326", {"start": v(-11.07, -1.18) * mm, "end": v(-10.95, -1.19) * mm});
            skLineSegment(sketch, "E2327", {"start": v(-10.95, -1.19) * mm, "end": v(-10.83, -1.2) * mm});
            skLineSegment(sketch, "E2328", {"start": v(-10.83, -1.2) * mm, "end": v(-10.71, -1.2) * mm});
            skLineSegment(sketch, "E2329", {"start": v(-10.71, -1.2) * mm, "end": v(-10.6, -1.2) * mm});
            skLineSegment(sketch, "E2330", {"start": v(-10.6, -1.2) * mm, "end": v(-10.48, -1.2) * mm});
            skLineSegment(sketch, "E2331", {"start": v(-2.2, -16.2) * mm, "end": v(-2.29, -15.98) * mm});
            skLineSegment(sketch, "E2332", {"start": v(-2.29, -15.98) * mm, "end": v(-2.37, -15.76) * mm});
            skLineSegment(sketch, "E2333", {"start": v(-2.37, -15.76) * mm, "end": v(-2.46, -15.54) * mm});
            skLineSegment(sketch, "E2334", {"start": v(-2.46, -15.54) * mm, "end": v(-2.54, -15.32) * mm});
            skLineSegment(sketch, "E2335", {"start": v(-2.54, -15.32) * mm, "end": v(-2.62, -15.1) * mm});
            skLineSegment(sketch, "E2336", {"start": v(-2.62, -15.1) * mm, "end": v(-2.7, -14.88) * mm});
            skLineSegment(sketch, "E2337", {"start": v(-2.7, -14.88) * mm, "end": v(-2.77, -14.66) * mm});
            skLineSegment(sketch, "E2338", {"start": v(-2.77, -14.66) * mm, "end": v(-2.84, -14.44) * mm});
            skLineSegment(sketch, "E2339", {"start": v(-2.84, -14.44) * mm, "end": v(-2.9, -14.22) * mm});
            skLineSegment(sketch, "E2340", {"start": v(-2.9, -14.22) * mm, "end": v(-2.97, -14) * mm});
            skLineSegment(sketch, "E2341", {"start": v(-2.97, -14) * mm, "end": v(-3.04, -13.78) * mm});
            skLineSegment(sketch, "E2342", {"start": v(-3.04, -13.78) * mm, "end": v(-3.1, -13.55) * mm});
            skLineSegment(sketch, "E2343", {"start": v(-3.1, -13.55) * mm, "end": v(-3.15, -13.33) * mm});
            skLineSegment(sketch, "E2344", {"start": v(-3.15, -13.33) * mm, "end": v(-3.2, -13.11) * mm});
            skLineSegment(sketch, "E2345", {"start": v(-3.2, -13.11) * mm, "end": v(-3.25, -12.89) * mm});
            skLineSegment(sketch, "E2346", {"start": v(-3.25, -12.89) * mm, "end": v(-3.3, -12.67) * mm});
            skLineSegment(sketch, "E2347", {"start": v(-3.3, -12.67) * mm, "end": v(-3.34, -12.44) * mm});
            skLineSegment(sketch, "E2348", {"start": v(-3.34, -12.44) * mm, "end": v(-3.38, -12.22) * mm});
            skLineSegment(sketch, "E2349", {"start": v(-3.38, -12.22) * mm, "end": v(-3.41, -12) * mm});
            skLineSegment(sketch, "E2350", {"start": v(-3.41, -12) * mm, "end": v(-3.45, -11.78) * mm});
            skLineSegment(sketch, "E2351", {"start": v(-3.45, -11.78) * mm, "end": v(-3.48, -11.55) * mm});
            skLineSegment(sketch, "E2352", {"start": v(-3.48, -11.55) * mm, "end": v(-3.5, -11.33) * mm});
            skLineSegment(sketch, "E2353", {"start": v(-3.5, -11.33) * mm, "end": v(-3.53, -11.1) * mm});
            skLineSegment(sketch, "E2354", {"start": v(-3.53, -11.1) * mm, "end": v(-3.55, -10.88) * mm});
            skLineSegment(sketch, "E2355", {"start": v(-3.55, -10.88) * mm, "end": v(-3.57, -10.66) * mm});
            skLineSegment(sketch, "E2356", {"start": v(-3.57, -10.66) * mm, "end": v(-3.58, -10.43) * mm});
            skLineSegment(sketch, "E2357", {"start": v(-3.58, -10.43) * mm, "end": v(-3.6, -10.2) * mm});
            skLineSegment(sketch, "E2358", {"start": v(-3.6, -10.2) * mm, "end": v(-3.6, -9.99) * mm});
            skLineSegment(sketch, "E2359", {"start": v(-3.6, -9.99) * mm, "end": v(-3.6, -9.76) * mm});
            skLineSegment(sketch, "E2360", {"start": v(-3.6, -9.76) * mm, "end": v(-3.6, -9.54) * mm});
            skLineSegment(sketch, "E2361", {"start": v(-3.6, -9.54) * mm, "end": v(-3.6, -9.31) * mm});
            skLineSegment(sketch, "E2362", {"start": v(-3.6, -9.31) * mm, "end": v(-3.6, -9.1) * mm});
            skLineSegment(sketch, "E2363", {"start": v(-3.6, -9.1) * mm, "end": v(-3.6, -8.87) * mm});
            skLineSegment(sketch, "E2364", {"start": v(-3.6, -8.87) * mm, "end": v(-3.58, -8.65) * mm});
            skLineSegment(sketch, "E2365", {"start": v(-3.58, -8.65) * mm, "end": v(-3.57, -8.43) * mm});
            skLineSegment(sketch, "E2366", {"start": v(-3.57, -8.43) * mm, "end": v(-3.55, -8.2) * mm});
            skLineSegment(sketch, "E2367", {"start": v(-3.55, -8.2) * mm, "end": v(-3.53, -7.99) * mm});
            skLineSegment(sketch, "E2368", {"start": v(-3.53, -7.99) * mm, "end": v(-3.5, -7.77) * mm});
            skLineSegment(sketch, "E2369", {"start": v(-3.5, -7.77) * mm, "end": v(-3.48, -7.55) * mm});
            skLineSegment(sketch, "E2370", {"start": v(-3.48, -7.55) * mm, "end": v(-3.45, -7.33) * mm});
            skLineSegment(sketch, "E2371", {"start": v(-3.45, -7.33) * mm, "end": v(-3.42, -7.1) * mm});
            skLineSegment(sketch, "E2372", {"start": v(-3.42, -7.1) * mm, "end": v(-3.38, -6.89) * mm});
            skLineSegment(sketch, "E2373", {"start": v(-3.38, -6.89) * mm, "end": v(-3.34, -6.67) * mm});
            skLineSegment(sketch, "E2374", {"start": v(-3.34, -6.67) * mm, "end": v(-3.3, -6.45) * mm});
            skLineSegment(sketch, "E2375", {"start": v(-3.3, -6.45) * mm, "end": v(-3.26, -6.23) * mm});
            skLineSegment(sketch, "E2376", {"start": v(-3.26, -6.23) * mm, "end": v(-3.21, -6.01) * mm});
            skLineSegment(sketch, "E2377", {"start": v(-3.21, -6.01) * mm, "end": v(-3.16, -5.8) * mm});
            skLineSegment(sketch, "E2378", {"start": v(-3.16, -5.8) * mm, "end": v(-3.1, -5.57) * mm});
            skLineSegment(sketch, "E2379", {"start": v(-3.1, -5.57) * mm, "end": v(-3.05, -5.35) * mm});
            skLineSegment(sketch, "E2380", {"start": v(-3.05, -5.35) * mm, "end": v(-3, -5.14) * mm});
            skLineSegment(sketch, "E2381", {"start": v(-3, -5.14) * mm, "end": v(-2.93, -4.92) * mm});
            skLineSegment(sketch, "E2382", {"start": v(-2.93, -4.92) * mm, "end": v(-2.86, -4.7) * mm});
            skLineSegment(sketch, "E2383", {"start": v(-2.86, -4.7) * mm, "end": v(-2.8, -4.48) * mm});
            skLineSegment(sketch, "E2384", {"start": v(-2.8, -4.48) * mm, "end": v(-2.72, -4.27) * mm});
            skLineSegment(sketch, "E2385", {"start": v(-2.72, -4.27) * mm, "end": v(-2.65, -4.05) * mm});
            skLineSegment(sketch, "E2386", {"start": v(-2.65, -4.05) * mm, "end": v(-2.57, -3.83) * mm});
            skLineSegment(sketch, "E2387", {"start": v(-2.57, -3.83) * mm, "end": v(-2.5, -3.62) * mm});
            skLineSegment(sketch, "E2388", {"start": v(-2.5, -3.62) * mm, "end": v(-2.4, -3.4) * mm});
            skLineSegment(sketch, "E2389", {"start": v(-2.4, -3.4) * mm, "end": v(-2.32, -3.18) * mm});
            skLineSegment(sketch, "E2390", {"start": v(-2.32, -3.18) * mm, "end": v(-2.23, -2.97) * mm});
            skLineSegment(sketch, "E2391", {"start": v(-2.23, -2.97) * mm, "end": v(-2.16, -2.8) * mm});
            skLineSegment(sketch, "E2392", {"start": v(-2.16, -2.8) * mm, "end": v(-2.3, -2.73) * mm});
            skLineSegment(sketch, "E2393", {"start": v(-2.3, -2.73) * mm, "end": v(-2.48, -2.65) * mm});
            skLineSegment(sketch, "E2394", {"start": v(-2.48, -2.65) * mm, "end": v(-2.64, -2.55) * mm});
            skLineSegment(sketch, "E2395", {"start": v(-2.64, -2.55) * mm, "end": v(-2.8, -2.44) * mm});
            skLineSegment(sketch, "E2396", {"start": v(-2.8, -2.44) * mm, "end": v(-2.95, -2.33) * mm});
            skLineSegment(sketch, "E2397", {"start": v(-2.95, -2.33) * mm, "end": v(-3.09, -2.2) * mm});
            skLineSegment(sketch, "E2398", {"start": v(-3.09, -2.2) * mm, "end": v(-3.22, -2.07) * mm});
            skLineSegment(sketch, "E2399", {"start": v(-3.22, -2.07) * mm, "end": v(-3.35, -1.93) * mm});
            skLineSegment(sketch, "E2400", {"start": v(-3.35, -1.93) * mm, "end": v(-3.46, -1.78) * mm});
            skLineSegment(sketch, "E2401", {"start": v(-3.46, -1.78) * mm, "end": v(-3.57, -1.62) * mm});
            skLineSegment(sketch, "E2402", {"start": v(-3.57, -1.62) * mm, "end": v(-3.67, -1.46) * mm});
            skLineSegment(sketch, "E2403", {"start": v(-3.67, -1.46) * mm, "end": v(-3.75, -1.29) * mm});
            skLineSegment(sketch, "E2404", {"start": v(-3.75, -1.29) * mm, "end": v(-3.83, -1.11) * mm});
            skLineSegment(sketch, "E2405", {"start": v(-3.83, -1.11) * mm, "end": v(-3.86, -1.04) * mm});
            skLineSegment(sketch, "E2406", {"start": v(-3.86, -1.04) * mm, "end": v(-3.99, -1.1) * mm});
            skLineSegment(sketch, "E2407", {"start": v(-3.99, -1.1) * mm, "end": v(-4.2, -1.2) * mm});
            skLineSegment(sketch, "E2408", {"start": v(-4.2, -1.2) * mm, "end": v(-4.42, -1.3) * mm});
            skLineSegment(sketch, "E2409", {"start": v(-4.42, -1.3) * mm, "end": v(-4.64, -1.4) * mm});
            skLineSegment(sketch, "E2410", {"start": v(-4.64, -1.4) * mm, "end": v(-4.85, -1.5) * mm});
            skLineSegment(sketch, "E2411", {"start": v(-4.85, -1.5) * mm, "end": v(-5.07, -1.59) * mm});
            skLineSegment(sketch, "E2412", {"start": v(-5.07, -1.59) * mm, "end": v(-5.29, -1.67) * mm});
            skLineSegment(sketch, "E2413", {"start": v(-5.29, -1.67) * mm, "end": v(-5.5, -1.76) * mm});
            skLineSegment(sketch, "E2414", {"start": v(-5.5, -1.76) * mm, "end": v(-5.72, -1.84) * mm});
            skLineSegment(sketch, "E2415", {"start": v(-5.72, -1.84) * mm, "end": v(-5.94, -1.91) * mm});
            skLineSegment(sketch, "E2416", {"start": v(-5.94, -1.91) * mm, "end": v(-6.16, -1.98) * mm});
            skLineSegment(sketch, "E2417", {"start": v(-6.16, -1.98) * mm, "end": v(-6.38, -2.05) * mm});
            skLineSegment(sketch, "E2418", {"start": v(-6.38, -2.05) * mm, "end": v(-6.6, -2.12) * mm});
            skLineSegment(sketch, "E2419", {"start": v(-6.6, -2.12) * mm, "end": v(-6.81, -2.18) * mm});
            skLineSegment(sketch, "E2420", {"start": v(-6.81, -2.18) * mm, "end": v(-7.03, -2.24) * mm});
            skLineSegment(sketch, "E2421", {"start": v(-7.03, -2.24) * mm, "end": v(-7.25, -2.3) * mm});
            skLineSegment(sketch, "E2422", {"start": v(-7.25, -2.3) * mm, "end": v(-7.47, -2.35) * mm});
            skLineSegment(sketch, "E2423", {"start": v(-7.47, -2.35) * mm, "end": v(-7.69, -2.4) * mm});
            skLineSegment(sketch, "E2424", {"start": v(-7.69, -2.4) * mm, "end": v(-7.9, -2.44) * mm});
            skLineSegment(sketch, "E2425", {"start": v(-7.9, -2.44) * mm, "end": v(-8.13, -2.48) * mm});
            skLineSegment(sketch, "E2426", {"start": v(-8.13, -2.48) * mm, "end": v(-8.35, -2.52) * mm});
            skLineSegment(sketch, "E2427", {"start": v(-8.35, -2.52) * mm, "end": v(-8.57, -2.55) * mm});
            skLineSegment(sketch, "E2428", {"start": v(-8.57, -2.55) * mm, "end": v(-8.79, -2.58) * mm});
            skLineSegment(sketch, "E2429", {"start": v(-8.79, -2.58) * mm, "end": v(-9, -2.61) * mm});
            skLineSegment(sketch, "E2430", {"start": v(-9, -2.61) * mm, "end": v(-9.23, -2.63) * mm});
            skLineSegment(sketch, "E2431", {"start": v(-9.23, -2.63) * mm, "end": v(-9.45, -2.65) * mm});
            skLineSegment(sketch, "E2432", {"start": v(-9.45, -2.65) * mm, "end": v(-9.67, -2.67) * mm});
            skLineSegment(sketch, "E2433", {"start": v(-9.67, -2.67) * mm, "end": v(-9.9, -2.68) * mm});
            skLineSegment(sketch, "E2434", {"start": v(-9.9, -2.68) * mm, "end": v(-10.11, -2.7) * mm});
            skLineSegment(sketch, "E2435", {"start": v(-10.11, -2.7) * mm, "end": v(-10.33, -2.7) * mm});
            skLineSegment(sketch, "E2436", {"start": v(-10.33, -2.7) * mm, "end": v(-10.56, -2.7) * mm});
            skLineSegment(sketch, "E2437", {"start": v(-10.56, -2.7) * mm, "end": v(-10.78, -2.7) * mm});
            skLineSegment(sketch, "E2438", {"start": v(-10.78, -2.7) * mm, "end": v(-11, -2.7) * mm});
            skLineSegment(sketch, "E2439", {"start": v(-11, -2.7) * mm, "end": v(-11.23, -2.68) * mm});
            skLineSegment(sketch, "E2440", {"start": v(-11.23, -2.68) * mm, "end": v(-11.46, -2.67) * mm});
            skLineSegment(sketch, "E2441", {"start": v(-11.46, -2.67) * mm, "end": v(-11.68, -2.65) * mm});
            skLineSegment(sketch, "E2442", {"start": v(-11.68, -2.65) * mm, "end": v(-11.9, -2.63) * mm});
            skLineSegment(sketch, "E2443", {"start": v(-11.9, -2.63) * mm, "end": v(-12.13, -2.6) * mm});
            skLineSegment(sketch, "E2444", {"start": v(-12.13, -2.6) * mm, "end": v(-12.35, -2.58) * mm});
            skLineSegment(sketch, "E2445", {"start": v(-12.35, -2.58) * mm, "end": v(-12.57, -2.55) * mm});
            skLineSegment(sketch, "E2446", {"start": v(-12.57, -2.55) * mm, "end": v(-12.8, -2.51) * mm});
            skLineSegment(sketch, "E2447", {"start": v(-12.8, -2.51) * mm, "end": v(-13.02, -2.48) * mm});
            skLineSegment(sketch, "E2448", {"start": v(-13.02, -2.48) * mm, "end": v(-13.24, -2.43) * mm});
            skLineSegment(sketch, "E2449", {"start": v(-13.24, -2.43) * mm, "end": v(-13.47, -2.39) * mm});
            skLineSegment(sketch, "E2450", {"start": v(-13.47, -2.39) * mm, "end": v(-13.69, -2.34) * mm});
            skLineSegment(sketch, "E2451", {"start": v(-13.69, -2.34) * mm, "end": v(-13.9, -2.28) * mm});
            skLineSegment(sketch, "E2452", {"start": v(-13.9, -2.28) * mm, "end": v(-14.13, -2.23) * mm});
            skLineSegment(sketch, "E2453", {"start": v(-14.13, -2.23) * mm, "end": v(-14.35, -2.17) * mm});
            skLineSegment(sketch, "E2454", {"start": v(-14.35, -2.17) * mm, "end": v(-14.58, -2.1) * mm});
            skLineSegment(sketch, "E2455", {"start": v(-14.58, -2.1) * mm, "end": v(-14.8, -2.04) * mm});
            skLineSegment(sketch, "E2456", {"start": v(-14.8, -2.04) * mm, "end": v(-15.02, -1.96) * mm});
            skLineSegment(sketch, "E2457", {"start": v(-15.02, -1.96) * mm, "end": v(-15.24, -1.89) * mm});
            skLineSegment(sketch, "E2458", {"start": v(-15.24, -1.89) * mm, "end": v(-15.46, -1.81) * mm});
            skLineSegment(sketch, "E2459", {"start": v(-15.46, -1.81) * mm, "end": v(-15.68, -1.73) * mm});
            skLineSegment(sketch, "E2460", {"start": v(-15.68, -1.73) * mm, "end": v(-15.9, -1.64) * mm});
            skLineSegment(sketch, "E2461", {"start": v(-15.9, -1.64) * mm, "end": v(-16.12, -1.55) * mm});
            skLineSegment(sketch, "E2462", {"start": v(-16.12, -1.55) * mm, "end": v(-16.34, -1.46) * mm});
            skLineSegment(sketch, "E2463", {"start": v(-16.34, -1.46) * mm, "end": v(-16.56, -1.37) * mm});
            skLineSegment(sketch, "E2464", {"start": v(-16.56, -1.37) * mm, "end": v(-16.78, -1.27) * mm});
            skLineSegment(sketch, "E2465", {"start": v(-16.78, -1.27) * mm, "end": v(-17, -1.16) * mm});
            skLineSegment(sketch, "E2466", {"start": v(-17, -1.16) * mm, "end": v(-17.22, -1.06) * mm});
            skLineSegment(sketch, "E2467", {"start": v(-17.22, -1.06) * mm, "end": v(-17.35, -0.99) * mm});
            skLineSegment(sketch, "E2468", {"start": v(-17.35, -0.99) * mm, "end": v(-17.35, -1.03) * mm});
            skLineSegment(sketch, "E2469", {"start": v(-17.35, -1.03) * mm, "end": v(-17.25, -2.05) * mm});
            skLineSegment(sketch, "E2470", {"start": v(-17.25, -2.05) * mm, "end": v(-17.1, -3.07) * mm});
            skLineSegment(sketch, "E2471", {"start": v(-17.1, -3.07) * mm, "end": v(-16.87, -4.07) * mm});
            skLineSegment(sketch, "E2472", {"start": v(-16.87, -4.07) * mm, "end": v(-16.58, -5.06) * mm});
            skLineSegment(sketch, "E2473", {"start": v(-16.58, -5.06) * mm, "end": v(-16.23, -6.02) * mm});
            skLineSegment(sketch, "E2474", {"start": v(-16.23, -6.02) * mm, "end": v(-15.82, -6.97) * mm});
            skLineSegment(sketch, "E2475", {"start": v(-15.82, -6.97) * mm, "end": v(-15.36, -7.88) * mm});
            skLineSegment(sketch, "E2476", {"start": v(-15.36, -7.88) * mm, "end": v(-14.83, -8.77) * mm});
            skLineSegment(sketch, "E2477", {"start": v(-14.83, -8.77) * mm, "end": v(-14.26, -9.62) * mm});
            skLineSegment(sketch, "E2478", {"start": v(-14.26, -9.62) * mm, "end": v(-13.63, -10.43) * mm});
            skLineSegment(sketch, "E2479", {"start": v(-13.63, -10.43) * mm, "end": v(-12.95, -11.2) * mm});
            skLineSegment(sketch, "E2480", {"start": v(-12.95, -11.2) * mm, "end": v(-12.22, -11.93) * mm});
            skLineSegment(sketch, "E2481", {"start": v(-12.22, -11.93) * mm, "end": v(-11.45, -12.6) * mm});
            skLineSegment(sketch, "E2482", {"start": v(-11.45, -12.6) * mm, "end": v(-10.64, -13.24) * mm});
            skLineSegment(sketch, "E2483", {"start": v(-10.64, -13.24) * mm, "end": v(-9.79, -13.81) * mm});
            skLineSegment(sketch, "E2484", {"start": v(-9.79, -13.81) * mm, "end": v(-8.9, -14.34) * mm});
            skLineSegment(sketch, "E2485", {"start": v(-8.9, -14.34) * mm, "end": v(-7.99, -14.8) * mm});
            skLineSegment(sketch, "E2486", {"start": v(-7.99, -14.8) * mm, "end": v(-7.04, -15.21) * mm});
            skLineSegment(sketch, "E2487", {"start": v(-7.04, -15.21) * mm, "end": v(-6.08, -15.56) * mm});
            skLineSegment(sketch, "E2488", {"start": v(-6.08, -15.56) * mm, "end": v(-5.1, -15.85) * mm});
            skLineSegment(sketch, "E2489", {"start": v(-5.1, -15.85) * mm, "end": v(-4.09, -16.07) * mm});
            skLineSegment(sketch, "E2490", {"start": v(-4.09, -16.07) * mm, "end": v(-3.07, -16.23) * mm});
            skLineSegment(sketch, "E2491", {"start": v(-3.07, -16.23) * mm, "end": v(-2.14, -16.32) * mm});
            skLineSegment(sketch, "E2492", {"start": v(-2.14, -16.32) * mm, "end": v(-2.2, -16.2) * mm});
            skLineSegment(sketch, "E2493", {"start": v(0, -16.33) * mm, "end": v(1.03, -16.23) * mm});
            skLineSegment(sketch, "E2494", {"start": v(1.03, -16.23) * mm, "end": v(2.04, -16.07) * mm});
            skLineSegment(sketch, "E2495", {"start": v(2.04, -16.07) * mm, "end": v(3.05, -15.85) * mm});
            skLineSegment(sketch, "E2496", {"start": v(3.05, -15.85) * mm, "end": v(4.03, -15.56) * mm});
            skLineSegment(sketch, "E2497", {"start": v(4.03, -15.56) * mm, "end": v(5, -15.21) * mm});
            skLineSegment(sketch, "E2498", {"start": v(5, -15.21) * mm, "end": v(5.94, -14.8) * mm});
            skLineSegment(sketch, "E2499", {"start": v(5.94, -14.8) * mm, "end": v(6.86, -14.34) * mm});
            skLineSegment(sketch, "E2500", {"start": v(6.86, -14.34) * mm, "end": v(7.74, -13.81) * mm});
            skLineSegment(sketch, "E2501", {"start": v(7.74, -13.81) * mm, "end": v(8.6, -13.24) * mm});
            skLineSegment(sketch, "E2502", {"start": v(8.6, -13.24) * mm, "end": v(9.4, -12.6) * mm});
            skLineSegment(sketch, "E2503", {"start": v(9.4, -12.6) * mm, "end": v(10.17, -11.93) * mm});
            skLineSegment(sketch, "E2504", {"start": v(10.17, -11.93) * mm, "end": v(10.9, -11.2) * mm});
            skLineSegment(sketch, "E2505", {"start": v(10.9, -11.2) * mm, "end": v(11.58, -10.43) * mm});
            skLineSegment(sketch, "E2506", {"start": v(11.58, -10.43) * mm, "end": v(12.21, -9.62) * mm});
            skLineSegment(sketch, "E2507", {"start": v(12.21, -9.62) * mm, "end": v(12.79, -8.77) * mm});
            skLineSegment(sketch, "E2508", {"start": v(12.79, -8.77) * mm, "end": v(13.31, -7.88) * mm});
            skLineSegment(sketch, "E2509", {"start": v(13.31, -7.88) * mm, "end": v(13.78, -6.97) * mm});
            skLineSegment(sketch, "E2510", {"start": v(13.78, -6.97) * mm, "end": v(14.19, -6.02) * mm});
            skLineSegment(sketch, "E2511", {"start": v(14.19, -6.02) * mm, "end": v(14.53, -5.06) * mm});
            skLineSegment(sketch, "E2512", {"start": v(14.53, -5.06) * mm, "end": v(14.82, -4.07) * mm});
            skLineSegment(sketch, "E2513", {"start": v(14.82, -4.07) * mm, "end": v(15.05, -3.07) * mm});
            skLineSegment(sketch, "E2514", {"start": v(15.05, -3.07) * mm, "end": v(15.2, -2.05) * mm});
            skLineSegment(sketch, "E2515", {"start": v(15.2, -2.05) * mm, "end": v(15.3, -1.12) * mm});
            skLineSegment(sketch, "E2516", {"start": v(15.3, -1.12) * mm, "end": v(15.17, -1.17) * mm});
            skLineSegment(sketch, "E2517", {"start": v(15.17, -1.17) * mm, "end": v(14.95, -1.26) * mm});
            skLineSegment(sketch, "E2518", {"start": v(14.95, -1.26) * mm, "end": v(14.73, -1.35) * mm});
            skLineSegment(sketch, "E2519", {"start": v(14.73, -1.35) * mm, "end": v(14.51, -1.44) * mm});
            skLineSegment(sketch, "E2520", {"start": v(14.51, -1.44) * mm, "end": v(14.3, -1.52) * mm});
            skLineSegment(sketch, "E2521", {"start": v(14.3, -1.52) * mm, "end": v(14.07, -1.6) * mm});
            skLineSegment(sketch, "E2522", {"start": v(14.07, -1.6) * mm, "end": v(13.85, -1.68) * mm});
            skLineSegment(sketch, "E2523", {"start": v(13.85, -1.68) * mm, "end": v(13.63, -1.75) * mm});
            skLineSegment(sketch, "E2524", {"start": v(13.63, -1.75) * mm, "end": v(13.41, -1.82) * mm});
            skLineSegment(sketch, "E2525", {"start": v(13.41, -1.82) * mm, "end": v(13.2, -1.89) * mm});
            skLineSegment(sketch, "E2526", {"start": v(13.2, -1.89) * mm, "end": v(12.97, -1.95) * mm});
            skLineSegment(sketch, "E2527", {"start": v(12.97, -1.95) * mm, "end": v(12.75, -2.01) * mm});
            skLineSegment(sketch, "E2528", {"start": v(12.75, -2.01) * mm, "end": v(12.53, -2.07) * mm});
            skLineSegment(sketch, "E2529", {"start": v(12.53, -2.07) * mm, "end": v(12.3, -2.13) * mm});
            skLineSegment(sketch, "E2530", {"start": v(12.3, -2.13) * mm, "end": v(12.09, -2.18) * mm});
            skLineSegment(sketch, "E2531", {"start": v(12.09, -2.18) * mm, "end": v(11.86, -2.23) * mm});
            skLineSegment(sketch, "E2532", {"start": v(11.86, -2.23) * mm, "end": v(11.64, -2.27) * mm});
            skLineSegment(sketch, "E2533", {"start": v(11.64, -2.27) * mm, "end": v(11.42, -2.32) * mm});
            skLineSegment(sketch, "E2534", {"start": v(11.42, -2.32) * mm, "end": v(11.2, -2.36) * mm});
            skLineSegment(sketch, "E2535", {"start": v(11.2, -2.36) * mm, "end": v(10.97, -2.4) * mm});
            skLineSegment(sketch, "E2536", {"start": v(10.97, -2.4) * mm, "end": v(10.75, -2.43) * mm});
            skLineSegment(sketch, "E2537", {"start": v(10.75, -2.43) * mm, "end": v(10.53, -2.46) * mm});
            skLineSegment(sketch, "E2538", {"start": v(10.53, -2.46) * mm, "end": v(10.3, -2.48) * mm});
            skLineSegment(sketch, "E2539", {"start": v(10.3, -2.48) * mm, "end": v(10.08, -2.5) * mm});
            skLineSegment(sketch, "E2540", {"start": v(10.08, -2.5) * mm, "end": v(9.86, -2.53) * mm});
            skLineSegment(sketch, "E2541", {"start": v(9.86, -2.53) * mm, "end": v(9.63, -2.54) * mm});
            skLineSegment(sketch, "E2542", {"start": v(9.63, -2.54) * mm, "end": v(9.4, -2.56) * mm});
            skLineSegment(sketch, "E2543", {"start": v(9.4, -2.56) * mm, "end": v(9.19, -2.57) * mm});
            skLineSegment(sketch, "E2544", {"start": v(9.19, -2.57) * mm, "end": v(8.96, -2.58) * mm});
            skLineSegment(sketch, "E2545", {"start": v(8.96, -2.58) * mm, "end": v(8.74, -2.58) * mm});
            skLineSegment(sketch, "E2546", {"start": v(8.74, -2.58) * mm, "end": v(8.51, -2.58) * mm});
            skLineSegment(sketch, "E2547", {"start": v(8.51, -2.58) * mm, "end": v(8.29, -2.58) * mm});
            skLineSegment(sketch, "E2548", {"start": v(8.29, -2.58) * mm, "end": v(8.07, -2.58) * mm});
            skLineSegment(sketch, "E2549", {"start": v(8.07, -2.58) * mm, "end": v(7.85, -2.57) * mm});
            skLineSegment(sketch, "E2550", {"start": v(7.85, -2.57) * mm, "end": v(7.62, -2.56) * mm});
            skLineSegment(sketch, "E2551", {"start": v(7.62, -2.56) * mm, "end": v(7.4, -2.55) * mm});
            skLineSegment(sketch, "E2552", {"start": v(7.4, -2.55) * mm, "end": v(7.18, -2.53) * mm});
            skLineSegment(sketch, "E2553", {"start": v(7.18, -2.53) * mm, "end": v(6.96, -2.5) * mm});
            skLineSegment(sketch, "E2554", {"start": v(6.96, -2.5) * mm, "end": v(6.74, -2.49) * mm});
            skLineSegment(sketch, "E2555", {"start": v(6.74, -2.49) * mm, "end": v(6.52, -2.46) * mm});
            skLineSegment(sketch, "E2556", {"start": v(6.52, -2.46) * mm, "end": v(6.3, -2.43) * mm});
            skLineSegment(sketch, "E2557", {"start": v(6.3, -2.43) * mm, "end": v(6.08, -2.4) * mm});
            skLineSegment(sketch, "E2558", {"start": v(6.08, -2.4) * mm, "end": v(5.86, -2.36) * mm});
            skLineSegment(sketch, "E2559", {"start": v(5.86, -2.36) * mm, "end": v(5.64, -2.32) * mm});
            skLineSegment(sketch, "E2560", {"start": v(5.64, -2.32) * mm, "end": v(5.42, -2.28) * mm});
            skLineSegment(sketch, "E2561", {"start": v(5.42, -2.28) * mm, "end": v(5.2, -2.24) * mm});
            skLineSegment(sketch, "E2562", {"start": v(5.2, -2.24) * mm, "end": v(4.99, -2.2) * mm});
            skLineSegment(sketch, "E2563", {"start": v(4.99, -2.2) * mm, "end": v(4.77, -2.14) * mm});
            skLineSegment(sketch, "E2564", {"start": v(4.77, -2.14) * mm, "end": v(4.55, -2.09) * mm});
            skLineSegment(sketch, "E2565", {"start": v(4.55, -2.09) * mm, "end": v(4.33, -2.03) * mm});
            skLineSegment(sketch, "E2566", {"start": v(4.33, -2.03) * mm, "end": v(4.11, -1.97) * mm});
            skLineSegment(sketch, "E2567", {"start": v(4.11, -1.97) * mm, "end": v(3.9, -1.9) * mm});
            skLineSegment(sketch, "E2568", {"start": v(3.9, -1.9) * mm, "end": v(3.68, -1.84) * mm});
            skLineSegment(sketch, "E2569", {"start": v(3.68, -1.84) * mm, "end": v(3.46, -1.77) * mm});
            skLineSegment(sketch, "E2570", {"start": v(3.46, -1.77) * mm, "end": v(3.24, -1.7) * mm});
            skLineSegment(sketch, "E2571", {"start": v(3.24, -1.7) * mm, "end": v(3.03, -1.63) * mm});
            skLineSegment(sketch, "E2572", {"start": v(3.03, -1.63) * mm, "end": v(2.8, -1.55) * mm});
            skLineSegment(sketch, "E2573", {"start": v(2.8, -1.55) * mm, "end": v(2.6, -1.47) * mm});
            skLineSegment(sketch, "E2574", {"start": v(2.6, -1.47) * mm, "end": v(2.38, -1.39) * mm});
            skLineSegment(sketch, "E2575", {"start": v(2.38, -1.39) * mm, "end": v(2.16, -1.3) * mm});
            skLineSegment(sketch, "E2576", {"start": v(2.16, -1.3) * mm, "end": v(1.94, -1.21) * mm});
            skLineSegment(sketch, "E2577", {"start": v(1.94, -1.21) * mm, "end": v(1.77, -1.14) * mm});
            skLineSegment(sketch, "E2578", {"start": v(1.77, -1.14) * mm, "end": v(1.7, -1.29) * mm});
            skLineSegment(sketch, "E2579", {"start": v(1.7, -1.29) * mm, "end": v(1.62, -1.46) * mm});
            skLineSegment(sketch, "E2580", {"start": v(1.62, -1.46) * mm, "end": v(1.53, -1.62) * mm});
            skLineSegment(sketch, "E2581", {"start": v(1.53, -1.62) * mm, "end": v(1.42, -1.78) * mm});
            skLineSegment(sketch, "E2582", {"start": v(1.42, -1.78) * mm, "end": v(1.3, -1.93) * mm});
            skLineSegment(sketch, "E2583", {"start": v(1.3, -1.93) * mm, "end": v(1.18, -2.07) * mm});
            skLineSegment(sketch, "E2584", {"start": v(1.18, -2.07) * mm, "end": v(1.04, -2.2) * mm});
            skLineSegment(sketch, "E2585", {"start": v(1.04, -2.2) * mm, "end": v(0.9, -2.33) * mm});
            skLineSegment(sketch, "E2586", {"start": v(0.9, -2.33) * mm, "end": v(0.75, -2.44) * mm});
            skLineSegment(sketch, "E2587", {"start": v(0.75, -2.44) * mm, "end": v(0.6, -2.55) * mm});
            skLineSegment(sketch, "E2588", {"start": v(0.6, -2.55) * mm, "end": v(0.43, -2.65) * mm});
            skLineSegment(sketch, "E2589", {"start": v(0.43, -2.65) * mm, "end": v(0.26, -2.73) * mm});
            skLineSegment(sketch, "E2590", {"start": v(0.26, -2.73) * mm, "end": v(0.09, -2.8) * mm});
            skLineSegment(sketch, "E2591", {"start": v(0.09, -2.8) * mm, "end": v(0.01, -2.84) * mm});
            skLineSegment(sketch, "E2592", {"start": v(0.01, -2.84) * mm, "end": v(0.08, -2.97) * mm});
            skLineSegment(sketch, "E2593", {"start": v(0.08, -2.97) * mm, "end": v(0.18, -3.18) * mm});
            skLineSegment(sketch, "E2594", {"start": v(0.18, -3.18) * mm, "end": v(0.28, -3.4) * mm});
            skLineSegment(sketch, "E2595", {"start": v(0.28, -3.4) * mm, "end": v(0.38, -3.62) * mm});
            skLineSegment(sketch, "E2596", {"start": v(0.38, -3.62) * mm, "end": v(0.47, -3.83) * mm});
            skLineSegment(sketch, "E2597", {"start": v(0.47, -3.83) * mm, "end": v(0.56, -4.05) * mm});
            skLineSegment(sketch, "E2598", {"start": v(0.56, -4.05) * mm, "end": v(0.65, -4.27) * mm});
            skLineSegment(sketch, "E2599", {"start": v(0.65, -4.27) * mm, "end": v(0.73, -4.48) * mm});
            skLineSegment(sketch, "E2600", {"start": v(0.73, -4.48) * mm, "end": v(0.81, -4.7) * mm});
            skLineSegment(sketch, "E2601", {"start": v(0.81, -4.7) * mm, "end": v(0.89, -4.92) * mm});
            skLineSegment(sketch, "E2602", {"start": v(0.89, -4.92) * mm, "end": v(0.96, -5.14) * mm});
            skLineSegment(sketch, "E2603", {"start": v(0.96, -5.14) * mm, "end": v(1.03, -5.35) * mm});
            skLineSegment(sketch, "E2604", {"start": v(1.03, -5.35) * mm, "end": v(1.1, -5.57) * mm});
            skLineSegment(sketch, "E2605", {"start": v(1.1, -5.57) * mm, "end": v(1.16, -5.8) * mm});
            skLineSegment(sketch, "E2606", {"start": v(1.16, -5.8) * mm, "end": v(1.22, -6.01) * mm});
            skLineSegment(sketch, "E2607", {"start": v(1.22, -6.01) * mm, "end": v(1.27, -6.23) * mm});
            skLineSegment(sketch, "E2608", {"start": v(1.27, -6.23) * mm, "end": v(1.32, -6.45) * mm});
            skLineSegment(sketch, "E2609", {"start": v(1.32, -6.45) * mm, "end": v(1.37, -6.67) * mm});
            skLineSegment(sketch, "E2610", {"start": v(1.37, -6.67) * mm, "end": v(1.42, -6.89) * mm});
            skLineSegment(sketch, "E2611", {"start": v(1.42, -6.89) * mm, "end": v(1.46, -7.1) * mm});
            skLineSegment(sketch, "E2612", {"start": v(1.46, -7.1) * mm, "end": v(1.5, -7.33) * mm});
            skLineSegment(sketch, "E2613", {"start": v(1.5, -7.33) * mm, "end": v(1.53, -7.55) * mm});
            skLineSegment(sketch, "E2614", {"start": v(1.53, -7.55) * mm, "end": v(1.56, -7.77) * mm});
            skLineSegment(sketch, "E2615", {"start": v(1.56, -7.77) * mm, "end": v(1.59, -7.99) * mm});
            skLineSegment(sketch, "E2616", {"start": v(1.59, -7.99) * mm, "end": v(1.6, -8.2) * mm});
            skLineSegment(sketch, "E2617", {"start": v(1.6, -8.2) * mm, "end": v(1.63, -8.43) * mm});
            skLineSegment(sketch, "E2618", {"start": v(1.63, -8.43) * mm, "end": v(1.64, -8.65) * mm});
            skLineSegment(sketch, "E2619", {"start": v(1.64, -8.65) * mm, "end": v(1.66, -8.87) * mm});
            skLineSegment(sketch, "E2620", {"start": v(1.66, -8.87) * mm, "end": v(1.67, -9.1) * mm});
            skLineSegment(sketch, "E2621", {"start": v(1.67, -9.1) * mm, "end": v(1.67, -9.31) * mm});
            skLineSegment(sketch, "E2622", {"start": v(1.67, -9.31) * mm, "end": v(1.67, -9.54) * mm});
            skLineSegment(sketch, "E2623", {"start": v(1.67, -9.54) * mm, "end": v(1.67, -9.76) * mm});
            skLineSegment(sketch, "E2624", {"start": v(1.67, -9.76) * mm, "end": v(1.67, -9.99) * mm});
            skLineSegment(sketch, "E2625", {"start": v(1.67, -9.99) * mm, "end": v(1.66, -10.2) * mm});
            skLineSegment(sketch, "E2626", {"start": v(1.66, -10.2) * mm, "end": v(1.64, -10.43) * mm});
            skLineSegment(sketch, "E2627", {"start": v(1.64, -10.43) * mm, "end": v(1.63, -10.66) * mm});
            skLineSegment(sketch, "E2628", {"start": v(1.63, -10.66) * mm, "end": v(1.6, -10.88) * mm});
            skLineSegment(sketch, "E2629", {"start": v(1.6, -10.88) * mm, "end": v(1.58, -11.1) * mm});
            skLineSegment(sketch, "E2630", {"start": v(1.58, -11.1) * mm, "end": v(1.56, -11.33) * mm});
            skLineSegment(sketch, "E2631", {"start": v(1.56, -11.33) * mm, "end": v(1.52, -11.55) * mm});
            skLineSegment(sketch, "E2632", {"start": v(1.52, -11.55) * mm, "end": v(1.49, -11.78) * mm});
            skLineSegment(sketch, "E2633", {"start": v(1.49, -11.78) * mm, "end": v(1.45, -12) * mm});
            skLineSegment(sketch, "E2634", {"start": v(1.45, -12) * mm, "end": v(1.4, -12.22) * mm});
            skLineSegment(sketch, "E2635", {"start": v(1.4, -12.22) * mm, "end": v(1.36, -12.44) * mm});
            skLineSegment(sketch, "E2636", {"start": v(1.36, -12.44) * mm, "end": v(1.31, -12.67) * mm});
            skLineSegment(sketch, "E2637", {"start": v(1.31, -12.67) * mm, "end": v(1.26, -12.89) * mm});
            skLineSegment(sketch, "E2638", {"start": v(1.26, -12.89) * mm, "end": v(1.2, -13.11) * mm});
            skLineSegment(sketch, "E2639", {"start": v(1.2, -13.11) * mm, "end": v(1.14, -13.33) * mm});
            skLineSegment(sketch, "E2640", {"start": v(1.14, -13.33) * mm, "end": v(1.08, -13.55) * mm});
            skLineSegment(sketch, "E2641", {"start": v(1.08, -13.55) * mm, "end": v(1.01, -13.78) * mm});
            skLineSegment(sketch, "E2642", {"start": v(1.01, -13.78) * mm, "end": v(0.94, -14) * mm});
            skLineSegment(sketch, "E2643", {"start": v(0.94, -14) * mm, "end": v(0.86, -14.22) * mm});
            skLineSegment(sketch, "E2644", {"start": v(0.86, -14.22) * mm, "end": v(0.79, -14.44) * mm});
            skLineSegment(sketch, "E2645", {"start": v(0.79, -14.44) * mm, "end": v(0.7, -14.66) * mm});
            skLineSegment(sketch, "E2646", {"start": v(0.7, -14.66) * mm, "end": v(0.62, -14.88) * mm});
            skLineSegment(sketch, "E2647", {"start": v(0.62, -14.88) * mm, "end": v(0.53, -15.1) * mm});
            skLineSegment(sketch, "E2648", {"start": v(0.53, -15.1) * mm, "end": v(0.44, -15.32) * mm});
            skLineSegment(sketch, "E2649", {"start": v(0.44, -15.32) * mm, "end": v(0.34, -15.54) * mm});
            skLineSegment(sketch, "E2650", {"start": v(0.34, -15.54) * mm, "end": v(0.24, -15.76) * mm});
            skLineSegment(sketch, "E2651", {"start": v(0.24, -15.76) * mm, "end": v(0.14, -15.98) * mm});
            skLineSegment(sketch, "E2652", {"start": v(0.14, -15.98) * mm, "end": v(0.03, -16.2) * mm});
            skLineSegment(sketch, "E2653", {"start": v(0.03, -16.2) * mm, "end": v(-0.04, -16.33) * mm});
            skLineSegment(sketch, "E2654", {"start": v(-0.04, -16.33) * mm, "end": v(0, -16.33) * mm});
            skLineSegment(sketch, "E2655", {"start": v(-0.76, -13.1) * mm, "end": v(-0.7, -12.98) * mm});
            skLineSegment(sketch, "E2656", {"start": v(-0.7, -12.98) * mm, "end": v(-0.64, -12.86) * mm});
            skLineSegment(sketch, "E2657", {"start": v(-0.64, -12.86) * mm, "end": v(-0.59, -12.75) * mm});
            skLineSegment(sketch, "E2658", {"start": v(-0.59, -12.75) * mm, "end": v(-0.53, -12.63) * mm});
            skLineSegment(sketch, "E2659", {"start": v(-0.53, -12.63) * mm, "end": v(-0.48, -12.51) * mm});
            skLineSegment(sketch, "E2660", {"start": v(-0.48, -12.51) * mm, "end": v(-0.43, -12.4) * mm});
            skLineSegment(sketch, "E2661", {"start": v(-0.43, -12.4) * mm, "end": v(-0.38, -12.28) * mm});
            skLineSegment(sketch, "E2662", {"start": v(-0.38, -12.28) * mm, "end": v(-0.33, -12.16) * mm});
            skLineSegment(sketch, "E2663", {"start": v(-0.33, -12.16) * mm, "end": v(-0.29, -12.05) * mm});
            skLineSegment(sketch, "E2664", {"start": v(-0.29, -12.05) * mm, "end": v(-0.25, -11.93) * mm});
            skLineSegment(sketch, "E2665", {"start": v(-0.25, -11.93) * mm, "end": v(-0.2, -11.81) * mm});
            skLineSegment(sketch, "E2666", {"start": v(-0.2, -11.81) * mm, "end": v(-0.17, -11.7) * mm});
            skLineSegment(sketch, "E2667", {"start": v(-0.17, -11.7) * mm, "end": v(-0.13, -11.58) * mm});
            skLineSegment(sketch, "E2668", {"start": v(-0.13, -11.58) * mm, "end": v(-0.1, -11.46) * mm});
            skLineSegment(sketch, "E2669", {"start": v(-0.1, -11.46) * mm, "end": v(-0.06, -11.34) * mm});
            skLineSegment(sketch, "E2670", {"start": v(-0.06, -11.34) * mm, "end": v(-0.03, -11.23) * mm});
            skLineSegment(sketch, "E2671", {"start": v(-0.03, -11.23) * mm, "end": v(0, -11.1) * mm});
            skLineSegment(sketch, "E2672", {"start": v(0, -11.1) * mm, "end": v(0.02, -11) * mm});
            skLineSegment(sketch, "E2673", {"start": v(0.02, -11) * mm, "end": v(0.05, -10.87) * mm});
            skLineSegment(sketch, "E2674", {"start": v(0.05, -10.87) * mm, "end": v(0.07, -10.76) * mm});
            skLineSegment(sketch, "E2675", {"start": v(0.07, -10.76) * mm, "end": v(0.09, -10.64) * mm});
            skLineSegment(sketch, "E2676", {"start": v(0.09, -10.64) * mm, "end": v(0.1, -10.52) * mm});
            skLineSegment(sketch, "E2677", {"start": v(0.1, -10.52) * mm, "end": v(0.12, -10.4) * mm});
            skLineSegment(sketch, "E2678", {"start": v(0.12, -10.4) * mm, "end": v(0.13, -10.28) * mm});
            skLineSegment(sketch, "E2679", {"start": v(0.13, -10.28) * mm, "end": v(0.15, -10.17) * mm});
            skLineSegment(sketch, "E2680", {"start": v(0.15, -10.17) * mm, "end": v(0.16, -10.05) * mm});
            skLineSegment(sketch, "E2681", {"start": v(0.16, -10.05) * mm, "end": v(0.16, -9.93) * mm});
            skLineSegment(sketch, "E2682", {"start": v(0.16, -9.93) * mm, "end": v(0.17, -9.81) * mm});
            skLineSegment(sketch, "E2683", {"start": v(0.17, -9.81) * mm, "end": v(0.17, -9.7) * mm});
            skLineSegment(sketch, "E2684", {"start": v(0.17, -9.7) * mm, "end": v(0.17, -9.58) * mm});
            skLineSegment(sketch, "E2685", {"start": v(0.17, -9.58) * mm, "end": v(0.17, -9.46) * mm});
            skLineSegment(sketch, "E2686", {"start": v(0.17, -9.46) * mm, "end": v(0.17, -9.34) * mm});
            skLineSegment(sketch, "E2687", {"start": v(0.17, -9.34) * mm, "end": v(0.16, -9.23) * mm});
            skLineSegment(sketch, "E2688", {"start": v(0.16, -9.23) * mm, "end": v(0.16, -9.1) * mm});
            skLineSegment(sketch, "E2689", {"start": v(0.16, -9.1) * mm, "end": v(0.15, -9) * mm});
            skLineSegment(sketch, "E2690", {"start": v(0.15, -9) * mm, "end": v(0.14, -8.88) * mm});
            skLineSegment(sketch, "E2691", {"start": v(0.14, -8.88) * mm, "end": v(0.12, -8.76) * mm});
            skLineSegment(sketch, "E2692", {"start": v(0.12, -8.76) * mm, "end": v(0.1, -8.64) * mm});
            skLineSegment(sketch, "E2693", {"start": v(0.1, -8.64) * mm, "end": v(0.09, -8.53) * mm});
            skLineSegment(sketch, "E2694", {"start": v(0.09, -8.53) * mm, "end": v(0.07, -8.41) * mm});
            skLineSegment(sketch, "E2695", {"start": v(0.07, -8.41) * mm, "end": v(0.05, -8.3) * mm});
            skLineSegment(sketch, "E2696", {"start": v(0.05, -8.3) * mm, "end": v(0.03, -8.18) * mm});
            skLineSegment(sketch, "E2697", {"start": v(0.03, -8.18) * mm, "end": v(0, -8.06) * mm});
            skLineSegment(sketch, "E2698", {"start": v(0, -8.06) * mm, "end": v(-0.03, -7.95) * mm});
            skLineSegment(sketch, "E2699", {"start": v(-0.03, -7.95) * mm, "end": v(-0.06, -7.83) * mm});
            skLineSegment(sketch, "E2700", {"start": v(-0.06, -7.83) * mm, "end": v(-0.09, -7.72) * mm});
            skLineSegment(sketch, "E2701", {"start": v(-0.09, -7.72) * mm, "end": v(-0.12, -7.6) * mm});
            skLineSegment(sketch, "E2702", {"start": v(-0.12, -7.6) * mm, "end": v(-0.16, -7.49) * mm});
            skLineSegment(sketch, "E2703", {"start": v(-0.16, -7.49) * mm, "end": v(-0.2, -7.37) * mm});
            skLineSegment(sketch, "E2704", {"start": v(-0.2, -7.37) * mm, "end": v(-0.23, -7.25) * mm});
            skLineSegment(sketch, "E2705", {"start": v(-0.23, -7.25) * mm, "end": v(-0.28, -7.14) * mm});
            skLineSegment(sketch, "E2706", {"start": v(-0.28, -7.14) * mm, "end": v(-0.32, -7.02) * mm});
            skLineSegment(sketch, "E2707", {"start": v(-0.32, -7.02) * mm, "end": v(-0.36, -6.9) * mm});
            skLineSegment(sketch, "E2708", {"start": v(-0.36, -6.9) * mm, "end": v(-0.41, -6.8) * mm});
            skLineSegment(sketch, "E2709", {"start": v(-0.41, -6.8) * mm, "end": v(-0.46, -6.68) * mm});
            skLineSegment(sketch, "E2710", {"start": v(-0.46, -6.68) * mm, "end": v(-0.51, -6.56) * mm});
            skLineSegment(sketch, "E2711", {"start": v(-0.51, -6.56) * mm, "end": v(-0.57, -6.45) * mm});
            skLineSegment(sketch, "E2712", {"start": v(-0.57, -6.45) * mm, "end": v(-0.62, -6.33) * mm});
            skLineSegment(sketch, "E2713", {"start": v(-0.62, -6.33) * mm, "end": v(-0.68, -6.22) * mm});
            skLineSegment(sketch, "E2714", {"start": v(-0.68, -6.22) * mm, "end": v(-0.74, -6.1) * mm});
            skLineSegment(sketch, "E2715", {"start": v(-0.74, -6.1) * mm, "end": v(-0.75, -6.07) * mm});
            skLineSegment(sketch, "E2716", {"start": v(-0.75, -6.07) * mm, "end": v(-1.38, -6.07) * mm});
            skLineSegment(sketch, "E2717", {"start": v(-1.38, -6.07) * mm, "end": v(-1.38, -6.08) * mm});
            skLineSegment(sketch, "E2718", {"start": v(-1.38, -6.08) * mm, "end": v(-1.43, -6.2) * mm});
            skLineSegment(sketch, "E2719", {"start": v(-1.43, -6.2) * mm, "end": v(-1.48, -6.31) * mm});
            skLineSegment(sketch, "E2720", {"start": v(-1.48, -6.31) * mm, "end": v(-1.53, -6.43) * mm});
            skLineSegment(sketch, "E2721", {"start": v(-1.53, -6.43) * mm, "end": v(-1.58, -6.54) * mm});
            skLineSegment(sketch, "E2722", {"start": v(-1.58, -6.54) * mm, "end": v(-1.62, -6.66) * mm});
            skLineSegment(sketch, "E2723", {"start": v(-1.62, -6.66) * mm, "end": v(-1.66, -6.78) * mm});
            skLineSegment(sketch, "E2724", {"start": v(-1.66, -6.78) * mm, "end": v(-1.7, -6.9) * mm});
            skLineSegment(sketch, "E2725", {"start": v(-1.7, -6.9) * mm, "end": v(-1.74, -7) * mm});
            skLineSegment(sketch, "E2726", {"start": v(-1.74, -7) * mm, "end": v(-1.78, -7.12) * mm});
            skLineSegment(sketch, "E2727", {"start": v(-1.78, -7.12) * mm, "end": v(-1.82, -7.24) * mm});
            skLineSegment(sketch, "E2728", {"start": v(-1.82, -7.24) * mm, "end": v(-1.85, -7.36) * mm});
            skLineSegment(sketch, "E2729", {"start": v(-1.85, -7.36) * mm, "end": v(-1.88, -7.47) * mm});
            skLineSegment(sketch, "E2730", {"start": v(-1.88, -7.47) * mm, "end": v(-1.91, -7.59) * mm});
            skLineSegment(sketch, "E2731", {"start": v(-1.91, -7.59) * mm, "end": v(-1.94, -7.7) * mm});
            skLineSegment(sketch, "E2732", {"start": v(-1.94, -7.7) * mm, "end": v(-1.97, -7.82) * mm});
            skLineSegment(sketch, "E2733", {"start": v(-1.97, -7.82) * mm, "end": v(-2, -7.94) * mm});
            skLineSegment(sketch, "E2734", {"start": v(-2, -7.94) * mm, "end": v(-2.02, -8.05) * mm});
            skLineSegment(sketch, "E2735", {"start": v(-2.02, -8.05) * mm, "end": v(-2.04, -8.17) * mm});
            skLineSegment(sketch, "E2736", {"start": v(-2.04, -8.17) * mm, "end": v(-2.06, -8.29) * mm});
            skLineSegment(sketch, "E2737", {"start": v(-2.06, -8.29) * mm, "end": v(-2.08, -8.4) * mm});
            skLineSegment(sketch, "E2738", {"start": v(-2.08, -8.4) * mm, "end": v(-2.1, -8.52) * mm});
            skLineSegment(sketch, "E2739", {"start": v(-2.1, -8.52) * mm, "end": v(-2.11, -8.64) * mm});
            skLineSegment(sketch, "E2740", {"start": v(-2.11, -8.64) * mm, "end": v(-2.12, -8.75) * mm});
            skLineSegment(sketch, "E2741", {"start": v(-2.12, -8.75) * mm, "end": v(-2.14, -8.87) * mm});
            skLineSegment(sketch, "E2742", {"start": v(-2.14, -8.87) * mm, "end": v(-2.15, -8.99) * mm});
            skLineSegment(sketch, "E2743", {"start": v(-2.15, -8.99) * mm, "end": v(-2.15, -9.1) * mm});
            skLineSegment(sketch, "E2744", {"start": v(-2.15, -9.1) * mm, "end": v(-2.16, -9.22) * mm});
            skLineSegment(sketch, "E2745", {"start": v(-2.16, -9.22) * mm, "end": v(-2.16, -9.34) * mm});
            skLineSegment(sketch, "E2746", {"start": v(-2.16, -9.34) * mm, "end": v(-2.17, -9.46) * mm});
            skLineSegment(sketch, "E2747", {"start": v(-2.17, -9.46) * mm, "end": v(-2.17, -9.58) * mm});
            skLineSegment(sketch, "E2748", {"start": v(-2.17, -9.58) * mm, "end": v(-2.17, -9.7) * mm});
            skLineSegment(sketch, "E2749", {"start": v(-2.17, -9.7) * mm, "end": v(-2.16, -9.81) * mm});
            skLineSegment(sketch, "E2750", {"start": v(-2.16, -9.81) * mm, "end": v(-2.16, -9.93) * mm});
            skLineSegment(sketch, "E2751", {"start": v(-2.16, -9.93) * mm, "end": v(-2.15, -10.05) * mm});
            skLineSegment(sketch, "E2752", {"start": v(-2.15, -10.05) * mm, "end": v(-2.14, -10.17) * mm});
            skLineSegment(sketch, "E2753", {"start": v(-2.14, -10.17) * mm, "end": v(-2.13, -10.29) * mm});
            skLineSegment(sketch, "E2754", {"start": v(-2.13, -10.29) * mm, "end": v(-2.12, -10.4) * mm});
            skLineSegment(sketch, "E2755", {"start": v(-2.12, -10.4) * mm, "end": v(-2.1, -10.53) * mm});
            skLineSegment(sketch, "E2756", {"start": v(-2.1, -10.53) * mm, "end": v(-2.1, -10.65) * mm});
            skLineSegment(sketch, "E2757", {"start": v(-2.1, -10.65) * mm, "end": v(-2.08, -10.76) * mm});
            skLineSegment(sketch, "E2758", {"start": v(-2.08, -10.76) * mm, "end": v(-2.06, -10.88) * mm});
            skLineSegment(sketch, "E2759", {"start": v(-2.06, -10.88) * mm, "end": v(-2.04, -11) * mm});
            skLineSegment(sketch, "E2760", {"start": v(-2.04, -11) * mm, "end": v(-2.01, -11.12) * mm});
            skLineSegment(sketch, "E2761", {"start": v(-2.01, -11.12) * mm, "end": v(-2, -11.24) * mm});
            skLineSegment(sketch, "E2762", {"start": v(-2, -11.24) * mm, "end": v(-1.96, -11.36) * mm});
            skLineSegment(sketch, "E2763", {"start": v(-1.96, -11.36) * mm, "end": v(-1.94, -11.47) * mm});
            skLineSegment(sketch, "E2764", {"start": v(-1.94, -11.47) * mm, "end": v(-1.9, -11.6) * mm});
            skLineSegment(sketch, "E2765", {"start": v(-1.9, -11.6) * mm, "end": v(-1.87, -11.7) * mm});
            skLineSegment(sketch, "E2766", {"start": v(-1.87, -11.7) * mm, "end": v(-1.84, -11.83) * mm});
            skLineSegment(sketch, "E2767", {"start": v(-1.84, -11.83) * mm, "end": v(-1.8, -11.94) * mm});
            skLineSegment(sketch, "E2768", {"start": v(-1.8, -11.94) * mm, "end": v(-1.77, -12.06) * mm});
            skLineSegment(sketch, "E2769", {"start": v(-1.77, -12.06) * mm, "end": v(-1.73, -12.18) * mm});
            skLineSegment(sketch, "E2770", {"start": v(-1.73, -12.18) * mm, "end": v(-1.7, -12.3) * mm});
            skLineSegment(sketch, "E2771", {"start": v(-1.7, -12.3) * mm, "end": v(-1.65, -12.41) * mm});
            skLineSegment(sketch, "E2772", {"start": v(-1.65, -12.41) * mm, "end": v(-1.6, -12.53) * mm});
            skLineSegment(sketch, "E2773", {"start": v(-1.6, -12.53) * mm, "end": v(-1.56, -12.65) * mm});
            skLineSegment(sketch, "E2774", {"start": v(-1.56, -12.65) * mm, "end": v(-1.51, -12.77) * mm});
            skLineSegment(sketch, "E2775", {"start": v(-1.51, -12.77) * mm, "end": v(-1.46, -12.88) * mm});
            skLineSegment(sketch, "E2776", {"start": v(-1.46, -12.88) * mm, "end": v(-1.41, -13) * mm});
            skLineSegment(sketch, "E2777", {"start": v(-1.41, -13) * mm, "end": v(-1.36, -13.12) * mm});
            skLineSegment(sketch, "E2778", {"start": v(-1.36, -13.12) * mm, "end": v(-1.35, -13.13) * mm});
            skLineSegment(sketch, "E2779", {"start": v(-1.35, -13.13) * mm, "end": v(-0.78, -13.13) * mm});
            skLineSegment(sketch, "E2780", {"start": v(-0.78, -13.13) * mm, "end": v(-0.76, -13.1) * mm});
            skCircle(sketch, "E2781", {"center": v(-1.02, 0) * mm, "radius": 1 * mm});
            skSolve(sketch);
        }
        {
            var Q0;
            Q0=makeQuery(id+"F0.imprint","IMPRINT",FACE,{"disambiguationData":[TD([[makeQuery(id+"F0.imprint","IMPRINT",EDGE,{"derivedFrom":sQuery(id+"F0.wireOp",EDGE,"E0")}),1.0]])]});
            extrude(context, id + "F1", {"entities" : qUnion([Q0]), "depth" : 5 * mm});
        }
    });
